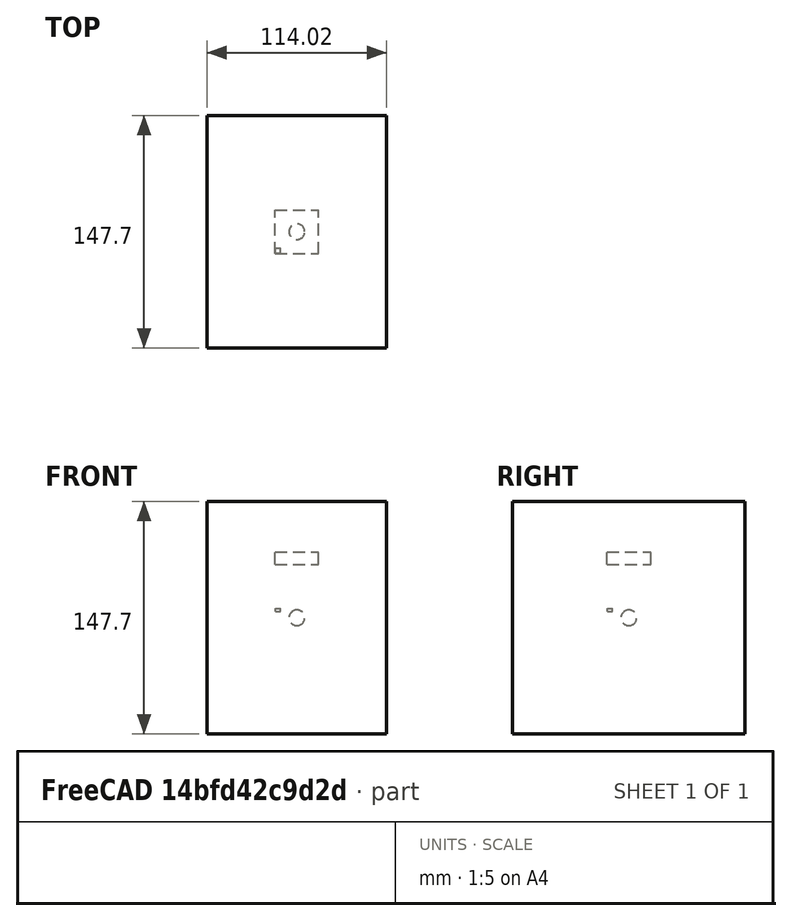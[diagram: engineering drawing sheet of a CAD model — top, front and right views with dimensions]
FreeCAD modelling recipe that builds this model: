
FCSTD DOCUMENT  (FreeCAD 0.20R29177 (Git))
Label: NewBS-NoArray-borderTest-1
License: All rights reserved
objects: App::DocumentObjectGroupPython×1272, App::Link×77, App::Part×7, Part::FeaturePython×4, App::FeaturePython×1
note: 4 computed .brp shape members not serialized (recipe doc carries the construction recipe); baked Part::Feature solids carry a one-line shape summary decoded from their .brp

FEATURE [App::DocumentObjectGroupPython] HALFPI  # scripted group (container) (typed FeaturePython)
  name = HALFPI
  value = pi/2.
FEATURE [App::DocumentObjectGroupPython] PI  # scripted group (container) (typed FeaturePython)
  name = PI
  value = 1.*pi
FEATURE [App::DocumentObjectGroupPython] TWOPI  # scripted group (container) (typed FeaturePython)
  name = TWOPI
  value = 2.*pi
FEATURE [App::DocumentObjectGroupPython] Constants  # scripted group (container) (typed FeaturePython)
  Group = -> [HALFPI,PI,TWOPI]
FEATURE [App::DocumentObjectGroupPython] Variables  # scripted group (container) (typed FeaturePython)
FEATURE [App::DocumentObjectGroupPython] Quantities  # scripted group (container) (typed FeaturePython)
FEATURE [App::DocumentObjectGroupPython] Isotopes  # scripted group (container) (typed FeaturePython)
FEATURE [App::DocumentObjectGroupPython] Elements  # scripted group (container) (typed FeaturePython)
FEATURE [App::DocumentObjectGroupPython] G4_AIR  label="G4_AIR : 1.000"  # scripted group (container) (typed FeaturePython)
  n = 1
FEATURE [App::DocumentObjectGroupPython] Air  # scripted group (container) (typed FeaturePython)
  Dunit = mg/cm3
  Dvalue = 1.29
  Group = -> [G4_AIR]
  RINDEX = AirRINDEX
  conduct = 2
  density = 1
  expand = 3
  name = Air
  specific = 4
FEATURE [App::DocumentObjectGroupPython] SY  # scripted group (container) (typed FeaturePython)
  coldim = 1
  values = 100000/MeV
FEATURE [App::DocumentObjectGroupPython] RS  # scripted group (container) (typed FeaturePython)
  coldim = 1
  values = 1
FEATURE [App::DocumentObjectGroupPython] FTC  # scripted group (container) (typed FeaturePython)
  coldim = 1
  values = 21.5*ns
FEATURE [App::DocumentObjectGroupPython] STC  # scripted group (container) (typed FeaturePython)
  coldim = 1
  values = 43.8*ns
FEATURE [App::DocumentObjectGroupPython] RY1  # scripted group (container) (typed FeaturePython)
  coldim = 1
  values = 95
FEATURE [App::DocumentObjectGroupPython] RY2  # scripted group (container) (typed FeaturePython)
  coldim = 1
  values = 5
FEATURE [App::DocumentObjectGroupPython] YR  # scripted group (container) (typed FeaturePython)
  coldim = 1
  values = 0.8
FEATURE [App::DocumentObjectGroupPython] SCINTLAR  # scripted group (container) (typed FeaturePython)
  coldim = 2
  values = <blob: 2358 chars omitted>
FEATURE [App::DocumentObjectGroupPython] RINDEXLAR  # scripted group (container) (typed FeaturePython)
  coldim = 2
  values = <blob: 9384 chars omitted>
FEATURE [App::DocumentObjectGroupPython] ABSLENGTHLAR  # scripted group (container) (typed FeaturePython)
  coldim = 2
  values = 7.74901*eV 10.0*m 7.77525*eV 10.0*m 7.80167*eV 10.0*m 7.82827*eV 10.0*m 7.85506*eV 10.0*m 7.88202*eV 10.0*m 7.90917*eV 10.0*m 7.93651*eV 10.0*m 7.96404*eV 10.0*m 7.99176*eV 10.0*m 8.01968*eV 10.0*m 8.04779*eV 10.0*m 8.07609*eV 10.0*m 8.1046*eV 10.0*m 8.13331*eV 10.0*m 8.16222*eV 10.0*m 8.19134*eV 10.0*m 8.22067*eV 10.0*m 8.25021*eV 10.0*m 8.27996*eV 10.0*m 8.30993*eV 10.0*m 8.34012*eV 10.0*m 8.37052*eV 10.0*m 8.40115*eV 10.0*m 8.432*eV 10.0*m 8.46308*eV 10.0*m 8.4944*eV 10.0*m 8.52594*eV 10.0*m 8.55772*eV 10.0*m 8.58973*eV 10.0*m 8.62199*eV 10.0*m 8.65449*eV 10.0*m 8.68723*eV 10.0*m 8.72023*eV 10.0*m 8.75347*eV 10.0*m 8.78697*eV 10.0*m 8.82073*eV 10.0*m 8.85475*eV 10.0*m 8.88903*eV 10.0*m 8.92358*eV 10.0*m 8.9584*eV 10.0*m 8.99349*eV 10.0*m 9.02885*eV 10.0*m 9.0645*eV 10.0*m 9.10043*eV 10.0*m 9.13664*eV 10.0*m 9.17314*eV 10.0*m 9.20994*eV 10.0*m 9.24703*eV 10.0*m 9.28442*eV 10.0*m 9.32212*eV 10.0*m 9.36012*eV 10.0*m 9.39844*eV 10.0*m 9.43707*eV 10.0*m 9.47602*eV 10.0*m 9.51529*eV 10.0*m 9.55489*eV 10.0*m 9.59481*eV 10.0*m 9.63508*eV 10.0*m 9.67568*eV 10.0*m 9.71663*eV 10.0*m 9.75792*eV 10.0*m 9.79957*eV 10.0*m 9.84158*eV 10.0*m 9.88394*eV 10.0*m 9.92668*eV 10.0*m 9.96978*eV 10.0*m 10.0133*eV 10.0*m 10.0571*eV 10.0*m 10.1014*eV 10.0*m 10.146*eV 10.0*m 10.191*eV 10.0*m 10.2365*eV 10.0*m 10.2823*eV 10.0*m 10.3286*eV 10.0*m 10.3752*eV 10.0*m 10.4223*eV 10.0*m 10.4699*eV 10.0*m 10.5178*eV 10.0*m 10.5662*eV 10.0*m 10.6151*eV 10.0*m 10.6644*eV 10.0*m 10.7142*eV 10.0*m 10.7644*eV 10.0*m 10.8151*eV 10.0*m 10.8663*eV 10.0*m 10.9179*eV 10.0*m 10.9701*eV 10.0*m 11.0228*eV 10.0*m 11.076*eV 10.0*m 11.1296*eV 10.0*m 11.1839*eV 10.0*m 11.2386*eV 10.0*m 11.2939*eV 10.0*m 11.3497*eV 10.0*m 11.4061*eV 10.0*m 11.463*eV 10.0*m 11.5206*eV 10.0*m 11.5787*eV 10.0*m 11.6373*eV 10.0*m
FEATURE [App::DocumentObjectGroupPython] RAYLEIGHLAR  # scripted group (container) (typed FeaturePython)
  coldim = 2
  values = 7.74901*eV 90.0*cm 7.77525*eV 90.0*cm 7.80167*eV 90.0*cm 7.82827*eV 90.0*cm 7.85506*eV 90.0*cm 7.88202*eV 90.0*cm 7.90917*eV 90.0*cm 7.93651*eV 90.0*cm 7.96404*eV 90.0*cm 7.99176*eV 90.0*cm 8.01968*eV 90.0*cm 8.04779*eV 90.0*cm 8.07609*eV 90.0*cm 8.1046*eV 90.0*cm 8.13331*eV 90.0*cm 8.16222*eV 90.0*cm 8.19134*eV 90.0*cm 8.22067*eV 90.0*cm 8.25021*eV 90.0*cm 8.27996*eV 90.0*cm 8.30993*eV 90.0*cm 8.34012*eV 90.0*cm 8.37052*eV 90.0*cm 8.40115*eV 90.0*cm 8.432*eV 90.0*cm 8.46308*eV 90.0*cm 8.4944*eV 90.0*cm 8.52594*eV 90.0*cm 8.55772*eV 90.0*cm 8.58973*eV 90.0*cm 8.62199*eV 90.0*cm 8.65449*eV 90.0*cm 8.68723*eV 90.0*cm 8.72023*eV 90.0*cm 8.75347*eV 90.0*cm 8.78697*eV 90.0*cm 8.82073*eV 90.0*cm 8.85475*eV 90.0*cm 8.88903*eV 90.0*cm 8.92358*eV 90.0*cm 8.9584*eV 90.0*cm 8.99349*eV 90.0*cm 9.02885*eV 90.0*cm 9.0645*eV 90.0*cm 9.10043*eV 90.0*cm 9.13664*eV 90.0*cm 9.17314*eV 90.0*cm 9.20994*eV 90.0*cm 9.24703*eV 90.0*cm 9.28442*eV 90.0*cm 9.32212*eV 90.0*cm 9.36012*eV 90.0*cm 9.39844*eV 90.0*cm 9.43707*eV 90.0*cm 9.47602*eV 90.0*cm 9.51529*eV 90.0*cm 9.55489*eV 90.0*cm 9.59481*eV 90.0*cm 9.63508*eV 90.0*cm 9.67568*eV 90.0*cm 9.71663*eV 90.0*cm 9.75792*eV 90.0*cm 9.79957*eV 90.0*cm 9.84158*eV 90.0*cm 9.88394*eV 90.0*cm 9.92668*eV 90.0*cm 9.96978*eV 90.0*cm 10.0133*eV 90.0*cm 10.0571*eV 90.0*cm 10.1014*eV 90.0*cm 10.146*eV 90.0*cm 10.191*eV 90.0*cm 10.2365*eV 90.0*cm 10.2823*eV 90.0*cm 10.3286*eV 90.0*cm 10.3752*eV 90.0*cm 10.4223*eV 90.0*cm 10.4699*eV 90.0*cm 10.5178*eV 90.0*cm 10.5662*eV 90.0*cm 10.6151*eV 90.0*cm 10.6644*eV 90.0*cm 10.7142*eV 90.0*cm 10.7644*eV 90.0*cm 10.8151*eV 90.0*cm 10.8663*eV 90.0*cm 10.9179*eV 90.0*cm 10.9701*eV 90.0*cm 11.0228*eV 90.0*cm 11.076*eV 90.0*cm 11.1296*eV 90.0*cm 11.1839*eV 90.0*cm 11.2386*eV 90.0*cm 11.2939*eV 90.0*cm 11.3497*eV 90.0*cm 11.4061*eV 90.0*cm 11.463*eV 90.0*cm 11.5206*eV 90.0*cm 11.5787*eV 90.0*cm 11.6373*eV 90.0*cm
FEATURE [App::DocumentObjectGroupPython] REFLECTIVITY  # scripted group (container) (typed FeaturePython)
  coldim = 2
  values = 2.034*eV 0.98 2.068*eV 0.98 2.103*eV 0.98 2.139*eV 0.98 2.177*eV 0.98 2.216*eV 0.98 2.256*eV 0.98 2.298*eV 0.98 2.341*eV 0.98 2.386*eV 0.98 2.433*eV 0.98 2.481*eV 0.98 2.532*eV 0.98 2.585*eV 0.98 2.64*eV 0.98 2.697*eV 0.98 2.757*eV 0.98 2.82*eV 0.98 2.885*eV 0.98 2.954*eV 0.98 3.026*eV 0.98 3.102*eV 0.98 3.181*eV 0.98 3.265*eV 0.98 3.353*eV 0.98 3.446*eV 0.98 3.545*eV 0.98 3.649*eV 0.98 3.76*eV 0.98 3.877*eV 0.98 4.002*eV 0.98 4.136*eV 0.98 5.0*eV 0.98 6.0*eV 0.98 7.0*eV 0.98 8.0*eV 0.98 9.0*eV 0.98 9.0*eV 0.98 10.0*eV 0.98 11.0*eV 0.98 11.6*eV 0.98
FEATURE [App::DocumentObjectGroupPython] EFFICIENCY  # scripted group (container) (typed FeaturePython)
  coldim = 2
  values = 2.034*eV 1 2.068*eV 1 2.103*eV 1 2.139*eV 1 2.177*eV 1 2.216*eV 1 2.256*eV 1 2.298*eV 1 2.341*eV 1 2.386*eV 1 2.433*eV 1 2.481*eV 1 2.532*eV 1 2.585*eV 1 2.64*eV 1 2.697*eV 1 2.757*eV 1 2.82*eV 1 2.885*eV 1 2.954*eV 1 3.026*eV 1 3.102*eV 1 3.181*eV  1 3.265*eV 1 3.353*eV 1 3.446*eV 1 3.545*eV 1 3.649*eV 1 3.76*eV 1 3.877*eV 1 4.002*eV 1 4.136*eV 1 5.0*eV 1 6.0*eV 1 7.0*eV 1 8.0*eV 1 9.0*eV 1 9.0*eV 1 10.0*eV 1 11.0*eV 1 11.6*eV 1
FEATURE [App::DocumentObjectGroupPython] AirRINDEX  # scripted group (container) (typed FeaturePython)
  coldim = 2
  values = 2.034*eV 1 2.068*eV 1 2.103*eV 1 2.139*eV 1 2.177*eV 1 2.216*eV 1 2.256*eV 1 2.298*eV 1 2.341*eV 1 2.386*eV 1 2.433*eV 1 2.481*eV 1 2.532*eV 1 2.585*eV 1 2.64*eV 1 2.697*eV 1 2.757*eV 1 2.82*eV 1 2.885*eV 1 2.954*eV 1 3.026*eV 1 3.102*eV 1 3.181*eV 1 3.265*eV 1 3.353*eV 1 3.446*eV 1 3.545*eV 1 3.649*eV 1 3.76*eV 1 3.877*eV 1 4.002*eV 1 4.136*eV 1 5.0*eV 1 6.0*eV 1 7.0*eV 1 8.0*eV 1 9.0*eV 1 10.0*eV 1 11.0*eV 1 11.6*eV 1
FEATURE [App::DocumentObjectGroupPython] Matrix  # scripted group (container) (typed FeaturePython)
  Group = -> [SY,RS,FTC,STC,RY1,RY2,YR,SCINTLAR,RINDEXLAR,ABSLENGTHLAR,RAYLEIGHLAR,REFLECTIVITY,EFFICIENCY,AirRINDEX]
FEATURE [App::DocumentObjectGroupPython] ScintWrap  # scripted group (container) (typed FeaturePython)
  EFFICIENCY = EFFICIENCY
  REFLECTIVITY = REFLECTIVITY
  finish = 39
  model = 0
  type = 2
  value = 1
FEATURE [App::DocumentObjectGroupPython] Surfaces  # scripted group (container) (typed FeaturePython)
  Group = -> [ScintWrap]
FEATURE [App::DocumentObjectGroupPython] Opticals  # scripted group (container) (typed FeaturePython)
  Group = -> [Matrix,Surfaces]
FEATURE [App::DocumentObjectGroupPython] G4Isotopes  # scripted group (container) (typed FeaturePython)
FEATURE [App::DocumentObjectGroupPython] H_element  # scripted group (container) (typed FeaturePython)
  Z = 1
  atom_value = 1.008
  formula = H
  name = H_element
FEATURE [App::DocumentObjectGroupPython] He_element  # scripted group (container) (typed FeaturePython)
  Z = 2
  atom_value = 4.0026
  formula = He
  name = He_element
FEATURE [App::DocumentObjectGroupPython] Li_element  # scripted group (container) (typed FeaturePython)
  Z = 3
  atom_value = 6.94
  formula = Li
  name = Li_element
FEATURE [App::DocumentObjectGroupPython] Be_element  # scripted group (container) (typed FeaturePython)
  Z = 4
  atom_value = 9.01218
  formula = Be
  name = Be_element
FEATURE [App::DocumentObjectGroupPython] B_element  # scripted group (container) (typed FeaturePython)
  Z = 5
  atom_value = 10.81
  formula = B
  name = B_element
FEATURE [App::DocumentObjectGroupPython] C_element  # scripted group (container) (typed FeaturePython)
  Z = 6
  atom_value = 12.011
  formula = C
  name = C_element
FEATURE [App::DocumentObjectGroupPython] N_element  # scripted group (container) (typed FeaturePython)
  Z = 7
  atom_value = 14.007
  formula = N
  name = N_element
FEATURE [App::DocumentObjectGroupPython] O_element  # scripted group (container) (typed FeaturePython)
  Z = 8
  atom_value = 15.999
  formula = O
  name = O_element
FEATURE [App::DocumentObjectGroupPython] F_element  # scripted group (container) (typed FeaturePython)
  Z = 9
  atom_value = 18.9984
  formula = F
  name = F_element
FEATURE [App::DocumentObjectGroupPython] Ne_element  # scripted group (container) (typed FeaturePython)
  Z = 10
  atom_value = 20.1797
  formula = Ne
  name = Ne_element
FEATURE [App::DocumentObjectGroupPython] Na_element  # scripted group (container) (typed FeaturePython)
  Z = 11
  atom_value = 22.9898
  formula = Na
  name = Na_element
FEATURE [App::DocumentObjectGroupPython] Mg_element  # scripted group (container) (typed FeaturePython)
  Z = 12
  atom_value = 24.305
  formula = Mg
  name = Mg_element
FEATURE [App::DocumentObjectGroupPython] Al_element  # scripted group (container) (typed FeaturePython)
  Z = 13
  atom_value = 26.9815
  formula = Al
  name = Al_element
FEATURE [App::DocumentObjectGroupPython] Si_element  # scripted group (container) (typed FeaturePython)
  Z = 14
  atom_value = 28.085
  formula = Si
  name = Si_element
FEATURE [App::DocumentObjectGroupPython] P_element  # scripted group (container) (typed FeaturePython)
  Z = 15
  atom_value = 30.9738
  formula = P
  name = P_element
FEATURE [App::DocumentObjectGroupPython] S_element  # scripted group (container) (typed FeaturePython)
  Z = 16
  atom_value = 32.06
  formula = S
  name = S_element
FEATURE [App::DocumentObjectGroupPython] Cl_element  # scripted group (container) (typed FeaturePython)
  Z = 17
  atom_value = 35.45
  formula = Cl
  name = Cl_element
FEATURE [App::DocumentObjectGroupPython] Ar_element  # scripted group (container) (typed FeaturePython)
  Z = 18
  atom_value = 39.95
  formula = Ar
  name = Ar_element
FEATURE [App::DocumentObjectGroupPython] K_element  # scripted group (container) (typed FeaturePython)
  Z = 19
  atom_value = 39.0983
  formula = K
  name = K_element
FEATURE [App::DocumentObjectGroupPython] Ca_element  # scripted group (container) (typed FeaturePython)
  Z = 20
  atom_value = 40.078
  formula = Ca
  name = Ca_element
FEATURE [App::DocumentObjectGroupPython] Sc_element  # scripted group (container) (typed FeaturePython)
  Z = 21
  atom_value = 44.9559
  formula = Sc
  name = Sc_element
FEATURE [App::DocumentObjectGroupPython] Ti_element  # scripted group (container) (typed FeaturePython)
  Z = 22
  atom_value = 47.867
  formula = Ti
  name = Ti_element
FEATURE [App::DocumentObjectGroupPython] V_element  # scripted group (container) (typed FeaturePython)
  Z = 23
  atom_value = 50.9415
  formula = V
  name = V_element
FEATURE [App::DocumentObjectGroupPython] Cr_element  # scripted group (container) (typed FeaturePython)
  Z = 24
  atom_value = 51.9961
  formula = Cr
  name = Cr_element
FEATURE [App::DocumentObjectGroupPython] Mn_element  # scripted group (container) (typed FeaturePython)
  Z = 25
  atom_value = 54.938
  formula = Mn
  name = Mn_element
FEATURE [App::DocumentObjectGroupPython] Fe_element  # scripted group (container) (typed FeaturePython)
  Z = 26
  atom_value = 55.845
  formula = Fe
  name = Fe_element
FEATURE [App::DocumentObjectGroupPython] Co_element  # scripted group (container) (typed FeaturePython)
  Z = 27
  atom_value = 58.9332
  formula = Co
  name = Co_element
FEATURE [App::DocumentObjectGroupPython] Ni_element  # scripted group (container) (typed FeaturePython)
  Z = 28
  atom_value = 58.6934
  formula = Ni
  name = Ni_element
FEATURE [App::DocumentObjectGroupPython] Cu_element  # scripted group (container) (typed FeaturePython)
  Z = 29
  atom_value = 63.546
  formula = Cu
  name = Cu_element
FEATURE [App::DocumentObjectGroupPython] Zn_element  # scripted group (container) (typed FeaturePython)
  Z = 30
  atom_value = 65.38
  formula = Zn
  name = Zn_element
FEATURE [App::DocumentObjectGroupPython] Ga_element  # scripted group (container) (typed FeaturePython)
  Z = 31
  atom_value = 69.723
  formula = Ga
  name = Ga_element
FEATURE [App::DocumentObjectGroupPython] Ge_element  # scripted group (container) (typed FeaturePython)
  Z = 32
  atom_value = 72.63
  formula = Ge
  name = Ge_element
FEATURE [App::DocumentObjectGroupPython] As_element  # scripted group (container) (typed FeaturePython)
  Z = 33
  atom_value = 74.9216
  formula = As
  name = As_element
FEATURE [App::DocumentObjectGroupPython] Se_element  # scripted group (container) (typed FeaturePython)
  Z = 34
  atom_value = 78.971
  formula = Se
  name = Se_element
FEATURE [App::DocumentObjectGroupPython] Br_element  # scripted group (container) (typed FeaturePython)
  Z = 35
  atom_value = 79.904
  formula = Br
  name = Br_element
FEATURE [App::DocumentObjectGroupPython] Kr_element  # scripted group (container) (typed FeaturePython)
  Z = 36
  atom_value = 83.798
  formula = Kr
  name = Kr_element
FEATURE [App::DocumentObjectGroupPython] Rb_element  # scripted group (container) (typed FeaturePython)
  Z = 37
  atom_value = 85.4678
  formula = Rb
  name = Rb_element
FEATURE [App::DocumentObjectGroupPython] Sr_element  # scripted group (container) (typed FeaturePython)
  Z = 38
  atom_value = 87.62
  formula = Sr
  name = Sr_element
FEATURE [App::DocumentObjectGroupPython] Y_element  # scripted group (container) (typed FeaturePython)
  Z = 39
  atom_value = 88.9058
  formula = Y
  name = Y_element
FEATURE [App::DocumentObjectGroupPython] Zr_element  # scripted group (container) (typed FeaturePython)
  Z = 40
  atom_value = 91.224
  formula = Zr
  name = Zr_element
FEATURE [App::DocumentObjectGroupPython] Nb_element  # scripted group (container) (typed FeaturePython)
  Z = 41
  atom_value = 92.9064
  formula = Nb
  name = Nb_element
FEATURE [App::DocumentObjectGroupPython] Mo_element  # scripted group (container) (typed FeaturePython)
  Z = 42
  atom_value = 95.95
  formula = Mo
  name = Mo_element
FEATURE [App::DocumentObjectGroupPython] Tc_element  # scripted group (container) (typed FeaturePython)
  Z = 43
  atom_value = 97
  formula = Tc
  name = Tc_element
FEATURE [App::DocumentObjectGroupPython] Ru_element  # scripted group (container) (typed FeaturePython)
  Z = 44
  atom_value = 101.07
  formula = Ru
  name = Ru_element
FEATURE [App::DocumentObjectGroupPython] Rh_element  # scripted group (container) (typed FeaturePython)
  Z = 45
  atom_value = 102.905
  formula = Rh
  name = Rh_element
FEATURE [App::DocumentObjectGroupPython] Pd_element  # scripted group (container) (typed FeaturePython)
  Z = 46
  atom_value = 106.42
  formula = Pd
  name = Pd_element
FEATURE [App::DocumentObjectGroupPython] Ag_element  # scripted group (container) (typed FeaturePython)
  Z = 47
  atom_value = 107.868
  formula = Ag
  name = Ag_element
FEATURE [App::DocumentObjectGroupPython] Cd_element  # scripted group (container) (typed FeaturePython)
  Z = 48
  atom_value = 112.414
  formula = Cd
  name = Cd_element
FEATURE [App::DocumentObjectGroupPython] In_element  # scripted group (container) (typed FeaturePython)
  Z = 49
  atom_value = 114.818
  formula = In
  name = In_element
FEATURE [App::DocumentObjectGroupPython] Sn_element  # scripted group (container) (typed FeaturePython)
  Z = 50
  atom_value = 118.71
  formula = Sn
  name = Sn_element
FEATURE [App::DocumentObjectGroupPython] Sb_element  # scripted group (container) (typed FeaturePython)
  Z = 51
  atom_value = 121.76
  formula = Sb
  name = Sb_element
FEATURE [App::DocumentObjectGroupPython] Te_element  # scripted group (container) (typed FeaturePython)
  Z = 52
  atom_value = 127.6
  formula = Te
  name = Te_element
FEATURE [App::DocumentObjectGroupPython] I_element  # scripted group (container) (typed FeaturePython)
  Z = 53
  atom_value = 126.904
  formula = I
  name = I_element
FEATURE [App::DocumentObjectGroupPython] Xe_element  # scripted group (container) (typed FeaturePython)
  Z = 54
  atom_value = 131.293
  formula = Xe
  name = Xe_element
FEATURE [App::DocumentObjectGroupPython] Cs_element  # scripted group (container) (typed FeaturePython)
  Z = 55
  atom_value = 132.905
  formula = Cs
  name = Cs_element
FEATURE [App::DocumentObjectGroupPython] Ba_element  # scripted group (container) (typed FeaturePython)
  Z = 56
  atom_value = 137.327
  formula = Ba
  name = Ba_element
FEATURE [App::DocumentObjectGroupPython] La_element  # scripted group (container) (typed FeaturePython)
  Z = 57
  atom_value = 138.905
  formula = La
  name = La_element
FEATURE [App::DocumentObjectGroupPython] Ce_element  # scripted group (container) (typed FeaturePython)
  Z = 58
  atom_value = 140.116
  formula = Ce
  name = Ce_element
FEATURE [App::DocumentObjectGroupPython] Pr_element  # scripted group (container) (typed FeaturePython)
  Z = 59
  atom_value = 140.908
  formula = Pr
  name = Pr_element
FEATURE [App::DocumentObjectGroupPython] Nd_element  # scripted group (container) (typed FeaturePython)
  Z = 60
  atom_value = 144.242
  formula = Nd
  name = Nd_element
FEATURE [App::DocumentObjectGroupPython] Pm_element  # scripted group (container) (typed FeaturePython)
  Z = 61
  atom_value = 145
  formula = Pm
  name = Pm_element
FEATURE [App::DocumentObjectGroupPython] Sm_element  # scripted group (container) (typed FeaturePython)
  Z = 62
  atom_value = 150.36
  formula = Sm
  name = Sm_element
FEATURE [App::DocumentObjectGroupPython] Eu_element  # scripted group (container) (typed FeaturePython)
  Z = 63
  atom_value = 151.964
  formula = Eu
  name = Eu_element
FEATURE [App::DocumentObjectGroupPython] Gd_element  # scripted group (container) (typed FeaturePython)
  Z = 64
  atom_value = 157.25
  formula = Gd
  name = Gd_element
FEATURE [App::DocumentObjectGroupPython] Tb_element  # scripted group (container) (typed FeaturePython)
  Z = 65
  atom_value = 158.925
  formula = Tb
  name = Tb_element
FEATURE [App::DocumentObjectGroupPython] Dy_element  # scripted group (container) (typed FeaturePython)
  Z = 66
  atom_value = 162.5
  formula = Dy
  name = Dy_element
FEATURE [App::DocumentObjectGroupPython] Ho_element  # scripted group (container) (typed FeaturePython)
  Z = 67
  atom_value = 164.93
  formula = Ho
  name = Ho_element
FEATURE [App::DocumentObjectGroupPython] Er_element  # scripted group (container) (typed FeaturePython)
  Z = 68
  atom_value = 167.259
  formula = Er
  name = Er_element
FEATURE [App::DocumentObjectGroupPython] Tm_element  # scripted group (container) (typed FeaturePython)
  Z = 69
  atom_value = 168.934
  formula = Tm
  name = Tm_element
FEATURE [App::DocumentObjectGroupPython] Yb_element  # scripted group (container) (typed FeaturePython)
  Z = 70
  atom_value = 173.045
  formula = Yb
  name = Yb_element
FEATURE [App::DocumentObjectGroupPython] Lu_element  # scripted group (container) (typed FeaturePython)
  Z = 71
  atom_value = 174.967
  formula = Lu
  name = Lu_element
FEATURE [App::DocumentObjectGroupPython] Hf_element  # scripted group (container) (typed FeaturePython)
  Z = 72
  atom_value = 178.49
  formula = Hf
  name = Hf_element
FEATURE [App::DocumentObjectGroupPython] Ta_element  # scripted group (container) (typed FeaturePython)
  Z = 73
  atom_value = 180.948
  formula = Ta
  name = Ta_element
FEATURE [App::DocumentObjectGroupPython] W_element  # scripted group (container) (typed FeaturePython)
  Z = 74
  atom_value = 183.84
  formula = W
  name = W_element
FEATURE [App::DocumentObjectGroupPython] Re_element  # scripted group (container) (typed FeaturePython)
  Z = 75
  atom_value = 186.207
  formula = Re
  name = Re_element
FEATURE [App::DocumentObjectGroupPython] Os_element  # scripted group (container) (typed FeaturePython)
  Z = 76
  atom_value = 190.23
  formula = Os
  name = Os_element
FEATURE [App::DocumentObjectGroupPython] Ir_element  # scripted group (container) (typed FeaturePython)
  Z = 77
  atom_value = 192.217
  formula = Ir
  name = Ir_element
FEATURE [App::DocumentObjectGroupPython] Pt_element  # scripted group (container) (typed FeaturePython)
  Z = 78
  atom_value = 195.084
  formula = Pt
  name = Pt_element
FEATURE [App::DocumentObjectGroupPython] Au_element  # scripted group (container) (typed FeaturePython)
  Z = 79
  atom_value = 196.967
  formula = Au
  name = Au_element
FEATURE [App::DocumentObjectGroupPython] Hg_element  # scripted group (container) (typed FeaturePython)
  Z = 80
  atom_value = 200.592
  formula = Hg
  name = Hg_element
FEATURE [App::DocumentObjectGroupPython] Tl_element  # scripted group (container) (typed FeaturePython)
  Z = 81
  atom_value = 204.38
  formula = Tl
  name = Tl_element
FEATURE [App::DocumentObjectGroupPython] Pb_element  # scripted group (container) (typed FeaturePython)
  Z = 82
  atom_value = 207.2
  formula = Pb
  name = Pb_element
FEATURE [App::DocumentObjectGroupPython] Bi_element  # scripted group (container) (typed FeaturePython)
  Z = 83
  atom_value = 208.98
  formula = Bi
  name = Bi_element
FEATURE [App::DocumentObjectGroupPython] Po_element  # scripted group (container) (typed FeaturePython)
  Z = 84
  atom_value = 209
  formula = Po
  name = Po_element
FEATURE [App::DocumentObjectGroupPython] At_element  # scripted group (container) (typed FeaturePython)
  Z = 85
  atom_value = 210
  formula = At
  name = At_element
FEATURE [App::DocumentObjectGroupPython] Rn_element  # scripted group (container) (typed FeaturePython)
  Z = 86
  atom_value = 222
  formula = Rn
  name = Rn_element
FEATURE [App::DocumentObjectGroupPython] Fr_element  # scripted group (container) (typed FeaturePython)
  Z = 87
  atom_value = 223
  formula = Fr
  name = Fr_element
FEATURE [App::DocumentObjectGroupPython] Ra_element  # scripted group (container) (typed FeaturePython)
  Z = 88
  atom_value = 226
  formula = Ra
  name = Ra_element
FEATURE [App::DocumentObjectGroupPython] Ac_element  # scripted group (container) (typed FeaturePython)
  Z = 89
  atom_value = 227
  formula = Ac
  name = Ac_element
FEATURE [App::DocumentObjectGroupPython] Th_element  # scripted group (container) (typed FeaturePython)
  Z = 90
  atom_value = 232.038
  formula = Th
  name = Th_element
FEATURE [App::DocumentObjectGroupPython] Pa_element  # scripted group (container) (typed FeaturePython)
  Z = 91
  atom_value = 231.036
  formula = Pa
  name = Pa_element
FEATURE [App::DocumentObjectGroupPython] U_element  # scripted group (container) (typed FeaturePython)
  Z = 92
  atom_value = 238.029
  formula = U
  name = U_element
FEATURE [App::DocumentObjectGroupPython] Np_element  # scripted group (container) (typed FeaturePython)
  Z = 93
  atom_value = 237
  formula = Np
  name = Np_element
FEATURE [App::DocumentObjectGroupPython] Pu_element  # scripted group (container) (typed FeaturePython)
  Z = 94
  atom_value = 244
  formula = Pu
  name = Pu_element
FEATURE [App::DocumentObjectGroupPython] Am_element  # scripted group (container) (typed FeaturePython)
  Z = 95
  atom_value = 243
  formula = Am
  name = Am_element
FEATURE [App::DocumentObjectGroupPython] Cm_element  # scripted group (container) (typed FeaturePython)
  Z = 96
  atom_value = 247
  formula = Cm
  name = Cm_element
FEATURE [App::DocumentObjectGroupPython] Bk_element  # scripted group (container) (typed FeaturePython)
  Z = 97
  atom_value = 247
  formula = Bk
  name = Bk_element
FEATURE [App::DocumentObjectGroupPython] Cf_element  # scripted group (container) (typed FeaturePython)
  Z = 98
  atom_value = 251
  formula = Cf
  name = Cf_element
FEATURE [App::DocumentObjectGroupPython] G4Elements  # scripted group (container) (typed FeaturePython)
  Group = -> [H_element,He_element,Li_element,Be_element,B_element,C_element,N_element,O_element,F_element,Ne_element,Na_element,Mg_element,Al_element,Si_element,P_element,S_element,Cl_element,Ar_element,K_element,Ca_element,Sc_element,Ti_element,V_element,Cr_element,Mn_element,Fe_element,Co_element,Ni_element,Cu_element,Zn_element,Ga_element,Ge_element,As_element,Se_element,Br_element,Kr_element,Rb_element,+61 more]
FEATURE [App::DocumentObjectGroupPython] H_element001  label="H_element : 0.101"  # scripted group (container) (typed FeaturePython)
  n = 0.101327
FEATURE [App::DocumentObjectGroupPython] C_element001  label="C_element : 0.775"  # scripted group (container) (typed FeaturePython)
  n = 0.7755
FEATURE [App::DocumentObjectGroupPython] N_element001  label="N_element : 0.035"  # scripted group (container) (typed FeaturePython)
  n = 0.035057
FEATURE [App::DocumentObjectGroupPython] O_element001  label="O_element : 0.052"  # scripted group (container) (typed FeaturePython)
  n = 0.0523159
FEATURE [App::DocumentObjectGroupPython] F_element001  label="F_element : 0.017"  # scripted group (container) (typed FeaturePython)
  n = 0.017422
FEATURE [App::DocumentObjectGroupPython] Ca_element001  label="Ca_element : 0.018"  # scripted group (container) (typed FeaturePython)
  n = 0.018378
FEATURE [App::DocumentObjectGroupPython] G4_A_150_TISSUE  label="G4_A-150_TISSUE"  # scripted group (container) (typed FeaturePython)
  Dunit = g/cm3
  Dvalue = 1.127
  Group = -> [H_element001,C_element001,N_element001,O_element001,F_element001,Ca_element001]
  conduct = 2
  density = 1
  expand = 3
  formula = G4_A-150_TISSUE
  name = G4_A-150_TISSUE
  specific = 4
FEATURE [App::DocumentObjectGroupPython] C_element002  label="C_element : 3"  # scripted group (container) (typed FeaturePython)
  n = 3
  ref = C_element
FEATURE [App::DocumentObjectGroupPython] H_element002  label="H_element : 6"  # scripted group (container) (typed FeaturePython)
  n = 6
  ref = H_element
FEATURE [App::DocumentObjectGroupPython] O_element002  label="O_element : 1"  # scripted group (container) (typed FeaturePython)
  n = 1
  ref = O_element
FEATURE [App::DocumentObjectGroupPython] G4_ACETONE  # scripted group (container) (typed FeaturePython)
  Dunit = g/cm3
  Dvalue = 0.7899
  Group = -> [C_element002,H_element002,O_element002]
  conduct = 2
  density = 1
  expand = 3
  formula = G4_ACETONE
  name = G4_ACETONE
  specific = 4
FEATURE [App::DocumentObjectGroupPython] C_element003  label="C_element : 2"  # scripted group (container) (typed FeaturePython)
  n = 2
  ref = C_element
FEATURE [App::DocumentObjectGroupPython] H_element003  label="H_element : 2"  # scripted group (container) (typed FeaturePython)
  n = 2
  ref = H_element
FEATURE [App::DocumentObjectGroupPython] G4_ACETYLENE  # scripted group (container) (typed FeaturePython)
  Dunit = g/cm3
  Dvalue = 0.0010967
  Group = -> [C_element003,H_element003]
  conduct = 2
  density = 1
  expand = 3
  formula = G4_ACETYLENE
  name = G4_ACETYLENE
  specific = 4
FEATURE [App::DocumentObjectGroupPython] C_element004  label="C_element : 5"  # scripted group (container) (typed FeaturePython)
  n = 5
  ref = C_element
FEATURE [App::DocumentObjectGroupPython] H_element004  label="H_element : 5"  # scripted group (container) (typed FeaturePython)
  n = 5
  ref = H_element
FEATURE [App::DocumentObjectGroupPython] N_element002  label="N_element : 5"  # scripted group (container) (typed FeaturePython)
  n = 5
  ref = N_element
FEATURE [App::DocumentObjectGroupPython] G4_ADENINE  # scripted group (container) (typed FeaturePython)
  Dunit = g/cm3
  Dvalue = 1.6
  Group = -> [C_element004,H_element004,N_element002]
  conduct = 2
  density = 1
  expand = 3
  formula = G4_ADENINE
  name = G4_ADENINE
  specific = 4
FEATURE [App::DocumentObjectGroupPython] H_element005  label="H_element : 0.114"  # scripted group (container) (typed FeaturePython)
  n = 0.114
FEATURE [App::DocumentObjectGroupPython] C_element005  label="C_element : 0.598"  # scripted group (container) (typed FeaturePython)
  n = 0.598
FEATURE [App::DocumentObjectGroupPython] N_element003  label="N_element : 0.007"  # scripted group (container) (typed FeaturePython)
  n = 0.007
FEATURE [App::DocumentObjectGroupPython] O_element003  label="O_element : 0.278"  # scripted group (container) (typed FeaturePython)
  n = 0.278
FEATURE [App::DocumentObjectGroupPython] Na_element001  label="Na_element : 0.001"  # scripted group (container) (typed FeaturePython)
  n = 0.001
FEATURE [App::DocumentObjectGroupPython] S_element001  label="S_element : 0.001"  # scripted group (container) (typed FeaturePython)
  n = 0.001
FEATURE [App::DocumentObjectGroupPython] Cl_element001  label="Cl_element : 0.001"  # scripted group (container) (typed FeaturePython)
  n = 0.001
FEATURE [App::DocumentObjectGroupPython] G4_ADIPOSE_TISSUE_ICRP  # scripted group (container) (typed FeaturePython)
  Dunit = g/cm3
  Dvalue = 0.95
  Group = -> [H_element005,C_element005,N_element003,O_element003,Na_element001,S_element001,Cl_element001]
  conduct = 2
  density = 1
  expand = 3
  formula = G4_ADIPOSE_TISSUE_ICRP
  name = G4_ADIPOSE_TISSUE_ICRP
  specific = 4
FEATURE [App::DocumentObjectGroupPython] C_element006  label="C_element : 0.000"  # scripted group (container) (typed FeaturePython)
  n = 0.000124
FEATURE [App::DocumentObjectGroupPython] N_element004  label="N_element : 0.755"  # scripted group (container) (typed FeaturePython)
  n = 0.755268
FEATURE [App::DocumentObjectGroupPython] O_element004  label="O_element : 0.232"  # scripted group (container) (typed FeaturePython)
  n = 0.231781
FEATURE [App::DocumentObjectGroupPython] Ar_element001  label="Ar_element : 0.013"  # scripted group (container) (typed FeaturePython)
  n = 0.012827
FEATURE [App::DocumentObjectGroupPython] G4_AIR001  label="G4_AIR"  # scripted group (container) (typed FeaturePython)
  Dunit = g/cm3
  Dvalue = 0.00120479
  Group = -> [C_element006,N_element004,O_element004,Ar_element001]
  conduct = 2
  density = 1
  expand = 3
  formula = G4_AIR
  name = G4_AIR
  specific = 4
FEATURE [App::DocumentObjectGroupPython] C_element007  label="C_element : 006"  # scripted group (container) (typed FeaturePython)
  n = 3
  ref = C_element
FEATURE [App::DocumentObjectGroupPython] H_element006  label="H_element : 7"  # scripted group (container) (typed FeaturePython)
  n = 7
  ref = H_element
FEATURE [App::DocumentObjectGroupPython] N_element005  label="N_element : 1"  # scripted group (container) (typed FeaturePython)
  n = 1
  ref = N_element
FEATURE [App::DocumentObjectGroupPython] O_element005  label="O_element : 2"  # scripted group (container) (typed FeaturePython)
  n = 2
  ref = O_element
FEATURE [App::DocumentObjectGroupPython] G4_ALANINE  # scripted group (container) (typed FeaturePython)
  Dunit = g/cm3
  Dvalue = 1.42
  Group = -> [C_element007,H_element006,N_element005,O_element005]
  conduct = 2
  density = 1
  expand = 3
  formula = G4_ALANINE
  name = G4_ALANINE
  specific = 4
FEATURE [App::DocumentObjectGroupPython] Al_element001  label="Al_element : 2"  # scripted group (container) (typed FeaturePython)
  n = 2
  ref = Al_element
FEATURE [App::DocumentObjectGroupPython] O_element006  label="O_element : 3"  # scripted group (container) (typed FeaturePython)
  n = 3
  ref = O_element
FEATURE [App::DocumentObjectGroupPython] G4_ALUMINUM_OXIDE  # scripted group (container) (typed FeaturePython)
  Dunit = g/cm3
  Dvalue = 3.97
  Group = -> [Al_element001,O_element006]
  conduct = 2
  density = 1
  expand = 3
  formula = G4_ALUMINUM_OXIDE
  name = G4_ALUMINUM_OXIDE
  specific = 4
FEATURE [App::DocumentObjectGroupPython] H_element007  label="H_element : 0.106"  # scripted group (container) (typed FeaturePython)
  n = 0.10593
FEATURE [App::DocumentObjectGroupPython] C_element008  label="C_element : 0.789"  # scripted group (container) (typed FeaturePython)
  n = 0.788974
FEATURE [App::DocumentObjectGroupPython] O_element007  label="O_element : 0.105"  # scripted group (container) (typed FeaturePython)
  n = 0.105096
FEATURE [App::DocumentObjectGroupPython] G4_AMBER  # scripted group (container) (typed FeaturePython)
  Dunit = g/cm3
  Dvalue = 1.1
  Group = -> [H_element007,C_element008,O_element007]
  conduct = 2
  density = 1
  expand = 3
  formula = G4_AMBER
  name = G4_AMBER
  specific = 4
FEATURE [App::DocumentObjectGroupPython] N_element006  label="N_element : 006"  # scripted group (container) (typed FeaturePython)
  n = 1
  ref = N_element
FEATURE [App::DocumentObjectGroupPython] H_element008  label="H_element : 3"  # scripted group (container) (typed FeaturePython)
  n = 3
  ref = H_element
FEATURE [App::DocumentObjectGroupPython] G4_AMMONIA  # scripted group (container) (typed FeaturePython)
  Dunit = g/cm3
  Dvalue = 0.000826019
  Group = -> [N_element006,H_element008]
  conduct = 2
  density = 1
  expand = 3
  formula = G4_AMMONIA
  name = G4_AMMONIA
  specific = 4
FEATURE [App::DocumentObjectGroupPython] C_element009  label="C_element : 6"  # scripted group (container) (typed FeaturePython)
  n = 6
  ref = C_element
FEATURE [App::DocumentObjectGroupPython] H_element009  label="H_element : 008"  # scripted group (container) (typed FeaturePython)
  n = 7
  ref = H_element
FEATURE [App::DocumentObjectGroupPython] N_element007  label="N_element : 007"  # scripted group (container) (typed FeaturePython)
  n = 1
  ref = N_element
FEATURE [App::DocumentObjectGroupPython] G4_ANILINE  # scripted group (container) (typed FeaturePython)
  Dunit = g/cm3
  Dvalue = 1.0235
  Group = -> [C_element009,H_element009,N_element007]
  conduct = 2
  density = 1
  expand = 3
  formula = G4_ANILINE
  name = G4_ANILINE
  specific = 4
FEATURE [App::DocumentObjectGroupPython] C_element010  label="C_element : 14"  # scripted group (container) (typed FeaturePython)
  n = 14
  ref = C_element
FEATURE [App::DocumentObjectGroupPython] H_element010  label="H_element : 10"  # scripted group (container) (typed FeaturePython)
  n = 10
  ref = H_element
FEATURE [App::DocumentObjectGroupPython] G4_ANTHRACENE  # scripted group (container) (typed FeaturePython)
  Dunit = g/cm3
  Dvalue = 1.283
  Group = -> [C_element010,H_element010]
  conduct = 2
  density = 1
  expand = 3
  formula = G4_ANTHRACENE
  name = G4_ANTHRACENE
  specific = 4
FEATURE [App::DocumentObjectGroupPython] H_element011  label="H_element : 0.065"  # scripted group (container) (typed FeaturePython)
  n = 0.0654709
FEATURE [App::DocumentObjectGroupPython] C_element011  label="C_element : 0.537"  # scripted group (container) (typed FeaturePython)
  n = 0.536944
FEATURE [App::DocumentObjectGroupPython] N_element008  label="N_element : 0.021"  # scripted group (container) (typed FeaturePython)
  n = 0.0215
FEATURE [App::DocumentObjectGroupPython] O_element008  label="O_element : 0.032"  # scripted group (container) (typed FeaturePython)
  n = 0.032085
FEATURE [App::DocumentObjectGroupPython] F_element002  label="F_element : 0.167"  # scripted group (container) (typed FeaturePython)
  n = 0.167411
FEATURE [App::DocumentObjectGroupPython] Ca_element002  label="Ca_element : 0.177"  # scripted group (container) (typed FeaturePython)
  n = 0.176589
FEATURE [App::DocumentObjectGroupPython] G4_B_100_BONE  label="G4_B-100_BONE"  # scripted group (container) (typed FeaturePython)
  Dunit = g/cm3
  Dvalue = 1.45
  Group = -> [H_element011,C_element011,N_element008,O_element008,F_element002,Ca_element002]
  conduct = 2
  density = 1
  expand = 3
  formula = G4_B-100_BONE
  name = G4_B-100_BONE
  specific = 4
FEATURE [App::DocumentObjectGroupPython] H_element012  label="H_element : 0.057"  # scripted group (container) (typed FeaturePython)
  n = 0.057441
FEATURE [App::DocumentObjectGroupPython] C_element012  label="C_element : 0.790"  # scripted group (container) (typed FeaturePython)
  n = 0.774591
FEATURE [App::DocumentObjectGroupPython] O_element009  label="O_element : 0.168"  # scripted group (container) (typed FeaturePython)
  n = 0.167968
FEATURE [App::DocumentObjectGroupPython] G4_BAKELITE  # scripted group (container) (typed FeaturePython)
  Dunit = g/cm3
  Dvalue = 1.25
  Group = -> [H_element012,C_element012,O_element009]
  conduct = 2
  density = 1
  expand = 3
  formula = G4_BAKELITE
  name = G4_BAKELITE
  specific = 4
FEATURE [App::DocumentObjectGroupPython] Ba_element001  label="Ba_element : 1"  # scripted group (container) (typed FeaturePython)
  n = 1
  ref = Ba_element
FEATURE [App::DocumentObjectGroupPython] F_element003  label="F_element : 2"  # scripted group (container) (typed FeaturePython)
  n = 2
  ref = F_element
FEATURE [App::DocumentObjectGroupPython] G4_BARIUM_FLUORIDE  # scripted group (container) (typed FeaturePython)
  Dunit = g/cm3
  Dvalue = 4.89
  Group = -> [Ba_element001,F_element003]
  conduct = 2
  density = 1
  expand = 3
  formula = G4_BARIUM_FLUORIDE
  name = G4_BARIUM_FLUORIDE
  specific = 4
FEATURE [App::DocumentObjectGroupPython] Ba_element002  label="Ba_element : 002"  # scripted group (container) (typed FeaturePython)
  n = 1
  ref = Ba_element
FEATURE [App::DocumentObjectGroupPython] S_element002  label="S_element : 1"  # scripted group (container) (typed FeaturePython)
  n = 1
  ref = S_element
FEATURE [App::DocumentObjectGroupPython] O_element010  label="O_element : 4"  # scripted group (container) (typed FeaturePython)
  n = 4
  ref = O_element
FEATURE [App::DocumentObjectGroupPython] G4_BARIUM_SULFATE  # scripted group (container) (typed FeaturePython)
  Dunit = g/cm3
  Dvalue = 4.5
  Group = -> [Ba_element002,S_element002,O_element010]
  conduct = 2
  density = 1
  expand = 3
  formula = G4_BARIUM_SULFATE
  name = G4_BARIUM_SULFATE
  specific = 4
FEATURE [App::DocumentObjectGroupPython] C_element013  label="C_element : 007"  # scripted group (container) (typed FeaturePython)
  n = 6
  ref = C_element
FEATURE [App::DocumentObjectGroupPython] H_element013  label="H_element : 009"  # scripted group (container) (typed FeaturePython)
  n = 6
  ref = H_element
FEATURE [App::DocumentObjectGroupPython] G4_BENZENE  # scripted group (container) (typed FeaturePython)
  Dunit = g/cm3
  Dvalue = 0.87865
  Group = -> [C_element013,H_element013]
  conduct = 2
  density = 1
  expand = 3
  formula = G4_BENZENE
  name = G4_BENZENE
  specific = 4
FEATURE [App::DocumentObjectGroupPython] Be_element001  label="Be_element : 1"  # scripted group (container) (typed FeaturePython)
  n = 1
  ref = Be_element
FEATURE [App::DocumentObjectGroupPython] O_element011  label="O_element : 005"  # scripted group (container) (typed FeaturePython)
  n = 1
  ref = O_element
FEATURE [App::DocumentObjectGroupPython] G4_BERYLLIUM_OXIDE  # scripted group (container) (typed FeaturePython)
  Dunit = g/cm3
  Dvalue = 3.01
  Group = -> [Be_element001,O_element011]
  conduct = 2
  density = 1
  expand = 3
  formula = G4_BERYLLIUM_OXIDE
  name = G4_BERYLLIUM_OXIDE
  specific = 4
FEATURE [App::DocumentObjectGroupPython] Bi_element001  label="Bi_element : 4"  # scripted group (container) (typed FeaturePython)
  n = 4
  ref = Bi_element
FEATURE [App::DocumentObjectGroupPython] Ge_element001  label="Ge_element : 3"  # scripted group (container) (typed FeaturePython)
  n = 3
  ref = Ge_element
FEATURE [App::DocumentObjectGroupPython] O_element012  label="O_element : 12"  # scripted group (container) (typed FeaturePython)
  n = 12
  ref = O_element
FEATURE [App::DocumentObjectGroupPython] G4_BGO  # scripted group (container) (typed FeaturePython)
  Dunit = g/cm3
  Dvalue = 7.13
  Group = -> [Bi_element001,Ge_element001,O_element012]
  conduct = 2
  density = 1
  expand = 3
  formula = G4_BGO
  name = G4_BGO
  specific = 4
FEATURE [App::DocumentObjectGroupPython] H_element014  label="H_element : 0.102"  # scripted group (container) (typed FeaturePython)
  n = 0.102
FEATURE [App::DocumentObjectGroupPython] C_element014  label="C_element : 0.110"  # scripted group (container) (typed FeaturePython)
  n = 0.11
FEATURE [App::DocumentObjectGroupPython] N_element009  label="N_element : 0.033"  # scripted group (container) (typed FeaturePython)
  n = 0.033
FEATURE [App::DocumentObjectGroupPython] O_element013  label="O_element : 0.745"  # scripted group (container) (typed FeaturePython)
  n = 0.745
FEATURE [App::DocumentObjectGroupPython] Na_element002  label="Na_element : 0.002"  # scripted group (container) (typed FeaturePython)
  n = 0.001
FEATURE [App::DocumentObjectGroupPython] P_element001  label="P_element : 0.001"  # scripted group (container) (typed FeaturePython)
  n = 0.001
FEATURE [App::DocumentObjectGroupPython] S_element003  label="S_element : 0.002"  # scripted group (container) (typed FeaturePython)
  n = 0.002
FEATURE [App::DocumentObjectGroupPython] Cl_element002  label="Cl_element : 0.003"  # scripted group (container) (typed FeaturePython)
  n = 0.003
FEATURE [App::DocumentObjectGroupPython] K_element001  label="K_element : 0.002"  # scripted group (container) (typed FeaturePython)
  n = 0.002
FEATURE [App::DocumentObjectGroupPython] Fe_element001  label="Fe_element : 0.001"  # scripted group (container) (typed FeaturePython)
  n = 0.001
FEATURE [App::DocumentObjectGroupPython] G4_BLOOD_ICRP  # scripted group (container) (typed FeaturePython)
  Dunit = g/cm3
  Dvalue = 1.06
  Group = -> [H_element014,C_element014,N_element009,O_element013,Na_element002,P_element001,S_element003,Cl_element002,K_element001,Fe_element001]
  conduct = 2
  density = 1
  expand = 3
  formula = G4_BLOOD_ICRP
  name = G4_BLOOD_ICRP
  specific = 4
FEATURE [App::DocumentObjectGroupPython] H_element015  label="H_element : 0.064"  # scripted group (container) (typed FeaturePython)
  n = 0.064
FEATURE [App::DocumentObjectGroupPython] C_element015  label="C_element : 0.278"  # scripted group (container) (typed FeaturePython)
  n = 0.278
FEATURE [App::DocumentObjectGroupPython] N_element010  label="N_element : 0.027"  # scripted group (container) (typed FeaturePython)
  n = 0.027
FEATURE [App::DocumentObjectGroupPython] O_element014  label="O_element : 0.410"  # scripted group (container) (typed FeaturePython)
  n = 0.41
FEATURE [App::DocumentObjectGroupPython] Mg_element001  label="Mg_element : 0.002"  # scripted group (container) (typed FeaturePython)
  n = 0.002
FEATURE [App::DocumentObjectGroupPython] P_element002  label="P_element : 0.070"  # scripted group (container) (typed FeaturePython)
  n = 0.07
FEATURE [App::DocumentObjectGroupPython] S_element004  label="S_element : 0.003"  # scripted group (container) (typed FeaturePython)
  n = 0.002
FEATURE [App::DocumentObjectGroupPython] Ca_element003  label="Ca_element : 0.147"  # scripted group (container) (typed FeaturePython)
  n = 0.147
FEATURE [App::DocumentObjectGroupPython] G4_BONE_COMPACT_ICRU  # scripted group (container) (typed FeaturePython)
  Dunit = g/cm3
  Dvalue = 1.85
  Group = -> [H_element015,C_element015,N_element010,O_element014,Mg_element001,P_element002,S_element004,Ca_element003]
  conduct = 2
  density = 1
  expand = 3
  formula = G4_BONE_COMPACT_ICRU
  name = G4_BONE_COMPACT_ICRU
  specific = 4
FEATURE [App::DocumentObjectGroupPython] H_element016  label="H_element : 0.034"  # scripted group (container) (typed FeaturePython)
  n = 0.034
FEATURE [App::DocumentObjectGroupPython] C_element016  label="C_element : 0.155"  # scripted group (container) (typed FeaturePython)
  n = 0.155
FEATURE [App::DocumentObjectGroupPython] N_element011  label="N_element : 0.042"  # scripted group (container) (typed FeaturePython)
  n = 0.042
FEATURE [App::DocumentObjectGroupPython] O_element015  label="O_element : 0.435"  # scripted group (container) (typed FeaturePython)
  n = 0.435
FEATURE [App::DocumentObjectGroupPython] Na_element003  label="Na_element : 0.003"  # scripted group (container) (typed FeaturePython)
  n = 0.001
FEATURE [App::DocumentObjectGroupPython] Mg_element002  label="Mg_element : 0.003"  # scripted group (container) (typed FeaturePython)
  n = 0.002
FEATURE [App::DocumentObjectGroupPython] P_element003  label="P_element : 0.103"  # scripted group (container) (typed FeaturePython)
  n = 0.103
FEATURE [App::DocumentObjectGroupPython] S_element005  label="S_element : 0.004"  # scripted group (container) (typed FeaturePython)
  n = 0.003
FEATURE [App::DocumentObjectGroupPython] Ca_element004  label="Ca_element : 0.225"  # scripted group (container) (typed FeaturePython)
  n = 0.225
FEATURE [App::DocumentObjectGroupPython] G4_BONE_CORTICAL_ICRP  # scripted group (container) (typed FeaturePython)
  Dunit = g/cm3
  Dvalue = 1.92
  Group = -> [H_element016,C_element016,N_element011,O_element015,Na_element003,Mg_element002,P_element003,S_element005,Ca_element004]
  conduct = 2
  density = 1
  expand = 3
  formula = G4_BONE_CORTICAL_ICRP
  name = G4_BONE_CORTICAL_ICRP
  specific = 4
FEATURE [App::DocumentObjectGroupPython] B_element001  label="B_element : 4"  # scripted group (container) (typed FeaturePython)
  n = 4
  ref = B_element
FEATURE [App::DocumentObjectGroupPython] C_element017  label="C_element : 1"  # scripted group (container) (typed FeaturePython)
  n = 1
  ref = C_element
FEATURE [App::DocumentObjectGroupPython] G4_BORON_CARBIDE  # scripted group (container) (typed FeaturePython)
  Dunit = g/cm3
  Dvalue = 2.52
  Group = -> [B_element001,C_element017]
  conduct = 2
  density = 1
  expand = 3
  formula = G4_BORON_CARBIDE
  name = G4_BORON_CARBIDE
  specific = 4
FEATURE [App::DocumentObjectGroupPython] B_element002  label="B_element : 2"  # scripted group (container) (typed FeaturePython)
  n = 2
  ref = B_element
FEATURE [App::DocumentObjectGroupPython] O_element016  label="O_element : 006"  # scripted group (container) (typed FeaturePython)
  n = 3
  ref = O_element
FEATURE [App::DocumentObjectGroupPython] G4_BORON_OXIDE  # scripted group (container) (typed FeaturePython)
  Dunit = g/cm3
  Dvalue = 1.812
  Group = -> [B_element002,O_element016]
  conduct = 2
  density = 1
  expand = 3
  formula = G4_BORON_OXIDE
  name = G4_BORON_OXIDE
  specific = 4
FEATURE [App::DocumentObjectGroupPython] H_element017  label="H_element : 0.107"  # scripted group (container) (typed FeaturePython)
  n = 0.107
FEATURE [App::DocumentObjectGroupPython] C_element018  label="C_element : 0.145"  # scripted group (container) (typed FeaturePython)
  n = 0.145
FEATURE [App::DocumentObjectGroupPython] N_element012  label="N_element : 0.022"  # scripted group (container) (typed FeaturePython)
  n = 0.022
FEATURE [App::DocumentObjectGroupPython] O_element017  label="O_element : 0.712"  # scripted group (container) (typed FeaturePython)
  n = 0.712
FEATURE [App::DocumentObjectGroupPython] Na_element004  label="Na_element : 0.004"  # scripted group (container) (typed FeaturePython)
  n = 0.002
FEATURE [App::DocumentObjectGroupPython] P_element004  label="P_element : 0.004"  # scripted group (container) (typed FeaturePython)
  n = 0.004
FEATURE [App::DocumentObjectGroupPython] S_element006  label="S_element : 0.005"  # scripted group (container) (typed FeaturePython)
  n = 0.002
FEATURE [App::DocumentObjectGroupPython] Cl_element003  label="Cl_element : 0.004"  # scripted group (container) (typed FeaturePython)
  n = 0.003
FEATURE [App::DocumentObjectGroupPython] K_element002  label="K_element : 0.003"  # scripted group (container) (typed FeaturePython)
  n = 0.003
FEATURE [App::DocumentObjectGroupPython] G4_BRAIN_ICRP  # scripted group (container) (typed FeaturePython)
  Dunit = g/cm3
  Dvalue = 1.04
  Group = -> [H_element017,C_element018,N_element012,O_element017,Na_element004,P_element004,S_element006,Cl_element003,K_element002]
  conduct = 2
  density = 1
  expand = 3
  formula = G4_BRAIN_ICRP
  name = G4_BRAIN_ICRP
  specific = 4
FEATURE [App::DocumentObjectGroupPython] C_element019  label="C_element : 4"  # scripted group (container) (typed FeaturePython)
  n = 4
  ref = C_element
FEATURE [App::DocumentObjectGroupPython] H_element018  label="H_element : 010"  # scripted group (container) (typed FeaturePython)
  n = 10
  ref = H_element
FEATURE [App::DocumentObjectGroupPython] G4_BUTANE  # scripted group (container) (typed FeaturePython)
  Dunit = g/cm3
  Dvalue = 0.00249343
  Group = -> [C_element019,H_element018]
  conduct = 2
  density = 1
  expand = 3
  formula = G4_BUTANE
  name = G4_BUTANE
  specific = 4
FEATURE [App::DocumentObjectGroupPython] C_element020  label="C_element : 008"  # scripted group (container) (typed FeaturePython)
  n = 4
  ref = C_element
FEATURE [App::DocumentObjectGroupPython] H_element019  label="H_element : 011"  # scripted group (container) (typed FeaturePython)
  n = 10
  ref = H_element
FEATURE [App::DocumentObjectGroupPython] O_element018  label="O_element : 007"  # scripted group (container) (typed FeaturePython)
  n = 1
  ref = O_element
FEATURE [App::DocumentObjectGroupPython] G4_N_BUTYL_ALCOHOL  label="G4_N-BUTYL_ALCOHOL"  # scripted group (container) (typed FeaturePython)
  Dunit = g/cm3
  Dvalue = 0.8098
  Group = -> [C_element020,H_element019,O_element018]
  conduct = 2
  density = 1
  expand = 3
  formula = G4_N-BUTYL_ALCOHOL
  name = G4_N-BUTYL_ALCOHOL
  specific = 4
FEATURE [App::DocumentObjectGroupPython] H_element020  label="H_element : 0.025"  # scripted group (container) (typed FeaturePython)
  n = 0.02468
FEATURE [App::DocumentObjectGroupPython] C_element021  label="C_element : 0.502"  # scripted group (container) (typed FeaturePython)
  n = 0.501611
FEATURE [App::DocumentObjectGroupPython] O_element019  label="O_element : 0.005"  # scripted group (container) (typed FeaturePython)
  n = 0.004527
FEATURE [App::DocumentObjectGroupPython] F_element004  label="F_element : 0.465"  # scripted group (container) (typed FeaturePython)
  n = 0.465209
FEATURE [App::DocumentObjectGroupPython] Si_element001  label="Si_element : 0.004"  # scripted group (container) (typed FeaturePython)
  n = 0.003973
FEATURE [App::DocumentObjectGroupPython] G4_C_552  label="G4_C-552"  # scripted group (container) (typed FeaturePython)
  Dunit = g/cm3
  Dvalue = 1.76
  Group = -> [H_element020,C_element021,O_element019,F_element004,Si_element001]
  conduct = 2
  density = 1
  expand = 3
  formula = G4_C-552
  name = G4_C-552
  specific = 4
FEATURE [App::DocumentObjectGroupPython] Cd_element001  label="Cd_element : 1"  # scripted group (container) (typed FeaturePython)
  n = 1
  ref = Cd_element
FEATURE [App::DocumentObjectGroupPython] Te_element001  label="Te_element : 1"  # scripted group (container) (typed FeaturePython)
  n = 1
  ref = Te_element
FEATURE [App::DocumentObjectGroupPython] G4_CADMIUM_TELLURIDE  # scripted group (container) (typed FeaturePython)
  Dunit = g/cm3
  Dvalue = 6.2
  Group = -> [Cd_element001,Te_element001]
  conduct = 2
  density = 1
  expand = 3
  formula = G4_CADMIUM_TELLURIDE
  name = G4_CADMIUM_TELLURIDE
  specific = 4
FEATURE [App::DocumentObjectGroupPython] Cd_element002  label="Cd_element : 002"  # scripted group (container) (typed FeaturePython)
  n = 1
  ref = Cd_element
FEATURE [App::DocumentObjectGroupPython] W_element001  label="W_element : 1"  # scripted group (container) (typed FeaturePython)
  n = 1
  ref = W_element
FEATURE [App::DocumentObjectGroupPython] O_element020  label="O_element : 008"  # scripted group (container) (typed FeaturePython)
  n = 4
  ref = O_element
FEATURE [App::DocumentObjectGroupPython] G4_CADMIUM_TUNGSTATE  # scripted group (container) (typed FeaturePython)
  Dunit = g/cm3
  Dvalue = 7.9
  Group = -> [Cd_element002,W_element001,O_element020]
  conduct = 2
  density = 1
  expand = 3
  formula = G4_CADMIUM_TUNGSTATE
  name = G4_CADMIUM_TUNGSTATE
  specific = 4
FEATURE [App::DocumentObjectGroupPython] Ca_element005  label="Ca_element : 1"  # scripted group (container) (typed FeaturePython)
  n = 1
  ref = Ca_element
FEATURE [App::DocumentObjectGroupPython] C_element022  label="C_element : 009"  # scripted group (container) (typed FeaturePython)
  n = 1
  ref = C_element
FEATURE [App::DocumentObjectGroupPython] O_element021  label="O_element : 009"  # scripted group (container) (typed FeaturePython)
  n = 3
  ref = O_element
FEATURE [App::DocumentObjectGroupPython] G4_CALCIUM_CARBONATE  # scripted group (container) (typed FeaturePython)
  Dunit = g/cm3
  Dvalue = 2.8
  Group = -> [Ca_element005,C_element022,O_element021]
  conduct = 2
  density = 1
  expand = 3
  formula = G4_CALCIUM_CARBONATE
  name = G4_CALCIUM_CARBONATE
  specific = 4
FEATURE [App::DocumentObjectGroupPython] Ca_element006  label="Ca_element : 002"  # scripted group (container) (typed FeaturePython)
  n = 1
  ref = Ca_element
FEATURE [App::DocumentObjectGroupPython] F_element005  label="F_element : 003"  # scripted group (container) (typed FeaturePython)
  n = 2
  ref = F_element
FEATURE [App::DocumentObjectGroupPython] G4_CALCIUM_FLUORIDE  # scripted group (container) (typed FeaturePython)
  Dunit = g/cm3
  Dvalue = 3.18
  Group = -> [Ca_element006,F_element005]
  conduct = 2
  density = 1
  expand = 3
  formula = G4_CALCIUM_FLUORIDE
  name = G4_CALCIUM_FLUORIDE
  specific = 4
FEATURE [App::DocumentObjectGroupPython] Ca_element007  label="Ca_element : 003"  # scripted group (container) (typed FeaturePython)
  n = 1
  ref = Ca_element
FEATURE [App::DocumentObjectGroupPython] O_element022  label="O_element : 010"  # scripted group (container) (typed FeaturePython)
  n = 1
  ref = O_element
FEATURE [App::DocumentObjectGroupPython] G4_CALCIUM_OXIDE  # scripted group (container) (typed FeaturePython)
  Dunit = g/cm3
  Dvalue = 3.3
  Group = -> [Ca_element007,O_element022]
  conduct = 2
  density = 1
  expand = 3
  formula = G4_CALCIUM_OXIDE
  name = G4_CALCIUM_OXIDE
  specific = 4
FEATURE [App::DocumentObjectGroupPython] Ca_element008  label="Ca_element : 004"  # scripted group (container) (typed FeaturePython)
  n = 1
  ref = Ca_element
FEATURE [App::DocumentObjectGroupPython] S_element007  label="S_element : 002"  # scripted group (container) (typed FeaturePython)
  n = 1
  ref = S_element
FEATURE [App::DocumentObjectGroupPython] O_element023  label="O_element : 011"  # scripted group (container) (typed FeaturePython)
  n = 4
  ref = O_element
FEATURE [App::DocumentObjectGroupPython] G4_CALCIUM_SULFATE  # scripted group (container) (typed FeaturePython)
  Dunit = g/cm3
  Dvalue = 2.96
  Group = -> [Ca_element008,S_element007,O_element023]
  conduct = 2
  density = 1
  expand = 3
  formula = G4_CALCIUM_SULFATE
  name = G4_CALCIUM_SULFATE
  specific = 4
FEATURE [App::DocumentObjectGroupPython] Ca_element009  label="Ca_element : 005"  # scripted group (container) (typed FeaturePython)
  n = 1
  ref = Ca_element
FEATURE [App::DocumentObjectGroupPython] W_element002  label="W_element : 002"  # scripted group (container) (typed FeaturePython)
  n = 1
  ref = W_element
FEATURE [App::DocumentObjectGroupPython] O_element024  label="O_element : 012"  # scripted group (container) (typed FeaturePython)
  n = 4
  ref = O_element
FEATURE [App::DocumentObjectGroupPython] G4_CALCIUM_TUNGSTATE  # scripted group (container) (typed FeaturePython)
  Dunit = g/cm3
  Dvalue = 6.062
  Group = -> [Ca_element009,W_element002,O_element024]
  conduct = 2
  density = 1
  expand = 3
  formula = G4_CALCIUM_TUNGSTATE
  name = G4_CALCIUM_TUNGSTATE
  specific = 4
FEATURE [App::DocumentObjectGroupPython] C_element023  label="C_element : 010"  # scripted group (container) (typed FeaturePython)
  n = 1
  ref = C_element
FEATURE [App::DocumentObjectGroupPython] O_element025  label="O_element : 013"  # scripted group (container) (typed FeaturePython)
  n = 2
  ref = O_element
FEATURE [App::DocumentObjectGroupPython] G4_CARBON_DIOXIDE  # scripted group (container) (typed FeaturePython)
  Dunit = g/cm3
  Dvalue = 0.00184212
  Group = -> [C_element023,O_element025]
  conduct = 2
  density = 1
  expand = 3
  formula = G4_CARBON_DIOXIDE
  name = G4_CARBON_DIOXIDE
  specific = 4
FEATURE [App::DocumentObjectGroupPython] C_element024  label="C_element : 011"  # scripted group (container) (typed FeaturePython)
  n = 1
  ref = C_element
FEATURE [App::DocumentObjectGroupPython] Cl_element004  label="Cl_element : 4"  # scripted group (container) (typed FeaturePython)
  n = 4
  ref = Cl_element
FEATURE [App::DocumentObjectGroupPython] G4_CARBON_TETRACHLORIDE  # scripted group (container) (typed FeaturePython)
  Dunit = g/cm3
  Dvalue = 1.594
  Group = -> [C_element024,Cl_element004]
  conduct = 2
  density = 1
  expand = 3
  formula = G4_CARBON_TETRACHLORIDE
  name = G4_CARBON_TETRACHLORIDE
  specific = 4
FEATURE [App::DocumentObjectGroupPython] C_element025  label="C_element : 012"  # scripted group (container) (typed FeaturePython)
  n = 6
  ref = C_element
FEATURE [App::DocumentObjectGroupPython] H_element021  label="H_element : 012"  # scripted group (container) (typed FeaturePython)
  n = 10
  ref = H_element
FEATURE [App::DocumentObjectGroupPython] O_element026  label="O_element : 5"  # scripted group (container) (typed FeaturePython)
  n = 5
  ref = O_element
FEATURE [App::DocumentObjectGroupPython] G4_CELLULOSE_CELLOPHANE  # scripted group (container) (typed FeaturePython)
  Dunit = g/cm3
  Dvalue = 1.42
  Group = -> [C_element025,H_element021,O_element026]
  conduct = 2
  density = 1
  expand = 3
  formula = G4_CELLULOSE_CELLOPHANE
  name = G4_CELLULOSE_CELLOPHANE
  specific = 4
FEATURE [App::DocumentObjectGroupPython] H_element022  label="H_element : 0.067"  # scripted group (container) (typed FeaturePython)
  n = 0.067125
FEATURE [App::DocumentObjectGroupPython] C_element026  label="C_element : 0.545"  # scripted group (container) (typed FeaturePython)
  n = 0.545403
FEATURE [App::DocumentObjectGroupPython] O_element027  label="O_element : 0.387"  # scripted group (container) (typed FeaturePython)
  n = 0.387472
FEATURE [App::DocumentObjectGroupPython] G4_CELLULOSE_BUTYRATE  # scripted group (container) (typed FeaturePython)
  Dunit = g/cm3
  Dvalue = 1.2
  Group = -> [H_element022,C_element026,O_element027]
  conduct = 2
  density = 1
  expand = 3
  formula = G4_CELLULOSE_BUTYRATE
  name = G4_CELLULOSE_BUTYRATE
  specific = 4
FEATURE [App::DocumentObjectGroupPython] H_element023  label="H_element : 0.029"  # scripted group (container) (typed FeaturePython)
  n = 0.029216
FEATURE [App::DocumentObjectGroupPython] C_element027  label="C_element : 0.271"  # scripted group (container) (typed FeaturePython)
  n = 0.271296
FEATURE [App::DocumentObjectGroupPython] N_element013  label="N_element : 0.121"  # scripted group (container) (typed FeaturePython)
  n = 0.121276
FEATURE [App::DocumentObjectGroupPython] O_element028  label="O_element : 0.578"  # scripted group (container) (typed FeaturePython)
  n = 0.578212
FEATURE [App::DocumentObjectGroupPython] G4_CELLULOSE_NITRATE  # scripted group (container) (typed FeaturePython)
  Dunit = g/cm3
  Dvalue = 1.49
  Group = -> [H_element023,C_element027,N_element013,O_element028]
  conduct = 2
  density = 1
  expand = 3
  formula = G4_CELLULOSE_NITRATE
  name = G4_CELLULOSE_NITRATE
  specific = 4
FEATURE [App::DocumentObjectGroupPython] H_element024  label="H_element : 0.108"  # scripted group (container) (typed FeaturePython)
  n = 0.107596
FEATURE [App::DocumentObjectGroupPython] N_element014  label="N_element : 0.001"  # scripted group (container) (typed FeaturePython)
  n = 0.0008
FEATURE [App::DocumentObjectGroupPython] O_element029  label="O_element : 0.875"  # scripted group (container) (typed FeaturePython)
  n = 0.874976
FEATURE [App::DocumentObjectGroupPython] S_element008  label="S_element : 0.015"  # scripted group (container) (typed FeaturePython)
  n = 0.014627
FEATURE [App::DocumentObjectGroupPython] Ce_element001  label="Ce_element : 0.002"  # scripted group (container) (typed FeaturePython)
  n = 0.002001
FEATURE [App::DocumentObjectGroupPython] G4_CERIC_SULFATE  # scripted group (container) (typed FeaturePython)
  Dunit = g/cm3
  Dvalue = 1.03
  Group = -> [H_element024,N_element014,O_element029,S_element008,Ce_element001]
  conduct = 2
  density = 1
  expand = 3
  formula = G4_CERIC_SULFATE
  name = G4_CERIC_SULFATE
  specific = 4
FEATURE [App::DocumentObjectGroupPython] Cs_element001  label="Cs_element : 1"  # scripted group (container) (typed FeaturePython)
  n = 1
  ref = Cs_element
FEATURE [App::DocumentObjectGroupPython] F_element006  label="F_element : 1"  # scripted group (container) (typed FeaturePython)
  n = 1
  ref = F_element
FEATURE [App::DocumentObjectGroupPython] G4_CESIUM_FLUORIDE  # scripted group (container) (typed FeaturePython)
  Dunit = g/cm3
  Dvalue = 4.115
  Group = -> [Cs_element001,F_element006]
  conduct = 2
  density = 1
  expand = 3
  formula = G4_CESIUM_FLUORIDE
  name = G4_CESIUM_FLUORIDE
  specific = 4
FEATURE [App::DocumentObjectGroupPython] Cs_element002  label="Cs_element : 002"  # scripted group (container) (typed FeaturePython)
  n = 1
  ref = Cs_element
FEATURE [App::DocumentObjectGroupPython] I_element001  label="I_element : 1"  # scripted group (container) (typed FeaturePython)
  n = 1
  ref = I_element
FEATURE [App::DocumentObjectGroupPython] G4_CESIUM_IODIDE001  label="G4_CESIUM_IODIDE"  # scripted group (container) (typed FeaturePython)
  Dunit = g/cm3
  Dvalue = 4.51
  Group = -> [Cs_element002,I_element001]
  conduct = 2
  density = 1
  expand = 3
  formula = G4_CESIUM_IODIDE
  name = G4_CESIUM_IODIDE
  specific = 4
FEATURE [App::DocumentObjectGroupPython] C_element028  label="C_element : 013"  # scripted group (container) (typed FeaturePython)
  n = 6
  ref = C_element
FEATURE [App::DocumentObjectGroupPython] H_element025  label="H_element : 013"  # scripted group (container) (typed FeaturePython)
  n = 5
  ref = H_element
FEATURE [App::DocumentObjectGroupPython] Cl_element005  label="Cl_element : 1"  # scripted group (container) (typed FeaturePython)
  n = 1
  ref = Cl_element
FEATURE [App::DocumentObjectGroupPython] G4_CHLOROBENZENE  # scripted group (container) (typed FeaturePython)
  Dunit = g/cm3
  Dvalue = 1.1058
  Group = -> [C_element028,H_element025,Cl_element005]
  conduct = 2
  density = 1
  expand = 3
  formula = G4_CHLOROBENZENE
  name = G4_CHLOROBENZENE
  specific = 4
FEATURE [App::DocumentObjectGroupPython] C_element029  label="C_element : 014"  # scripted group (container) (typed FeaturePython)
  n = 1
  ref = C_element
FEATURE [App::DocumentObjectGroupPython] H_element026  label="H_element : 1"  # scripted group (container) (typed FeaturePython)
  n = 1
  ref = H_element
FEATURE [App::DocumentObjectGroupPython] Cl_element006  label="Cl_element : 3"  # scripted group (container) (typed FeaturePython)
  n = 3
  ref = Cl_element
FEATURE [App::DocumentObjectGroupPython] G4_CHLOROFORM  # scripted group (container) (typed FeaturePython)
  Dunit = g/cm3
  Dvalue = 1.4832
  Group = -> [C_element029,H_element026,Cl_element006]
  conduct = 2
  density = 1
  expand = 3
  formula = G4_CHLOROFORM
  name = G4_CHLOROFORM
  specific = 4
FEATURE [App::DocumentObjectGroupPython] H_element027  label="H_element : 0.010"  # scripted group (container) (typed FeaturePython)
  n = 0.01
FEATURE [App::DocumentObjectGroupPython] C_element030  label="C_element : 0.001"  # scripted group (container) (typed FeaturePython)
  n = 0.001
FEATURE [App::DocumentObjectGroupPython] O_element030  label="O_element : 0.529"  # scripted group (container) (typed FeaturePython)
  n = 0.529107
FEATURE [App::DocumentObjectGroupPython] Na_element005  label="Na_element : 0.016"  # scripted group (container) (typed FeaturePython)
  n = 0.016
FEATURE [App::DocumentObjectGroupPython] Mg_element003  label="Mg_element : 0.004"  # scripted group (container) (typed FeaturePython)
  n = 0.002
FEATURE [App::DocumentObjectGroupPython] Al_element002  label="Al_element : 0.034"  # scripted group (container) (typed FeaturePython)
  n = 0.033872
FEATURE [App::DocumentObjectGroupPython] Si_element002  label="Si_element : 0.337"  # scripted group (container) (typed FeaturePython)
  n = 0.337021
FEATURE [App::DocumentObjectGroupPython] K_element003  label="K_element : 0.013"  # scripted group (container) (typed FeaturePython)
  n = 0.013
FEATURE [App::DocumentObjectGroupPython] Ca_element010  label="Ca_element : 0.044"  # scripted group (container) (typed FeaturePython)
  n = 0.044
FEATURE [App::DocumentObjectGroupPython] Fe_element002  label="Fe_element : 0.014"  # scripted group (container) (typed FeaturePython)
  n = 0.014
FEATURE [App::DocumentObjectGroupPython] G4_CONCRETE  # scripted group (container) (typed FeaturePython)
  Dunit = g/cm3
  Dvalue = 2.3
  Group = -> [H_element027,C_element030,O_element030,Na_element005,Mg_element003,Al_element002,Si_element002,K_element003,Ca_element010,Fe_element002]
  conduct = 2
  density = 1
  expand = 3
  formula = G4_CONCRETE
  name = G4_CONCRETE
  specific = 4
FEATURE [App::DocumentObjectGroupPython] C_element031  label="C_element : 015"  # scripted group (container) (typed FeaturePython)
  n = 6
  ref = C_element
FEATURE [App::DocumentObjectGroupPython] H_element028  label="H_element : 12"  # scripted group (container) (typed FeaturePython)
  n = 12
  ref = H_element
FEATURE [App::DocumentObjectGroupPython] G4_CYCLOHEXANE  # scripted group (container) (typed FeaturePython)
  Dunit = g/cm3
  Dvalue = 0.779
  Group = -> [C_element031,H_element028]
  conduct = 2
  density = 1
  expand = 3
  formula = G4_CYCLOHEXANE
  name = G4_CYCLOHEXANE
  specific = 4
FEATURE [App::DocumentObjectGroupPython] C_element032  label="C_element : 016"  # scripted group (container) (typed FeaturePython)
  n = 6
  ref = C_element
FEATURE [App::DocumentObjectGroupPython] H_element029  label="H_element : 4"  # scripted group (container) (typed FeaturePython)
  n = 4
  ref = H_element
FEATURE [App::DocumentObjectGroupPython] Cl_element007  label="Cl_element : 2"  # scripted group (container) (typed FeaturePython)
  n = 2
  ref = Cl_element
FEATURE [App::DocumentObjectGroupPython] G4_1_2_DICHLOROBENZENE  label="G4_1.2-DICHLOROBENZENE"  # scripted group (container) (typed FeaturePython)
  Dunit = g/cm3
  Dvalue = 1.3048
  Group = -> [C_element032,H_element029,Cl_element007]
  conduct = 2
  density = 1
  expand = 3
  formula = G4_1.2-DICHLOROBENZENE
  name = G4_1.2-DICHLOROBENZENE
  specific = 4
FEATURE [App::DocumentObjectGroupPython] C_element033  label="C_element : 017"  # scripted group (container) (typed FeaturePython)
  n = 4
  ref = C_element
FEATURE [App::DocumentObjectGroupPython] H_element030  label="H_element : 8"  # scripted group (container) (typed FeaturePython)
  n = 8
  ref = H_element
FEATURE [App::DocumentObjectGroupPython] O_element031  label="O_element : 014"  # scripted group (container) (typed FeaturePython)
  n = 1
  ref = O_element
FEATURE [App::DocumentObjectGroupPython] Cl_element008  label="Cl_element : 005"  # scripted group (container) (typed FeaturePython)
  n = 2
  ref = Cl_element
FEATURE [App::DocumentObjectGroupPython] G4_DICHLORODIETHYL_ETHER  # scripted group (container) (typed FeaturePython)
  Dunit = g/cm3
  Dvalue = 1.2199
  Group = -> [C_element033,H_element030,O_element031,Cl_element008]
  conduct = 2
  density = 1
  expand = 3
  formula = G4_DICHLORODIETHYL_ETHER
  name = G4_DICHLORODIETHYL_ETHER
  specific = 4
FEATURE [App::DocumentObjectGroupPython] C_element034  label="C_element : 018"  # scripted group (container) (typed FeaturePython)
  n = 2
  ref = C_element
FEATURE [App::DocumentObjectGroupPython] H_element031  label="H_element : 014"  # scripted group (container) (typed FeaturePython)
  n = 4
  ref = H_element
FEATURE [App::DocumentObjectGroupPython] Cl_element009  label="Cl_element : 006"  # scripted group (container) (typed FeaturePython)
  n = 2
  ref = Cl_element
FEATURE [App::DocumentObjectGroupPython] G4_1_2_DICHLOROETHANE  label="G4_1.2-DICHLOROETHANE"  # scripted group (container) (typed FeaturePython)
  Dunit = g/cm3
  Dvalue = 1.2351
  Group = -> [C_element034,H_element031,Cl_element009]
  conduct = 2
  density = 1
  expand = 3
  formula = G4_1.2-DICHLOROETHANE
  name = G4_1.2-DICHLOROETHANE
  specific = 4
FEATURE [App::DocumentObjectGroupPython] C_element035  label="C_element : 019"  # scripted group (container) (typed FeaturePython)
  n = 4
  ref = C_element
FEATURE [App::DocumentObjectGroupPython] H_element032  label="H_element : 015"  # scripted group (container) (typed FeaturePython)
  n = 10
  ref = H_element
FEATURE [App::DocumentObjectGroupPython] O_element032  label="O_element : 015"  # scripted group (container) (typed FeaturePython)
  n = 1
  ref = O_element
FEATURE [App::DocumentObjectGroupPython] G4_DIETHYL_ETHER  # scripted group (container) (typed FeaturePython)
  Dunit = g/cm3
  Dvalue = 0.71378
  Group = -> [C_element035,H_element032,O_element032]
  conduct = 2
  density = 1
  expand = 3
  formula = G4_DIETHYL_ETHER
  name = G4_DIETHYL_ETHER
  specific = 4
FEATURE [App::DocumentObjectGroupPython] C_element036  label="C_element : 020"  # scripted group (container) (typed FeaturePython)
  n = 3
  ref = C_element
FEATURE [App::DocumentObjectGroupPython] H_element033  label="H_element : 016"  # scripted group (container) (typed FeaturePython)
  n = 7
  ref = H_element
FEATURE [App::DocumentObjectGroupPython] N_element015  label="N_element : 008"  # scripted group (container) (typed FeaturePython)
  n = 1
  ref = N_element
FEATURE [App::DocumentObjectGroupPython] O_element033  label="O_element : 016"  # scripted group (container) (typed FeaturePython)
  n = 1
  ref = O_element
FEATURE [App::DocumentObjectGroupPython] G4_N_N_DIMETHYL_FORMAMIDE  label="G4_N.N-DIMETHYL_FORMAMIDE"  # scripted group (container) (typed FeaturePython)
  Dunit = g/cm3
  Dvalue = 0.9487
  Group = -> [C_element036,H_element033,N_element015,O_element033]
  conduct = 2
  density = 1
  expand = 3
  formula = G4_N.N-DIMETHYL_FORMAMIDE
  name = G4_N.N-DIMETHYL_FORMAMIDE
  specific = 4
FEATURE [App::DocumentObjectGroupPython] C_element037  label="C_element : 021"  # scripted group (container) (typed FeaturePython)
  n = 2
  ref = C_element
FEATURE [App::DocumentObjectGroupPython] H_element034  label="H_element : 017"  # scripted group (container) (typed FeaturePython)
  n = 6
  ref = H_element
FEATURE [App::DocumentObjectGroupPython] O_element034  label="O_element : 017"  # scripted group (container) (typed FeaturePython)
  n = 1
  ref = O_element
FEATURE [App::DocumentObjectGroupPython] S_element009  label="S_element : 003"  # scripted group (container) (typed FeaturePython)
  n = 1
  ref = S_element
FEATURE [App::DocumentObjectGroupPython] G4_DIMETHYL_SULFOXIDE  # scripted group (container) (typed FeaturePython)
  Dunit = g/cm3
  Dvalue = 1.1014
  Group = -> [C_element037,H_element034,O_element034,S_element009]
  conduct = 2
  density = 1
  expand = 3
  formula = G4_DIMETHYL_SULFOXIDE
  name = G4_DIMETHYL_SULFOXIDE
  specific = 4
FEATURE [App::DocumentObjectGroupPython] C_element038  label="C_element : 022"  # scripted group (container) (typed FeaturePython)
  n = 2
  ref = C_element
FEATURE [App::DocumentObjectGroupPython] H_element035  label="H_element : 018"  # scripted group (container) (typed FeaturePython)
  n = 6
  ref = H_element
FEATURE [App::DocumentObjectGroupPython] G4_ETHANE  # scripted group (container) (typed FeaturePython)
  Dunit = g/cm3
  Dvalue = 0.00125324
  Group = -> [C_element038,H_element035]
  conduct = 2
  density = 1
  expand = 3
  formula = G4_ETHANE
  name = G4_ETHANE
  specific = 4
FEATURE [App::DocumentObjectGroupPython] C_element039  label="C_element : 023"  # scripted group (container) (typed FeaturePython)
  n = 2
  ref = C_element
FEATURE [App::DocumentObjectGroupPython] H_element036  label="H_element : 019"  # scripted group (container) (typed FeaturePython)
  n = 6
  ref = H_element
FEATURE [App::DocumentObjectGroupPython] O_element035  label="O_element : 018"  # scripted group (container) (typed FeaturePython)
  n = 1
  ref = O_element
FEATURE [App::DocumentObjectGroupPython] G4_ETHYL_ALCOHOL  # scripted group (container) (typed FeaturePython)
  Dunit = g/cm3
  Dvalue = 0.7893
  Group = -> [C_element039,H_element036,O_element035]
  conduct = 2
  density = 1
  expand = 3
  formula = G4_ETHYL_ALCOHOL
  name = G4_ETHYL_ALCOHOL
  specific = 4
FEATURE [App::DocumentObjectGroupPython] H_element037  label="H_element : 0.090"  # scripted group (container) (typed FeaturePython)
  n = 0.090027
FEATURE [App::DocumentObjectGroupPython] C_element040  label="C_element : 0.585"  # scripted group (container) (typed FeaturePython)
  n = 0.585182
FEATURE [App::DocumentObjectGroupPython] O_element036  label="O_element : 0.325"  # scripted group (container) (typed FeaturePython)
  n = 0.324791
FEATURE [App::DocumentObjectGroupPython] G4_ETHYL_CELLULOSE  # scripted group (container) (typed FeaturePython)
  Dunit = g/cm3
  Dvalue = 1.13
  Group = -> [H_element037,C_element040,O_element036]
  conduct = 2
  density = 1
  expand = 3
  formula = G4_ETHYL_CELLULOSE
  name = G4_ETHYL_CELLULOSE
  specific = 4
FEATURE [App::DocumentObjectGroupPython] C_element041  label="C_element : 024"  # scripted group (container) (typed FeaturePython)
  n = 2
  ref = C_element
FEATURE [App::DocumentObjectGroupPython] H_element038  label="H_element : 020"  # scripted group (container) (typed FeaturePython)
  n = 4
  ref = H_element
FEATURE [App::DocumentObjectGroupPython] G4_ETHYLENE  # scripted group (container) (typed FeaturePython)
  Dunit = g/cm3
  Dvalue = 0.00117497
  Group = -> [C_element041,H_element038]
  conduct = 2
  density = 1
  expand = 3
  formula = G4_ETHYLENE
  name = G4_ETHYLENE
  specific = 4
FEATURE [App::DocumentObjectGroupPython] H_element039  label="H_element : 0.096"  # scripted group (container) (typed FeaturePython)
  n = 0.096
FEATURE [App::DocumentObjectGroupPython] C_element042  label="C_element : 0.195"  # scripted group (container) (typed FeaturePython)
  n = 0.195
FEATURE [App::DocumentObjectGroupPython] N_element016  label="N_element : 0.057"  # scripted group (container) (typed FeaturePython)
  n = 0.057
FEATURE [App::DocumentObjectGroupPython] O_element037  label="O_element : 0.646"  # scripted group (container) (typed FeaturePython)
  n = 0.646
FEATURE [App::DocumentObjectGroupPython] Na_element006  label="Na_element : 0.017"  # scripted group (container) (typed FeaturePython)
  n = 0.001
FEATURE [App::DocumentObjectGroupPython] P_element005  label="P_element : 0.104"  # scripted group (container) (typed FeaturePython)
  n = 0.001
FEATURE [App::DocumentObjectGroupPython] S_element010  label="S_element : 0.016"  # scripted group (container) (typed FeaturePython)
  n = 0.003
FEATURE [App::DocumentObjectGroupPython] Cl_element010  label="Cl_element : 0.005"  # scripted group (container) (typed FeaturePython)
  n = 0.001
FEATURE [App::DocumentObjectGroupPython] G4_EYE_LENS_ICRP  # scripted group (container) (typed FeaturePython)
  Dunit = g/cm3
  Dvalue = 1.07
  Group = -> [H_element039,C_element042,N_element016,O_element037,Na_element006,P_element005,S_element010,Cl_element010]
  conduct = 2
  density = 1
  expand = 3
  formula = G4_EYE_LENS_ICRP
  name = G4_EYE_LENS_ICRP
  specific = 4
FEATURE [App::DocumentObjectGroupPython] Fe_element003  label="Fe_element : 2"  # scripted group (container) (typed FeaturePython)
  n = 2
  ref = Fe_element
FEATURE [App::DocumentObjectGroupPython] O_element038  label="O_element : 019"  # scripted group (container) (typed FeaturePython)
  n = 3
  ref = O_element
FEATURE [App::DocumentObjectGroupPython] G4_FERRIC_OXIDE  # scripted group (container) (typed FeaturePython)
  Dunit = g/cm3
  Dvalue = 5.2
  Group = -> [Fe_element003,O_element038]
  conduct = 2
  density = 1
  expand = 3
  formula = G4_FERRIC_OXIDE
  name = G4_FERRIC_OXIDE
  specific = 4
FEATURE [App::DocumentObjectGroupPython] Fe_element004  label="Fe_element : 1"  # scripted group (container) (typed FeaturePython)
  n = 1
  ref = Fe_element
FEATURE [App::DocumentObjectGroupPython] B_element003  label="B_element : 1"  # scripted group (container) (typed FeaturePython)
  n = 1
  ref = B_element
FEATURE [App::DocumentObjectGroupPython] G4_FERROBORIDE  # scripted group (container) (typed FeaturePython)
  Dunit = g/cm3
  Dvalue = 7.15
  Group = -> [Fe_element004,B_element003]
  conduct = 2
  density = 1
  expand = 3
  formula = G4_FERROBORIDE
  name = G4_FERROBORIDE
  specific = 4
FEATURE [App::DocumentObjectGroupPython] Fe_element005  label="Fe_element : 003"  # scripted group (container) (typed FeaturePython)
  n = 1
  ref = Fe_element
FEATURE [App::DocumentObjectGroupPython] O_element039  label="O_element : 020"  # scripted group (container) (typed FeaturePython)
  n = 1
  ref = O_element
FEATURE [App::DocumentObjectGroupPython] G4_FERROUS_OXIDE  # scripted group (container) (typed FeaturePython)
  Dunit = g/cm3
  Dvalue = 5.7
  Group = -> [Fe_element005,O_element039]
  conduct = 2
  density = 1
  expand = 3
  formula = G4_FERROUS_OXIDE
  name = G4_FERROUS_OXIDE
  specific = 4
FEATURE [App::DocumentObjectGroupPython] H_element040  label="H_element : 0.115"  # scripted group (container) (typed FeaturePython)
  n = 0.108259
FEATURE [App::DocumentObjectGroupPython] N_element017  label="N_element : 0.000"  # scripted group (container) (typed FeaturePython)
  n = 2.7e-05
FEATURE [App::DocumentObjectGroupPython] O_element040  label="O_element : 0.879"  # scripted group (container) (typed FeaturePython)
  n = 0.878636
FEATURE [App::DocumentObjectGroupPython] Na_element007  label="Na_element : 0.000"  # scripted group (container) (typed FeaturePython)
  n = 2.2e-05
FEATURE [App::DocumentObjectGroupPython] S_element011  label="S_element : 0.013"  # scripted group (container) (typed FeaturePython)
  n = 0.012968
FEATURE [App::DocumentObjectGroupPython] Cl_element011  label="Cl_element : 0.000"  # scripted group (container) (typed FeaturePython)
  n = 3.4e-05
FEATURE [App::DocumentObjectGroupPython] Fe_element006  label="Fe_element : 0.000"  # scripted group (container) (typed FeaturePython)
  n = 5.4e-05
FEATURE [App::DocumentObjectGroupPython] G4_FERROUS_SULFATE  # scripted group (container) (typed FeaturePython)
  Dunit = g/cm3
  Dvalue = 1.024
  Group = -> [H_element040,N_element017,O_element040,Na_element007,S_element011,Cl_element011,Fe_element006]
  conduct = 2
  density = 1
  expand = 3
  formula = G4_FERROUS_SULFATE
  name = G4_FERROUS_SULFATE
  specific = 4
FEATURE [App::DocumentObjectGroupPython] C_element043  label="C_element : 0.099"  # scripted group (container) (typed FeaturePython)
  n = 0.099335
FEATURE [App::DocumentObjectGroupPython] F_element007  label="F_element : 0.314"  # scripted group (container) (typed FeaturePython)
  n = 0.314247
FEATURE [App::DocumentObjectGroupPython] Cl_element012  label="Cl_element : 0.586"  # scripted group (container) (typed FeaturePython)
  n = 0.586418
FEATURE [App::DocumentObjectGroupPython] G4_FREON_12  label="G4_FREON-12"  # scripted group (container) (typed FeaturePython)
  Dunit = g/cm3
  Dvalue = 1.12
  Group = -> [C_element043,F_element007,Cl_element012]
  conduct = 2
  density = 1
  expand = 3
  formula = G4_FREON-12
  name = G4_FREON-12
  specific = 4
FEATURE [App::DocumentObjectGroupPython] C_element044  label="C_element : 0.057"  # scripted group (container) (typed FeaturePython)
  n = 0.057245
FEATURE [App::DocumentObjectGroupPython] F_element008  label="F_element : 0.181"  # scripted group (container) (typed FeaturePython)
  n = 0.181096
FEATURE [App::DocumentObjectGroupPython] Br_element001  label="Br_element : 0.762"  # scripted group (container) (typed FeaturePython)
  n = 0.761659
FEATURE [App::DocumentObjectGroupPython] G4_FREON_12B2  label="G4_FREON-12B2"  # scripted group (container) (typed FeaturePython)
  Dunit = g/cm3
  Dvalue = 1.8
  Group = -> [C_element044,F_element008,Br_element001]
  conduct = 2
  density = 1
  expand = 3
  formula = G4_FREON-12B2
  name = G4_FREON-12B2
  specific = 4
FEATURE [App::DocumentObjectGroupPython] C_element045  label="C_element : 0.115"  # scripted group (container) (typed FeaturePython)
  n = 0.114983
FEATURE [App::DocumentObjectGroupPython] F_element009  label="F_element : 0.546"  # scripted group (container) (typed FeaturePython)
  n = 0.545621
FEATURE [App::DocumentObjectGroupPython] Cl_element013  label="Cl_element : 0.339"  # scripted group (container) (typed FeaturePython)
  n = 0.339396
FEATURE [App::DocumentObjectGroupPython] G4_FREON_13  label="G4_FREON-13"  # scripted group (container) (typed FeaturePython)
  Dunit = g/cm3
  Dvalue = 0.95
  Group = -> [C_element045,F_element009,Cl_element013]
  conduct = 2
  density = 1
  expand = 3
  formula = G4_FREON-13
  name = G4_FREON-13
  specific = 4
FEATURE [App::DocumentObjectGroupPython] C_element046  label="C_element : 025"  # scripted group (container) (typed FeaturePython)
  n = 1
  ref = C_element
FEATURE [App::DocumentObjectGroupPython] F_element010  label="F_element : 3"  # scripted group (container) (typed FeaturePython)
  n = 3
  ref = F_element
FEATURE [App::DocumentObjectGroupPython] Br_element002  label="Br_element : 1"  # scripted group (container) (typed FeaturePython)
  n = 1
  ref = Br_element
FEATURE [App::DocumentObjectGroupPython] G4_FREON_13B1  label="G4_FREON-13B1"  # scripted group (container) (typed FeaturePython)
  Dunit = g/cm3
  Dvalue = 1.5
  Group = -> [C_element046,F_element010,Br_element002]
  conduct = 2
  density = 1
  expand = 3
  formula = G4_FREON-13B1
  name = G4_FREON-13B1
  specific = 4
FEATURE [App::DocumentObjectGroupPython] C_element047  label="C_element : 0.061"  # scripted group (container) (typed FeaturePython)
  n = 0.061309
FEATURE [App::DocumentObjectGroupPython] F_element011  label="F_element : 0.291"  # scripted group (container) (typed FeaturePython)
  n = 0.290924
FEATURE [App::DocumentObjectGroupPython] I_element002  label="I_element : 0.648"  # scripted group (container) (typed FeaturePython)
  n = 0.647767
FEATURE [App::DocumentObjectGroupPython] G4_FREON_13I1  label="G4_FREON-13I1"  # scripted group (container) (typed FeaturePython)
  Dunit = g/cm3
  Dvalue = 1.8
  Group = -> [C_element047,F_element011,I_element002]
  conduct = 2
  density = 1
  expand = 3
  formula = G4_FREON-13I1
  name = G4_FREON-13I1
  specific = 4
FEATURE [App::DocumentObjectGroupPython] Gd_element001  label="Gd_element : 2"  # scripted group (container) (typed FeaturePython)
  n = 2
  ref = Gd_element
FEATURE [App::DocumentObjectGroupPython] O_element041  label="O_element : 021"  # scripted group (container) (typed FeaturePython)
  n = 2
  ref = O_element
FEATURE [App::DocumentObjectGroupPython] S_element012  label="S_element : 004"  # scripted group (container) (typed FeaturePython)
  n = 1
  ref = S_element
FEATURE [App::DocumentObjectGroupPython] G4_GADOLINIUM_OXYSULFIDE  # scripted group (container) (typed FeaturePython)
  Dunit = g/cm3
  Dvalue = 7.44
  Group = -> [Gd_element001,O_element041,S_element012]
  conduct = 2
  density = 1
  expand = 3
  formula = G4_GADOLINIUM_OXYSULFIDE
  name = G4_GADOLINIUM_OXYSULFIDE
  specific = 4
FEATURE [App::DocumentObjectGroupPython] Ga_element001  label="Ga_element : 1"  # scripted group (container) (typed FeaturePython)
  n = 1
  ref = Ga_element
FEATURE [App::DocumentObjectGroupPython] As_element001  label="As_element : 1"  # scripted group (container) (typed FeaturePython)
  n = 1
  ref = As_element
FEATURE [App::DocumentObjectGroupPython] G4_GALLIUM_ARSENIDE  # scripted group (container) (typed FeaturePython)
  Dunit = g/cm3
  Dvalue = 5.31
  Group = -> [Ga_element001,As_element001]
  conduct = 2
  density = 1
  expand = 3
  formula = G4_GALLIUM_ARSENIDE
  name = G4_GALLIUM_ARSENIDE
  specific = 4
FEATURE [App::DocumentObjectGroupPython] H_element041  label="H_element : 0.081"  # scripted group (container) (typed FeaturePython)
  n = 0.08118
FEATURE [App::DocumentObjectGroupPython] C_element048  label="C_element : 0.416"  # scripted group (container) (typed FeaturePython)
  n = 0.41606
FEATURE [App::DocumentObjectGroupPython] N_element018  label="N_element : 0.111"  # scripted group (container) (typed FeaturePython)
  n = 0.11124
FEATURE [App::DocumentObjectGroupPython] O_element042  label="O_element : 0.381"  # scripted group (container) (typed FeaturePython)
  n = 0.38064
FEATURE [App::DocumentObjectGroupPython] S_element013  label="S_element : 0.011"  # scripted group (container) (typed FeaturePython)
  n = 0.01088
FEATURE [App::DocumentObjectGroupPython] G4_GEL_PHOTO_EMULSION  # scripted group (container) (typed FeaturePython)
  Dunit = g/cm3
  Dvalue = 1.2914
  Group = -> [H_element041,C_element048,N_element018,O_element042,S_element013]
  conduct = 2
  density = 1
  expand = 3
  formula = G4_GEL_PHOTO_EMULSION
  name = G4_GEL_PHOTO_EMULSION
  specific = 4
FEATURE [App::DocumentObjectGroupPython] B_element004  label="B_element : 0.040"  # scripted group (container) (typed FeaturePython)
  n = 0.0400639
FEATURE [App::DocumentObjectGroupPython] O_element043  label="O_element : 0.540"  # scripted group (container) (typed FeaturePython)
  n = 0.539561
FEATURE [App::DocumentObjectGroupPython] Na_element008  label="Na_element : 0.028"  # scripted group (container) (typed FeaturePython)
  n = 0.0281909
FEATURE [App::DocumentObjectGroupPython] Al_element003  label="Al_element : 0.012"  # scripted group (container) (typed FeaturePython)
  n = 0.011644
FEATURE [App::DocumentObjectGroupPython] Si_element003  label="Si_element : 0.377"  # scripted group (container) (typed FeaturePython)
  n = 0.377219
FEATURE [App::DocumentObjectGroupPython] K_element004  label="K_element : 0.014"  # scripted group (container) (typed FeaturePython)
  n = 0.00332099
FEATURE [App::DocumentObjectGroupPython] G4_Pyrex_Glass  # scripted group (container) (typed FeaturePython)
  Dunit = g/cm3
  Dvalue = 2.23
  Group = -> [B_element004,O_element043,Na_element008,Al_element003,Si_element003,K_element004]
  conduct = 2
  density = 1
  expand = 3
  formula = G4_Pyrex_Glass
  name = G4_Pyrex_Glass
  specific = 4
FEATURE [App::DocumentObjectGroupPython] O_element044  label="O_element : 0.156"  # scripted group (container) (typed FeaturePython)
  n = 0.156453
FEATURE [App::DocumentObjectGroupPython] Si_element004  label="Si_element : 0.081"  # scripted group (container) (typed FeaturePython)
  n = 0.080866
FEATURE [App::DocumentObjectGroupPython] Ti_element001  label="Ti_element : 0.008"  # scripted group (container) (typed FeaturePython)
  n = 0.008092
FEATURE [App::DocumentObjectGroupPython] As_element002  label="As_element : 0.003"  # scripted group (container) (typed FeaturePython)
  n = 0.002651
FEATURE [App::DocumentObjectGroupPython] Pb_element001  label="Pb_element : 0.752"  # scripted group (container) (typed FeaturePython)
  n = 0.751938
FEATURE [App::DocumentObjectGroupPython] G4_GLASS_LEAD  # scripted group (container) (typed FeaturePython)
  Dunit = g/cm3
  Dvalue = 6.22
  Group = -> [O_element044,Si_element004,Ti_element001,As_element002,Pb_element001]
  conduct = 2
  density = 1
  expand = 3
  formula = G4_GLASS_LEAD
  name = G4_GLASS_LEAD
  specific = 4
FEATURE [App::DocumentObjectGroupPython] O_element045  label="O_element : 0.460"  # scripted group (container) (typed FeaturePython)
  n = 0.4598
FEATURE [App::DocumentObjectGroupPython] Na_element009  label="Na_element : 0.096"  # scripted group (container) (typed FeaturePython)
  n = 0.0964411
FEATURE [App::DocumentObjectGroupPython] Si_element005  label="Si_element : 0.378"  # scripted group (container) (typed FeaturePython)
  n = 0.336553
FEATURE [App::DocumentObjectGroupPython] Ca_element011  label="Ca_element : 0.107"  # scripted group (container) (typed FeaturePython)
  n = 0.107205
FEATURE [App::DocumentObjectGroupPython] G4_GLASS_PLATE  # scripted group (container) (typed FeaturePython)
  Dunit = g/cm3
  Dvalue = 2.4
  Group = -> [O_element045,Na_element009,Si_element005,Ca_element011]
  conduct = 2
  density = 1
  expand = 3
  formula = G4_GLASS_PLATE
  name = G4_GLASS_PLATE
  specific = 4
FEATURE [App::DocumentObjectGroupPython] C_element049  label="C_element : 026"  # scripted group (container) (typed FeaturePython)
  n = 5
  ref = C_element
FEATURE [App::DocumentObjectGroupPython] H_element042  label="H_element : 021"  # scripted group (container) (typed FeaturePython)
  n = 10
  ref = H_element
FEATURE [App::DocumentObjectGroupPython] N_element019  label="N_element : 2"  # scripted group (container) (typed FeaturePython)
  n = 2
  ref = N_element
FEATURE [App::DocumentObjectGroupPython] O_element046  label="O_element : 022"  # scripted group (container) (typed FeaturePython)
  n = 3
  ref = O_element
FEATURE [App::DocumentObjectGroupPython] G4_GLUTAMINE  # scripted group (container) (typed FeaturePython)
  Dunit = g/cm3
  Dvalue = 1.46
  Group = -> [C_element049,H_element042,N_element019,O_element046]
  conduct = 2
  density = 1
  expand = 3
  formula = G4_GLUTAMINE
  name = G4_GLUTAMINE
  specific = 4
FEATURE [App::DocumentObjectGroupPython] C_element050  label="C_element : 027"  # scripted group (container) (typed FeaturePython)
  n = 3
  ref = C_element
FEATURE [App::DocumentObjectGroupPython] H_element043  label="H_element : 022"  # scripted group (container) (typed FeaturePython)
  n = 8
  ref = H_element
FEATURE [App::DocumentObjectGroupPython] O_element047  label="O_element : 023"  # scripted group (container) (typed FeaturePython)
  n = 3
  ref = O_element
FEATURE [App::DocumentObjectGroupPython] G4_GLYCEROL  # scripted group (container) (typed FeaturePython)
  Dunit = g/cm3
  Dvalue = 1.2613
  Group = -> [C_element050,H_element043,O_element047]
  conduct = 2
  density = 1
  expand = 3
  formula = G4_GLYCEROL
  name = G4_GLYCEROL
  specific = 4
FEATURE [App::DocumentObjectGroupPython] C_element051  label="C_element : 028"  # scripted group (container) (typed FeaturePython)
  n = 5
  ref = C_element
FEATURE [App::DocumentObjectGroupPython] H_element044  label="H_element : 023"  # scripted group (container) (typed FeaturePython)
  n = 5
  ref = H_element
FEATURE [App::DocumentObjectGroupPython] N_element020  label="N_element : 009"  # scripted group (container) (typed FeaturePython)
  n = 5
  ref = N_element
FEATURE [App::DocumentObjectGroupPython] O_element048  label="O_element : 024"  # scripted group (container) (typed FeaturePython)
  n = 1
  ref = O_element
FEATURE [App::DocumentObjectGroupPython] G4_GUANINE  # scripted group (container) (typed FeaturePython)
  Dunit = g/cm3
  Dvalue = 2.2
  Group = -> [C_element051,H_element044,N_element020,O_element048]
  conduct = 2
  density = 1
  expand = 3
  formula = G4_GUANINE
  name = G4_GUANINE
  specific = 4
FEATURE [App::DocumentObjectGroupPython] Ca_element012  label="Ca_element : 006"  # scripted group (container) (typed FeaturePython)
  n = 1
  ref = Ca_element
FEATURE [App::DocumentObjectGroupPython] S_element014  label="S_element : 005"  # scripted group (container) (typed FeaturePython)
  n = 1
  ref = S_element
FEATURE [App::DocumentObjectGroupPython] O_element049  label="O_element : 6"  # scripted group (container) (typed FeaturePython)
  n = 6
  ref = O_element
FEATURE [App::DocumentObjectGroupPython] H_element045  label="H_element : 024"  # scripted group (container) (typed FeaturePython)
  n = 4
  ref = H_element
FEATURE [App::DocumentObjectGroupPython] G4_GYPSUM  # scripted group (container) (typed FeaturePython)
  Dunit = g/cm3
  Dvalue = 2.32
  Group = -> [Ca_element012,S_element014,O_element049,H_element045]
  conduct = 2
  density = 1
  expand = 3
  formula = G4_GYPSUM
  name = G4_GYPSUM
  specific = 4
FEATURE [App::DocumentObjectGroupPython] C_element052  label="C_element : 7"  # scripted group (container) (typed FeaturePython)
  n = 7
  ref = C_element
FEATURE [App::DocumentObjectGroupPython] H_element046  label="H_element : 16"  # scripted group (container) (typed FeaturePython)
  n = 16
  ref = H_element
FEATURE [App::DocumentObjectGroupPython] G4_N_HEPTANE  label="G4_N-HEPTANE"  # scripted group (container) (typed FeaturePython)
  Dunit = g/cm3
  Dvalue = 0.68376
  Group = -> [C_element052,H_element046]
  conduct = 2
  density = 1
  expand = 3
  formula = G4_N-HEPTANE
  name = G4_N-HEPTANE
  specific = 4
FEATURE [App::DocumentObjectGroupPython] C_element053  label="C_element : 029"  # scripted group (container) (typed FeaturePython)
  n = 6
  ref = C_element
FEATURE [App::DocumentObjectGroupPython] H_element047  label="H_element : 14"  # scripted group (container) (typed FeaturePython)
  n = 14
  ref = H_element
FEATURE [App::DocumentObjectGroupPython] G4_N_HEXANE  label="G4_N-HEXANE"  # scripted group (container) (typed FeaturePython)
  Dunit = g/cm3
  Dvalue = 0.6603
  Group = -> [C_element053,H_element047]
  conduct = 2
  density = 1
  expand = 3
  formula = G4_N-HEXANE
  name = G4_N-HEXANE
  specific = 4
FEATURE [App::DocumentObjectGroupPython] C_element054  label="C_element : 22"  # scripted group (container) (typed FeaturePython)
  n = 22
  ref = C_element
FEATURE [App::DocumentObjectGroupPython] H_element048  label="H_element : 025"  # scripted group (container) (typed FeaturePython)
  n = 10
  ref = H_element
FEATURE [App::DocumentObjectGroupPython] N_element021  label="N_element : 010"  # scripted group (container) (typed FeaturePython)
  n = 2
  ref = N_element
FEATURE [App::DocumentObjectGroupPython] O_element050  label="O_element : 025"  # scripted group (container) (typed FeaturePython)
  n = 5
  ref = O_element
FEATURE [App::DocumentObjectGroupPython] G4_KAPTON  # scripted group (container) (typed FeaturePython)
  Dunit = g/cm3
  Dvalue = 1.42
  Group = -> [C_element054,H_element048,N_element021,O_element050]
  conduct = 2
  density = 1
  expand = 3
  formula = G4_KAPTON
  name = G4_KAPTON
  specific = 4
FEATURE [App::DocumentObjectGroupPython] La_element001  label="La_element : 1"  # scripted group (container) (typed FeaturePython)
  n = 1
  ref = La_element
FEATURE [App::DocumentObjectGroupPython] Br_element003  label="Br_element : 002"  # scripted group (container) (typed FeaturePython)
  n = 1
  ref = Br_element
FEATURE [App::DocumentObjectGroupPython] O_element051  label="O_element : 026"  # scripted group (container) (typed FeaturePython)
  n = 1
  ref = O_element
FEATURE [App::DocumentObjectGroupPython] G4_LANTHANUM_OXYBROMIDE  # scripted group (container) (typed FeaturePython)
  Dunit = g/cm3
  Dvalue = 6.28
  Group = -> [La_element001,Br_element003,O_element051]
  conduct = 2
  density = 1
  expand = 3
  formula = G4_LANTHANUM_OXYBROMIDE
  name = G4_LANTHANUM_OXYBROMIDE
  specific = 4
FEATURE [App::DocumentObjectGroupPython] La_element002  label="La_element : 2"  # scripted group (container) (typed FeaturePython)
  n = 2
  ref = La_element
FEATURE [App::DocumentObjectGroupPython] O_element052  label="O_element : 027"  # scripted group (container) (typed FeaturePython)
  n = 2
  ref = O_element
FEATURE [App::DocumentObjectGroupPython] S_element015  label="S_element : 006"  # scripted group (container) (typed FeaturePython)
  n = 1
  ref = S_element
FEATURE [App::DocumentObjectGroupPython] G4_LANTHANUM_OXYSULFIDE  # scripted group (container) (typed FeaturePython)
  Dunit = g/cm3
  Dvalue = 5.86
  Group = -> [La_element002,O_element052,S_element015]
  conduct = 2
  density = 1
  expand = 3
  formula = G4_LANTHANUM_OXYSULFIDE
  name = G4_LANTHANUM_OXYSULFIDE
  specific = 4
FEATURE [App::DocumentObjectGroupPython] O_element053  label="O_element : 0.072"  # scripted group (container) (typed FeaturePython)
  n = 0.071682
FEATURE [App::DocumentObjectGroupPython] Pb_element002  label="Pb_element : 0.928"  # scripted group (container) (typed FeaturePython)
  n = 0.928318
FEATURE [App::DocumentObjectGroupPython] G4_LEAD_OXIDE  # scripted group (container) (typed FeaturePython)
  Dunit = g/cm3
  Dvalue = 9.53
  Group = -> [O_element053,Pb_element002]
  conduct = 2
  density = 1
  expand = 3
  formula = G4_LEAD_OXIDE
  name = G4_LEAD_OXIDE
  specific = 4
FEATURE [App::DocumentObjectGroupPython] Li_element001  label="Li_element : 1"  # scripted group (container) (typed FeaturePython)
  n = 1
  ref = Li_element
FEATURE [App::DocumentObjectGroupPython] N_element022  label="N_element : 011"  # scripted group (container) (typed FeaturePython)
  n = 1
  ref = N_element
FEATURE [App::DocumentObjectGroupPython] H_element049  label="H_element : 026"  # scripted group (container) (typed FeaturePython)
  n = 2
  ref = H_element
FEATURE [App::DocumentObjectGroupPython] G4_LITHIUM_AMIDE  # scripted group (container) (typed FeaturePython)
  Dunit = g/cm3
  Dvalue = 1.178
  Group = -> [Li_element001,N_element022,H_element049]
  conduct = 2
  density = 1
  expand = 3
  formula = G4_LITHIUM_AMIDE
  name = G4_LITHIUM_AMIDE
  specific = 4
FEATURE [App::DocumentObjectGroupPython] Li_element002  label="Li_element : 2"  # scripted group (container) (typed FeaturePython)
  n = 2
  ref = Li_element
FEATURE [App::DocumentObjectGroupPython] C_element055  label="C_element : 030"  # scripted group (container) (typed FeaturePython)
  n = 1
  ref = C_element
FEATURE [App::DocumentObjectGroupPython] O_element054  label="O_element : 028"  # scripted group (container) (typed FeaturePython)
  n = 3
  ref = O_element
FEATURE [App::DocumentObjectGroupPython] G4_LITHIUM_CARBONATE  # scripted group (container) (typed FeaturePython)
  Dunit = g/cm3
  Dvalue = 2.11
  Group = -> [Li_element002,C_element055,O_element054]
  conduct = 2
  density = 1
  expand = 3
  formula = G4_LITHIUM_CARBONATE
  name = G4_LITHIUM_CARBONATE
  specific = 4
FEATURE [App::DocumentObjectGroupPython] Li_element003  label="Li_element : 003"  # scripted group (container) (typed FeaturePython)
  n = 1
  ref = Li_element
FEATURE [App::DocumentObjectGroupPython] F_element012  label="F_element : 004"  # scripted group (container) (typed FeaturePython)
  n = 1
  ref = F_element
FEATURE [App::DocumentObjectGroupPython] G4_LITHIUM_FLUORIDE  # scripted group (container) (typed FeaturePython)
  Dunit = g/cm3
  Dvalue = 2.635
  Group = -> [Li_element003,F_element012]
  conduct = 2
  density = 1
  expand = 3
  formula = G4_LITHIUM_FLUORIDE
  name = G4_LITHIUM_FLUORIDE
  specific = 4
FEATURE [App::DocumentObjectGroupPython] Li_element004  label="Li_element : 004"  # scripted group (container) (typed FeaturePython)
  n = 1
  ref = Li_element
FEATURE [App::DocumentObjectGroupPython] H_element050  label="H_element : 027"  # scripted group (container) (typed FeaturePython)
  n = 1
  ref = H_element
FEATURE [App::DocumentObjectGroupPython] G4_LITHIUM_HYDRIDE  # scripted group (container) (typed FeaturePython)
  Dunit = g/cm3
  Dvalue = 0.82
  Group = -> [Li_element004,H_element050]
  conduct = 2
  density = 1
  expand = 3
  formula = G4_LITHIUM_HYDRIDE
  name = G4_LITHIUM_HYDRIDE
  specific = 4
FEATURE [App::DocumentObjectGroupPython] Li_element005  label="Li_element : 005"  # scripted group (container) (typed FeaturePython)
  n = 1
  ref = Li_element
FEATURE [App::DocumentObjectGroupPython] I_element003  label="I_element : 002"  # scripted group (container) (typed FeaturePython)
  n = 1
  ref = I_element
FEATURE [App::DocumentObjectGroupPython] G4_LITHIUM_IODIDE  # scripted group (container) (typed FeaturePython)
  Dunit = g/cm3
  Dvalue = 3.494
  Group = -> [Li_element005,I_element003]
  conduct = 2
  density = 1
  expand = 3
  formula = G4_LITHIUM_IODIDE
  name = G4_LITHIUM_IODIDE
  specific = 4
FEATURE [App::DocumentObjectGroupPython] Li_element006  label="Li_element : 006"  # scripted group (container) (typed FeaturePython)
  n = 2
  ref = Li_element
FEATURE [App::DocumentObjectGroupPython] O_element055  label="O_element : 029"  # scripted group (container) (typed FeaturePython)
  n = 1
  ref = O_element
FEATURE [App::DocumentObjectGroupPython] G4_LITHIUM_OXIDE  # scripted group (container) (typed FeaturePython)
  Dunit = g/cm3
  Dvalue = 2.013
  Group = -> [Li_element006,O_element055]
  conduct = 2
  density = 1
  expand = 3
  formula = G4_LITHIUM_OXIDE
  name = G4_LITHIUM_OXIDE
  specific = 4
FEATURE [App::DocumentObjectGroupPython] Li_element007  label="Li_element : 007"  # scripted group (container) (typed FeaturePython)
  n = 2
  ref = Li_element
FEATURE [App::DocumentObjectGroupPython] B_element005  label="B_element : 005"  # scripted group (container) (typed FeaturePython)
  n = 4
  ref = B_element
FEATURE [App::DocumentObjectGroupPython] O_element056  label="O_element : 7"  # scripted group (container) (typed FeaturePython)
  n = 7
  ref = O_element
FEATURE [App::DocumentObjectGroupPython] G4_LITHIUM_TETRABORATE  # scripted group (container) (typed FeaturePython)
  Dunit = g/cm3
  Dvalue = 2.44
  Group = -> [Li_element007,B_element005,O_element056]
  conduct = 2
  density = 1
  expand = 3
  formula = G4_LITHIUM_TETRABORATE
  name = G4_LITHIUM_TETRABORATE
  specific = 4
FEATURE [App::DocumentObjectGroupPython] H_element051  label="H_element : 0.105"  # scripted group (container) (typed FeaturePython)
  n = 0.105
FEATURE [App::DocumentObjectGroupPython] C_element056  label="C_element : 0.083"  # scripted group (container) (typed FeaturePython)
  n = 0.083
FEATURE [App::DocumentObjectGroupPython] N_element023  label="N_element : 0.023"  # scripted group (container) (typed FeaturePython)
  n = 0.023
FEATURE [App::DocumentObjectGroupPython] O_element057  label="O_element : 0.779"  # scripted group (container) (typed FeaturePython)
  n = 0.779
FEATURE [App::DocumentObjectGroupPython] Na_element010  label="Na_element : 0.097"  # scripted group (container) (typed FeaturePython)
  n = 0.002
FEATURE [App::DocumentObjectGroupPython] P_element006  label="P_element : 0.105"  # scripted group (container) (typed FeaturePython)
  n = 0.001
FEATURE [App::DocumentObjectGroupPython] S_element016  label="S_element : 0.017"  # scripted group (container) (typed FeaturePython)
  n = 0.002
FEATURE [App::DocumentObjectGroupPython] Cl_element014  label="Cl_element : 0.587"  # scripted group (container) (typed FeaturePython)
  n = 0.003
FEATURE [App::DocumentObjectGroupPython] K_element005  label="K_element : 0.015"  # scripted group (container) (typed FeaturePython)
  n = 0.002
FEATURE [App::DocumentObjectGroupPython] G4_LUNG_ICRP  # scripted group (container) (typed FeaturePython)
  Dunit = g/cm3
  Dvalue = 1.04
  Group = -> [H_element051,C_element056,N_element023,O_element057,Na_element010,P_element006,S_element016,Cl_element014,K_element005]
  conduct = 2
  density = 1
  expand = 3
  formula = G4_LUNG_ICRP
  name = G4_LUNG_ICRP
  specific = 4
FEATURE [App::DocumentObjectGroupPython] H_element052  label="H_element : 0.116"  # scripted group (container) (typed FeaturePython)
  n = 0.114318
FEATURE [App::DocumentObjectGroupPython] C_element057  label="C_element : 0.656"  # scripted group (container) (typed FeaturePython)
  n = 0.655824
FEATURE [App::DocumentObjectGroupPython] O_element058  label="O_element : 0.092"  # scripted group (container) (typed FeaturePython)
  n = 0.0921831
FEATURE [App::DocumentObjectGroupPython] Mg_element004  label="Mg_element : 0.135"  # scripted group (container) (typed FeaturePython)
  n = 0.134792
FEATURE [App::DocumentObjectGroupPython] Ca_element013  label="Ca_element : 0.003"  # scripted group (container) (typed FeaturePython)
  n = 0.002883
FEATURE [App::DocumentObjectGroupPython] G4_M3_WAX  # scripted group (container) (typed FeaturePython)
  Dunit = g/cm3
  Dvalue = 1.05
  Group = -> [H_element052,C_element057,O_element058,Mg_element004,Ca_element013]
  conduct = 2
  density = 1
  expand = 3
  formula = G4_M3_WAX
  name = G4_M3_WAX
  specific = 4
FEATURE [App::DocumentObjectGroupPython] Mg_element005  label="Mg_element : 1"  # scripted group (container) (typed FeaturePython)
  n = 1
  ref = Mg_element
FEATURE [App::DocumentObjectGroupPython] C_element058  label="C_element : 031"  # scripted group (container) (typed FeaturePython)
  n = 1
  ref = C_element
FEATURE [App::DocumentObjectGroupPython] O_element059  label="O_element : 030"  # scripted group (container) (typed FeaturePython)
  n = 3
  ref = O_element
FEATURE [App::DocumentObjectGroupPython] G4_MAGNESIUM_CARBONATE  # scripted group (container) (typed FeaturePython)
  Dunit = g/cm3
  Dvalue = 2.958
  Group = -> [Mg_element005,C_element058,O_element059]
  conduct = 2
  density = 1
  expand = 3
  formula = G4_MAGNESIUM_CARBONATE
  name = G4_MAGNESIUM_CARBONATE
  specific = 4
FEATURE [App::DocumentObjectGroupPython] Mg_element006  label="Mg_element : 002"  # scripted group (container) (typed FeaturePython)
  n = 1
  ref = Mg_element
FEATURE [App::DocumentObjectGroupPython] F_element013  label="F_element : 005"  # scripted group (container) (typed FeaturePython)
  n = 2
  ref = F_element
FEATURE [App::DocumentObjectGroupPython] G4_MAGNESIUM_FLUORIDE  # scripted group (container) (typed FeaturePython)
  Dunit = g/cm3
  Dvalue = 3
  Group = -> [Mg_element006,F_element013]
  conduct = 2
  density = 1
  expand = 3
  formula = G4_MAGNESIUM_FLUORIDE
  name = G4_MAGNESIUM_FLUORIDE
  specific = 4
FEATURE [App::DocumentObjectGroupPython] Mg_element007  label="Mg_element : 003"  # scripted group (container) (typed FeaturePython)
  n = 1
  ref = Mg_element
FEATURE [App::DocumentObjectGroupPython] O_element060  label="O_element : 031"  # scripted group (container) (typed FeaturePython)
  n = 1
  ref = O_element
FEATURE [App::DocumentObjectGroupPython] G4_MAGNESIUM_OXIDE  # scripted group (container) (typed FeaturePython)
  Dunit = g/cm3
  Dvalue = 3.58
  Group = -> [Mg_element007,O_element060]
  conduct = 2
  density = 1
  expand = 3
  formula = G4_MAGNESIUM_OXIDE
  name = G4_MAGNESIUM_OXIDE
  specific = 4
FEATURE [App::DocumentObjectGroupPython] Mg_element008  label="Mg_element : 004"  # scripted group (container) (typed FeaturePython)
  n = 1
  ref = Mg_element
FEATURE [App::DocumentObjectGroupPython] B_element006  label="B_element : 006"  # scripted group (container) (typed FeaturePython)
  n = 4
  ref = B_element
FEATURE [App::DocumentObjectGroupPython] O_element061  label="O_element : 032"  # scripted group (container) (typed FeaturePython)
  n = 7
  ref = O_element
FEATURE [App::DocumentObjectGroupPython] G4_MAGNESIUM_TETRABORATE  # scripted group (container) (typed FeaturePython)
  Dunit = g/cm3
  Dvalue = 2.53
  Group = -> [Mg_element008,B_element006,O_element061]
  conduct = 2
  density = 1
  expand = 3
  formula = G4_MAGNESIUM_TETRABORATE
  name = G4_MAGNESIUM_TETRABORATE
  specific = 4
FEATURE [App::DocumentObjectGroupPython] Hg_element001  label="Hg_element : 1"  # scripted group (container) (typed FeaturePython)
  n = 1
  ref = Hg_element
FEATURE [App::DocumentObjectGroupPython] I_element004  label="I_element : 2"  # scripted group (container) (typed FeaturePython)
  n = 2
  ref = I_element
FEATURE [App::DocumentObjectGroupPython] G4_MERCURIC_IODIDE  # scripted group (container) (typed FeaturePython)
  Dunit = g/cm3
  Dvalue = 6.36
  Group = -> [Hg_element001,I_element004]
  conduct = 2
  density = 1
  expand = 3
  formula = G4_MERCURIC_IODIDE
  name = G4_MERCURIC_IODIDE
  specific = 4
FEATURE [App::DocumentObjectGroupPython] C_element059  label="C_element : 032"  # scripted group (container) (typed FeaturePython)
  n = 1
  ref = C_element
FEATURE [App::DocumentObjectGroupPython] H_element053  label="H_element : 028"  # scripted group (container) (typed FeaturePython)
  n = 4
  ref = H_element
FEATURE [App::DocumentObjectGroupPython] G4_METHANE  # scripted group (container) (typed FeaturePython)
  Dunit = g/cm3
  Dvalue = 0.000667151
  Group = -> [C_element059,H_element053]
  conduct = 2
  density = 1
  expand = 3
  formula = G4_METHANE
  name = G4_METHANE
  specific = 4
FEATURE [App::DocumentObjectGroupPython] C_element060  label="C_element : 033"  # scripted group (container) (typed FeaturePython)
  n = 1
  ref = C_element
FEATURE [App::DocumentObjectGroupPython] H_element054  label="H_element : 029"  # scripted group (container) (typed FeaturePython)
  n = 4
  ref = H_element
FEATURE [App::DocumentObjectGroupPython] O_element062  label="O_element : 033"  # scripted group (container) (typed FeaturePython)
  n = 1
  ref = O_element
FEATURE [App::DocumentObjectGroupPython] G4_METHANOL  # scripted group (container) (typed FeaturePython)
  Dunit = g/cm3
  Dvalue = 0.7914
  Group = -> [C_element060,H_element054,O_element062]
  conduct = 2
  density = 1
  expand = 3
  formula = G4_METHANOL
  name = G4_METHANOL
  specific = 4
FEATURE [App::DocumentObjectGroupPython] H_element055  label="H_element : 0.134"  # scripted group (container) (typed FeaturePython)
  n = 0.13404
FEATURE [App::DocumentObjectGroupPython] C_element061  label="C_element : 0.778"  # scripted group (container) (typed FeaturePython)
  n = 0.77796
FEATURE [App::DocumentObjectGroupPython] O_element063  label="O_element : 0.035"  # scripted group (container) (typed FeaturePython)
  n = 0.03502
FEATURE [App::DocumentObjectGroupPython] Mg_element009  label="Mg_element : 0.039"  # scripted group (container) (typed FeaturePython)
  n = 0.038594
FEATURE [App::DocumentObjectGroupPython] Ti_element002  label="Ti_element : 0.014"  # scripted group (container) (typed FeaturePython)
  n = 0.014386
FEATURE [App::DocumentObjectGroupPython] G4_MIX_D_WAX  # scripted group (container) (typed FeaturePython)
  Dunit = g/cm3
  Dvalue = 0.99
  Group = -> [H_element055,C_element061,O_element063,Mg_element009,Ti_element002]
  conduct = 2
  density = 1
  expand = 3
  formula = G4_MIX_D_WAX
  name = G4_MIX_D_WAX
  specific = 4
FEATURE [App::DocumentObjectGroupPython] H_element056  label="H_element : 0.135"  # scripted group (container) (typed FeaturePython)
  n = 0.081192
FEATURE [App::DocumentObjectGroupPython] C_element062  label="C_element : 0.583"  # scripted group (container) (typed FeaturePython)
  n = 0.583442
FEATURE [App::DocumentObjectGroupPython] N_element024  label="N_element : 0.018"  # scripted group (container) (typed FeaturePython)
  n = 0.017798
FEATURE [App::DocumentObjectGroupPython] O_element064  label="O_element : 0.186"  # scripted group (container) (typed FeaturePython)
  n = 0.186381
FEATURE [App::DocumentObjectGroupPython] Mg_element010  label="Mg_element : 0.130"  # scripted group (container) (typed FeaturePython)
  n = 0.130287
FEATURE [App::DocumentObjectGroupPython] Cl_element015  label="Cl_element : 0.588"  # scripted group (container) (typed FeaturePython)
  n = 0.0009
FEATURE [App::DocumentObjectGroupPython] G4_MS20_TISSUE  # scripted group (container) (typed FeaturePython)
  Dunit = g/cm3
  Dvalue = 1
  Group = -> [H_element056,C_element062,N_element024,O_element064,Mg_element010,Cl_element015]
  conduct = 2
  density = 1
  expand = 3
  formula = G4_MS20_TISSUE
  name = G4_MS20_TISSUE
  specific = 4
FEATURE [App::DocumentObjectGroupPython] H_element057  label="H_element : 0.136"  # scripted group (container) (typed FeaturePython)
  n = 0.102
FEATURE [App::DocumentObjectGroupPython] C_element063  label="C_element : 0.143"  # scripted group (container) (typed FeaturePython)
  n = 0.143
FEATURE [App::DocumentObjectGroupPython] N_element025  label="N_element : 0.034"  # scripted group (container) (typed FeaturePython)
  n = 0.034
FEATURE [App::DocumentObjectGroupPython] O_element065  label="O_element : 0.710"  # scripted group (container) (typed FeaturePython)
  n = 0.71
FEATURE [App::DocumentObjectGroupPython] Na_element011  label="Na_element : 0.098"  # scripted group (container) (typed FeaturePython)
  n = 0.001
FEATURE [App::DocumentObjectGroupPython] P_element007  label="P_element : 0.002"  # scripted group (container) (typed FeaturePython)
  n = 0.002
FEATURE [App::DocumentObjectGroupPython] S_element017  label="S_element : 0.018"  # scripted group (container) (typed FeaturePython)
  n = 0.003
FEATURE [App::DocumentObjectGroupPython] Cl_element016  label="Cl_element : 0.589"  # scripted group (container) (typed FeaturePython)
  n = 0.001
FEATURE [App::DocumentObjectGroupPython] K_element006  label="K_element : 0.004"  # scripted group (container) (typed FeaturePython)
  n = 0.004
FEATURE [App::DocumentObjectGroupPython] G4_MUSCLE_SKELETAL_ICRP  # scripted group (container) (typed FeaturePython)
  Dunit = g/cm3
  Dvalue = 1.05
  Group = -> [H_element057,C_element063,N_element025,O_element065,Na_element011,P_element007,S_element017,Cl_element016,K_element006]
  conduct = 2
  density = 1
  expand = 3
  formula = G4_MUSCLE_SKELETAL_ICRP
  name = G4_MUSCLE_SKELETAL_ICRP
  specific = 4
FEATURE [App::DocumentObjectGroupPython] H_element058  label="H_element : 0.137"  # scripted group (container) (typed FeaturePython)
  n = 0.102102
FEATURE [App::DocumentObjectGroupPython] C_element064  label="C_element : 0.123"  # scripted group (container) (typed FeaturePython)
  n = 0.123123
FEATURE [App::DocumentObjectGroupPython] N_element026  label="N_element : 0.756"  # scripted group (container) (typed FeaturePython)
  n = 0.035035
FEATURE [App::DocumentObjectGroupPython] O_element066  label="O_element : 0.730"  # scripted group (container) (typed FeaturePython)
  n = 0.72973
FEATURE [App::DocumentObjectGroupPython] Na_element012  label="Na_element : 0.099"  # scripted group (container) (typed FeaturePython)
  n = 0.001001
FEATURE [App::DocumentObjectGroupPython] P_element008  label="P_element : 0.106"  # scripted group (container) (typed FeaturePython)
  n = 0.002002
FEATURE [App::DocumentObjectGroupPython] S_element018  label="S_element : 0.019"  # scripted group (container) (typed FeaturePython)
  n = 0.004004
FEATURE [App::DocumentObjectGroupPython] K_element007  label="K_element : 0.016"  # scripted group (container) (typed FeaturePython)
  n = 0.003003
FEATURE [App::DocumentObjectGroupPython] G4_MUSCLE_STRIATED_ICRU  # scripted group (container) (typed FeaturePython)
  Dunit = g/cm3
  Dvalue = 1.04
  Group = -> [H_element058,C_element064,N_element026,O_element066,Na_element012,P_element008,S_element018,K_element007]
  conduct = 2
  density = 1
  expand = 3
  formula = G4_MUSCLE_STRIATED_ICRU
  name = G4_MUSCLE_STRIATED_ICRU
  specific = 4
FEATURE [App::DocumentObjectGroupPython] H_element059  label="H_element : 0.098"  # scripted group (container) (typed FeaturePython)
  n = 0.0982341
FEATURE [App::DocumentObjectGroupPython] C_element065  label="C_element : 0.156"  # scripted group (container) (typed FeaturePython)
  n = 0.156214
FEATURE [App::DocumentObjectGroupPython] N_element027  label="N_element : 0.757"  # scripted group (container) (typed FeaturePython)
  n = 0.035451
FEATURE [App::DocumentObjectGroupPython] O_element067  label="O_element : 0.880"  # scripted group (container) (typed FeaturePython)
  n = 0.710101
FEATURE [App::DocumentObjectGroupPython] G4_MUSCLE_WITH_SUCROSE  # scripted group (container) (typed FeaturePython)
  Dunit = g/cm3
  Dvalue = 1.11
  Group = -> [H_element059,C_element065,N_element027,O_element067]
  conduct = 2
  density = 1
  expand = 3
  formula = G4_MUSCLE_WITH_SUCROSE
  name = G4_MUSCLE_WITH_SUCROSE
  specific = 4
FEATURE [App::DocumentObjectGroupPython] H_element060  label="H_element : 0.138"  # scripted group (container) (typed FeaturePython)
  n = 0.101969
FEATURE [App::DocumentObjectGroupPython] C_element066  label="C_element : 0.120"  # scripted group (container) (typed FeaturePython)
  n = 0.120058
FEATURE [App::DocumentObjectGroupPython] N_element028  label="N_element : 0.758"  # scripted group (container) (typed FeaturePython)
  n = 0.035451
FEATURE [App::DocumentObjectGroupPython] O_element068  label="O_element : 0.743"  # scripted group (container) (typed FeaturePython)
  n = 0.742522
FEATURE [App::DocumentObjectGroupPython] G4_MUSCLE_WITHOUT_SUCROSE  # scripted group (container) (typed FeaturePython)
  Dunit = g/cm3
  Dvalue = 1.07
  Group = -> [H_element060,C_element066,N_element028,O_element068]
  conduct = 2
  density = 1
  expand = 3
  formula = G4_MUSCLE_WITHOUT_SUCROSE
  name = G4_MUSCLE_WITHOUT_SUCROSE
  specific = 4
FEATURE [App::DocumentObjectGroupPython] C_element067  label="C_element : 10"  # scripted group (container) (typed FeaturePython)
  n = 10
  ref = C_element
FEATURE [App::DocumentObjectGroupPython] H_element061  label="H_element : 030"  # scripted group (container) (typed FeaturePython)
  n = 8
  ref = H_element
FEATURE [App::DocumentObjectGroupPython] G4_NAPHTHALENE  # scripted group (container) (typed FeaturePython)
  Dunit = g/cm3
  Dvalue = 1.145
  Group = -> [C_element067,H_element061]
  conduct = 2
  density = 1
  expand = 3
  formula = G4_NAPHTHALENE
  name = G4_NAPHTHALENE
  specific = 4
FEATURE [App::DocumentObjectGroupPython] C_element068  label="C_element : 034"  # scripted group (container) (typed FeaturePython)
  n = 6
  ref = C_element
FEATURE [App::DocumentObjectGroupPython] H_element062  label="H_element : 031"  # scripted group (container) (typed FeaturePython)
  n = 5
  ref = H_element
FEATURE [App::DocumentObjectGroupPython] N_element029  label="N_element : 012"  # scripted group (container) (typed FeaturePython)
  n = 1
  ref = N_element
FEATURE [App::DocumentObjectGroupPython] O_element069  label="O_element : 034"  # scripted group (container) (typed FeaturePython)
  n = 2
  ref = O_element
FEATURE [App::DocumentObjectGroupPython] G4_NITROBENZENE  # scripted group (container) (typed FeaturePython)
  Dunit = g/cm3
  Dvalue = 1.19867
  Group = -> [C_element068,H_element062,N_element029,O_element069]
  conduct = 2
  density = 1
  expand = 3
  formula = G4_NITROBENZENE
  name = G4_NITROBENZENE
  specific = 4
FEATURE [App::DocumentObjectGroupPython] N_element030  label="N_element : 013"  # scripted group (container) (typed FeaturePython)
  n = 2
  ref = N_element
FEATURE [App::DocumentObjectGroupPython] O_element070  label="O_element : 035"  # scripted group (container) (typed FeaturePython)
  n = 1
  ref = O_element
FEATURE [App::DocumentObjectGroupPython] G4_NITROUS_OXIDE  # scripted group (container) (typed FeaturePython)
  Dunit = g/cm3
  Dvalue = 0.00183094
  Group = -> [N_element030,O_element070]
  conduct = 2
  density = 1
  expand = 3
  formula = G4_NITROUS_OXIDE
  name = G4_NITROUS_OXIDE
  specific = 4
FEATURE [App::DocumentObjectGroupPython] H_element063  label="H_element : 0.104"  # scripted group (container) (typed FeaturePython)
  n = 0.103509
FEATURE [App::DocumentObjectGroupPython] C_element069  label="C_element : 0.648"  # scripted group (container) (typed FeaturePython)
  n = 0.648416
FEATURE [App::DocumentObjectGroupPython] N_element031  label="N_element : 0.100"  # scripted group (container) (typed FeaturePython)
  n = 0.0995361
FEATURE [App::DocumentObjectGroupPython] O_element071  label="O_element : 0.149"  # scripted group (container) (typed FeaturePython)
  n = 0.148539
FEATURE [App::DocumentObjectGroupPython] G4_NYLON_8062  label="G4_NYLON-8062"  # scripted group (container) (typed FeaturePython)
  Dunit = g/cm3
  Dvalue = 1.08
  Group = -> [H_element063,C_element069,N_element031,O_element071]
  conduct = 2
  density = 1
  expand = 3
  formula = G4_NYLON-8062
  name = G4_NYLON-8062
  specific = 4
FEATURE [App::DocumentObjectGroupPython] C_element070  label="C_element : 035"  # scripted group (container) (typed FeaturePython)
  n = 6
  ref = C_element
FEATURE [App::DocumentObjectGroupPython] H_element064  label="H_element : 11"  # scripted group (container) (typed FeaturePython)
  n = 11
  ref = H_element
FEATURE [App::DocumentObjectGroupPython] N_element032  label="N_element : 014"  # scripted group (container) (typed FeaturePython)
  n = 1
  ref = N_element
FEATURE [App::DocumentObjectGroupPython] O_element072  label="O_element : 036"  # scripted group (container) (typed FeaturePython)
  n = 1
  ref = O_element
FEATURE [App::DocumentObjectGroupPython] G4_NYLON_6_6  label="G4_NYLON-6-6"  # scripted group (container) (typed FeaturePython)
  Dunit = g/cm3
  Dvalue = 1.14
  Group = -> [C_element070,H_element064,N_element032,O_element072]
  conduct = 2
  density = 1
  expand = 3
  formula = G4_NYLON-6-6
  name = G4_NYLON-6-6
  specific = 4
FEATURE [App::DocumentObjectGroupPython] H_element065  label="H_element : 0.139"  # scripted group (container) (typed FeaturePython)
  n = 0.107062
FEATURE [App::DocumentObjectGroupPython] C_element071  label="C_element : 0.680"  # scripted group (container) (typed FeaturePython)
  n = 0.680449
FEATURE [App::DocumentObjectGroupPython] N_element033  label="N_element : 0.099"  # scripted group (container) (typed FeaturePython)
  n = 0.099189
FEATURE [App::DocumentObjectGroupPython] O_element073  label="O_element : 0.113"  # scripted group (container) (typed FeaturePython)
  n = 0.1133
FEATURE [App::DocumentObjectGroupPython] G4_NYLON_6_10  label="G4_NYLON-6-10"  # scripted group (container) (typed FeaturePython)
  Dunit = g/cm3
  Dvalue = 1.14
  Group = -> [H_element065,C_element071,N_element033,O_element073]
  conduct = 2
  density = 1
  expand = 3
  formula = G4_NYLON-6-10
  name = G4_NYLON-6-10
  specific = 4
FEATURE [App::DocumentObjectGroupPython] H_element066  label="H_element : 0.140"  # scripted group (container) (typed FeaturePython)
  n = 0.115476
FEATURE [App::DocumentObjectGroupPython] C_element072  label="C_element : 0.721"  # scripted group (container) (typed FeaturePython)
  n = 0.720818
FEATURE [App::DocumentObjectGroupPython] N_element034  label="N_element : 0.076"  # scripted group (container) (typed FeaturePython)
  n = 0.0764169
FEATURE [App::DocumentObjectGroupPython] O_element074  label="O_element : 0.087"  # scripted group (container) (typed FeaturePython)
  n = 0.0872889
FEATURE [App::DocumentObjectGroupPython] G4_NYLON_11_RILSAN  label="G4_NYLON-11_RILSAN"  # scripted group (container) (typed FeaturePython)
  Dunit = g/cm3
  Dvalue = 1.425
  Group = -> [H_element066,C_element072,N_element034,O_element074]
  conduct = 2
  density = 1
  expand = 3
  formula = G4_NYLON-11_RILSAN
  name = G4_NYLON-11_RILSAN
  specific = 4
FEATURE [App::DocumentObjectGroupPython] C_element073  label="C_element : 8"  # scripted group (container) (typed FeaturePython)
  n = 8
  ref = C_element
FEATURE [App::DocumentObjectGroupPython] H_element067  label="H_element : 18"  # scripted group (container) (typed FeaturePython)
  n = 18
  ref = H_element
FEATURE [App::DocumentObjectGroupPython] G4_OCTANE  # scripted group (container) (typed FeaturePython)
  Dunit = g/cm3
  Dvalue = 0.7026
  Group = -> [C_element073,H_element067]
  conduct = 2
  density = 1
  expand = 3
  formula = G4_OCTANE
  name = G4_OCTANE
  specific = 4
FEATURE [App::DocumentObjectGroupPython] C_element074  label="C_element : 25"  # scripted group (container) (typed FeaturePython)
  n = 25
  ref = C_element
FEATURE [App::DocumentObjectGroupPython] H_element068  label="H_element : 52"  # scripted group (container) (typed FeaturePython)
  n = 52
  ref = H_element
FEATURE [App::DocumentObjectGroupPython] G4_PARAFFIN  # scripted group (container) (typed FeaturePython)
  Dunit = g/cm3
  Dvalue = 0.93
  Group = -> [C_element074,H_element068]
  conduct = 2
  density = 1
  expand = 3
  formula = G4_PARAFFIN
  name = G4_PARAFFIN
  specific = 4
FEATURE [App::DocumentObjectGroupPython] C_element075  label="C_element : 036"  # scripted group (container) (typed FeaturePython)
  n = 5
  ref = C_element
FEATURE [App::DocumentObjectGroupPython] H_element069  label="H_element : 032"  # scripted group (container) (typed FeaturePython)
  n = 12
  ref = H_element
FEATURE [App::DocumentObjectGroupPython] G4_N_PENTANE  label="G4_N-PENTANE"  # scripted group (container) (typed FeaturePython)
  Dunit = g/cm3
  Dvalue = 0.6262
  Group = -> [C_element075,H_element069]
  conduct = 2
  density = 1
  expand = 3
  formula = G4_N-PENTANE
  name = G4_N-PENTANE
  specific = 4
FEATURE [App::DocumentObjectGroupPython] H_element070  label="H_element : 0.014"  # scripted group (container) (typed FeaturePython)
  n = 0.0141
FEATURE [App::DocumentObjectGroupPython] C_element076  label="C_element : 0.072"  # scripted group (container) (typed FeaturePython)
  n = 0.072261
FEATURE [App::DocumentObjectGroupPython] N_element035  label="N_element : 0.019"  # scripted group (container) (typed FeaturePython)
  n = 0.01932
FEATURE [App::DocumentObjectGroupPython] O_element075  label="O_element : 0.066"  # scripted group (container) (typed FeaturePython)
  n = 0.066101
FEATURE [App::DocumentObjectGroupPython] S_element019  label="S_element : 0.020"  # scripted group (container) (typed FeaturePython)
  n = 0.00189
FEATURE [App::DocumentObjectGroupPython] Br_element004  label="Br_element : 0.349"  # scripted group (container) (typed FeaturePython)
  n = 0.349103
FEATURE [App::DocumentObjectGroupPython] Ag_element001  label="Ag_element : 0.474"  # scripted group (container) (typed FeaturePython)
  n = 0.474105
FEATURE [App::DocumentObjectGroupPython] I_element005  label="I_element : 0.003"  # scripted group (container) (typed FeaturePython)
  n = 0.00312
FEATURE [App::DocumentObjectGroupPython] G4_PHOTO_EMULSION  # scripted group (container) (typed FeaturePython)
  Dunit = g/cm3
  Dvalue = 3.815
  Group = -> [H_element070,C_element076,N_element035,O_element075,S_element019,Br_element004,Ag_element001,I_element005]
  conduct = 2
  density = 1
  expand = 3
  formula = G4_PHOTO_EMULSION
  name = G4_PHOTO_EMULSION
  specific = 4
FEATURE [App::DocumentObjectGroupPython] C_element077  label="C_element : 9"  # scripted group (container) (typed FeaturePython)
  n = 9
  ref = C_element
FEATURE [App::DocumentObjectGroupPython] H_element071  label="H_element : 033"  # scripted group (container) (typed FeaturePython)
  n = 10
  ref = H_element
FEATURE [App::DocumentObjectGroupPython] G4_PLASTIC_SC_VINYLTOLUENE  # scripted group (container) (typed FeaturePython)
  Dunit = g/cm3
  Dvalue = 1.032
  Group = -> [C_element077,H_element071]
  conduct = 2
  density = 1
  expand = 3
  formula = G4_PLASTIC_SC_VINYLTOLUENE
  name = G4_PLASTIC_SC_VINYLTOLUENE
  specific = 4
FEATURE [App::DocumentObjectGroupPython] Pu_element001  label="Pu_element : 1"  # scripted group (container) (typed FeaturePython)
  n = 1
  ref = Pu_element
FEATURE [App::DocumentObjectGroupPython] O_element076  label="O_element : 037"  # scripted group (container) (typed FeaturePython)
  n = 2
  ref = O_element
FEATURE [App::DocumentObjectGroupPython] G4_PLUTONIUM_DIOXIDE  # scripted group (container) (typed FeaturePython)
  Dunit = g/cm3
  Dvalue = 11.46
  Group = -> [Pu_element001,O_element076]
  conduct = 2
  density = 1
  expand = 3
  formula = G4_PLUTONIUM_DIOXIDE
  name = G4_PLUTONIUM_DIOXIDE
  specific = 4
FEATURE [App::DocumentObjectGroupPython] C_element078  label="C_element : 037"  # scripted group (container) (typed FeaturePython)
  n = 3
  ref = C_element
FEATURE [App::DocumentObjectGroupPython] H_element072  label="H_element : 034"  # scripted group (container) (typed FeaturePython)
  n = 3
  ref = H_element
FEATURE [App::DocumentObjectGroupPython] N_element036  label="N_element : 015"  # scripted group (container) (typed FeaturePython)
  n = 1
  ref = N_element
FEATURE [App::DocumentObjectGroupPython] G4_POLYACRYLONITRILE  # scripted group (container) (typed FeaturePython)
  Dunit = g/cm3
  Dvalue = 1.17
  Group = -> [C_element078,H_element072,N_element036]
  conduct = 2
  density = 1
  expand = 3
  formula = G4_POLYACRYLONITRILE
  name = G4_POLYACRYLONITRILE
  specific = 4
FEATURE [App::DocumentObjectGroupPython] C_element079  label="C_element : 16"  # scripted group (container) (typed FeaturePython)
  n = 16
  ref = C_element
FEATURE [App::DocumentObjectGroupPython] H_element073  label="H_element : 035"  # scripted group (container) (typed FeaturePython)
  n = 14
  ref = H_element
FEATURE [App::DocumentObjectGroupPython] O_element077  label="O_element : 038"  # scripted group (container) (typed FeaturePython)
  n = 3
  ref = O_element
FEATURE [App::DocumentObjectGroupPython] G4_POLYCARBONATE  # scripted group (container) (typed FeaturePython)
  Dunit = g/cm3
  Dvalue = 1.2
  Group = -> [C_element079,H_element073,O_element077]
  conduct = 2
  density = 1
  expand = 3
  formula = G4_POLYCARBONATE
  name = G4_POLYCARBONATE
  specific = 4
FEATURE [App::DocumentObjectGroupPython] C_element080  label="C_element : 038"  # scripted group (container) (typed FeaturePython)
  n = 8
  ref = C_element
FEATURE [App::DocumentObjectGroupPython] H_element074  label="H_element : 036"  # scripted group (container) (typed FeaturePython)
  n = 7
  ref = H_element
FEATURE [App::DocumentObjectGroupPython] Cl_element017  label="Cl_element : 007"  # scripted group (container) (typed FeaturePython)
  n = 1
  ref = Cl_element
FEATURE [App::DocumentObjectGroupPython] G4_POLYCHLOROSTYRENE  # scripted group (container) (typed FeaturePython)
  Dunit = g/cm3
  Dvalue = 1.3
  Group = -> [C_element080,H_element074,Cl_element017]
  conduct = 2
  density = 1
  expand = 3
  formula = G4_POLYCHLOROSTYRENE
  name = G4_POLYCHLOROSTYRENE
  specific = 4
FEATURE [App::DocumentObjectGroupPython] C_element081  label="C_element : 039"  # scripted group (container) (typed FeaturePython)
  n = 1
  ref = C_element
FEATURE [App::DocumentObjectGroupPython] H_element075  label="H_element : 037"  # scripted group (container) (typed FeaturePython)
  n = 2
  ref = H_element
FEATURE [App::DocumentObjectGroupPython] G4_POLYETHYLENE  # scripted group (container) (typed FeaturePython)
  Dunit = g/cm3
  Dvalue = 0.94
  Group = -> [C_element081,H_element075]
  conduct = 2
  density = 1
  expand = 3
  formula = G4_POLYETHYLENE
  name = G4_POLYETHYLENE
  specific = 4
FEATURE [App::DocumentObjectGroupPython] C_element082  label="C_element : 040"  # scripted group (container) (typed FeaturePython)
  n = 10
  ref = C_element
FEATURE [App::DocumentObjectGroupPython] H_element076  label="H_element : 038"  # scripted group (container) (typed FeaturePython)
  n = 8
  ref = H_element
FEATURE [App::DocumentObjectGroupPython] O_element078  label="O_element : 039"  # scripted group (container) (typed FeaturePython)
  n = 4
  ref = O_element
FEATURE [App::DocumentObjectGroupPython] G4_MYLAR  # scripted group (container) (typed FeaturePython)
  Dunit = g/cm3
  Dvalue = 1.4
  Group = -> [C_element082,H_element076,O_element078]
  conduct = 2
  density = 1
  expand = 3
  formula = G4_MYLAR
  name = G4_MYLAR
  specific = 4
FEATURE [App::DocumentObjectGroupPython] C_element083  label="C_element : 041"  # scripted group (container) (typed FeaturePython)
  n = 5
  ref = C_element
FEATURE [App::DocumentObjectGroupPython] H_element077  label="H_element : 039"  # scripted group (container) (typed FeaturePython)
  n = 8
  ref = H_element
FEATURE [App::DocumentObjectGroupPython] O_element079  label="O_element : 040"  # scripted group (container) (typed FeaturePython)
  n = 2
  ref = O_element
FEATURE [App::DocumentObjectGroupPython] G4_PLEXIGLASS  # scripted group (container) (typed FeaturePython)
  Dunit = g/cm3
  Dvalue = 1.19
  Group = -> [C_element083,H_element077,O_element079]
  conduct = 2
  density = 1
  expand = 3
  formula = G4_PLEXIGLASS
  name = G4_PLEXIGLASS
  specific = 4
FEATURE [App::DocumentObjectGroupPython] C_element084  label="C_element : 042"  # scripted group (container) (typed FeaturePython)
  n = 1
  ref = C_element
FEATURE [App::DocumentObjectGroupPython] H_element078  label="H_element : 040"  # scripted group (container) (typed FeaturePython)
  n = 2
  ref = H_element
FEATURE [App::DocumentObjectGroupPython] O_element080  label="O_element : 041"  # scripted group (container) (typed FeaturePython)
  n = 1
  ref = O_element
FEATURE [App::DocumentObjectGroupPython] G4_POLYOXYMETHYLENE  # scripted group (container) (typed FeaturePython)
  Dunit = g/cm3
  Dvalue = 1.425
  Group = -> [C_element084,H_element078,O_element080]
  conduct = 2
  density = 1
  expand = 3
  formula = G4_POLYOXYMETHYLENE
  name = G4_POLYOXYMETHYLENE
  specific = 4
FEATURE [App::DocumentObjectGroupPython] C_element085  label="C_element : 043"  # scripted group (container) (typed FeaturePython)
  n = 2
  ref = C_element
FEATURE [App::DocumentObjectGroupPython] H_element079  label="H_element : 041"  # scripted group (container) (typed FeaturePython)
  n = 4
  ref = H_element
FEATURE [App::DocumentObjectGroupPython] G4_POLYPROPYLENE  # scripted group (container) (typed FeaturePython)
  Dunit = g/cm3
  Dvalue = 0.9
  Group = -> [C_element085,H_element079]
  conduct = 2
  density = 1
  expand = 3
  formula = G4_POLYPROPYLENE
  name = G4_POLYPROPYLENE
  specific = 4
FEATURE [App::DocumentObjectGroupPython] C_element086  label="C_element : 044"  # scripted group (container) (typed FeaturePython)
  n = 8
  ref = C_element
FEATURE [App::DocumentObjectGroupPython] H_element080  label="H_element : 042"  # scripted group (container) (typed FeaturePython)
  n = 8
  ref = H_element
FEATURE [App::DocumentObjectGroupPython] G4_POLYSTYRENE  # scripted group (container) (typed FeaturePython)
  Dunit = g/cm3
  Dvalue = 1.06
  Group = -> [C_element086,H_element080]
  conduct = 2
  density = 1
  expand = 3
  formula = G4_POLYSTYRENE
  name = G4_POLYSTYRENE
  specific = 4
FEATURE [App::DocumentObjectGroupPython] C_element087  label="C_element : 045"  # scripted group (container) (typed FeaturePython)
  n = 2
  ref = C_element
FEATURE [App::DocumentObjectGroupPython] F_element014  label="F_element : 4"  # scripted group (container) (typed FeaturePython)
  n = 4
  ref = F_element
FEATURE [App::DocumentObjectGroupPython] G4_TEFLON  # scripted group (container) (typed FeaturePython)
  Dunit = g/cm3
  Dvalue = 2.2
  Group = -> [C_element087,F_element014]
  conduct = 2
  density = 1
  expand = 3
  formula = G4_TEFLON
  name = G4_TEFLON
  specific = 4
FEATURE [App::DocumentObjectGroupPython] C_element088  label="C_element : 046"  # scripted group (container) (typed FeaturePython)
  n = 2
  ref = C_element
FEATURE [App::DocumentObjectGroupPython] F_element015  label="F_element : 006"  # scripted group (container) (typed FeaturePython)
  n = 3
  ref = F_element
FEATURE [App::DocumentObjectGroupPython] Cl_element018  label="Cl_element : 008"  # scripted group (container) (typed FeaturePython)
  n = 1
  ref = Cl_element
FEATURE [App::DocumentObjectGroupPython] G4_POLYTRIFLUOROCHLOROETHYLENE  # scripted group (container) (typed FeaturePython)
  Dunit = g/cm3
  Dvalue = 2.1
  Group = -> [C_element088,F_element015,Cl_element018]
  conduct = 2
  density = 1
  expand = 3
  formula = G4_POLYTRIFLUOROCHLOROETHYLENE
  name = G4_POLYTRIFLUOROCHLOROETHYLENE
  specific = 4
FEATURE [App::DocumentObjectGroupPython] C_element089  label="C_element : 047"  # scripted group (container) (typed FeaturePython)
  n = 4
  ref = C_element
FEATURE [App::DocumentObjectGroupPython] H_element081  label="H_element : 043"  # scripted group (container) (typed FeaturePython)
  n = 6
  ref = H_element
FEATURE [App::DocumentObjectGroupPython] O_element081  label="O_element : 042"  # scripted group (container) (typed FeaturePython)
  n = 2
  ref = O_element
FEATURE [App::DocumentObjectGroupPython] G4_POLYVINYL_ACETATE  # scripted group (container) (typed FeaturePython)
  Dunit = g/cm3
  Dvalue = 1.19
  Group = -> [C_element089,H_element081,O_element081]
  conduct = 2
  density = 1
  expand = 3
  formula = G4_POLYVINYL_ACETATE
  name = G4_POLYVINYL_ACETATE
  specific = 4
FEATURE [App::DocumentObjectGroupPython] C_element090  label="C_element : 048"  # scripted group (container) (typed FeaturePython)
  n = 2
  ref = C_element
FEATURE [App::DocumentObjectGroupPython] H_element082  label="H_element : 044"  # scripted group (container) (typed FeaturePython)
  n = 4
  ref = H_element
FEATURE [App::DocumentObjectGroupPython] O_element082  label="O_element : 043"  # scripted group (container) (typed FeaturePython)
  n = 1
  ref = O_element
FEATURE [App::DocumentObjectGroupPython] G4_POLYVINYL_ALCOHOL  # scripted group (container) (typed FeaturePython)
  Dunit = g/cm3
  Dvalue = 1.3
  Group = -> [C_element090,H_element082,O_element082]
  conduct = 2
  density = 1
  expand = 3
  formula = G4_POLYVINYL_ALCOHOL
  name = G4_POLYVINYL_ALCOHOL
  specific = 4
FEATURE [App::DocumentObjectGroupPython] C_element091  label="C_element : 049"  # scripted group (container) (typed FeaturePython)
  n = 8
  ref = C_element
FEATURE [App::DocumentObjectGroupPython] H_element083  label="H_element : 045"  # scripted group (container) (typed FeaturePython)
  n = 14
  ref = H_element
FEATURE [App::DocumentObjectGroupPython] O_element083  label="O_element : 044"  # scripted group (container) (typed FeaturePython)
  n = 2
  ref = O_element
FEATURE [App::DocumentObjectGroupPython] G4_POLYVINYL_BUTYRAL  # scripted group (container) (typed FeaturePython)
  Dunit = g/cm3
  Dvalue = 1.12
  Group = -> [C_element091,H_element083,O_element083]
  conduct = 2
  density = 1
  expand = 3
  formula = G4_POLYVINYL_BUTYRAL
  name = G4_POLYVINYL_BUTYRAL
  specific = 4
FEATURE [App::DocumentObjectGroupPython] C_element092  label="C_element : 050"  # scripted group (container) (typed FeaturePython)
  n = 2
  ref = C_element
FEATURE [App::DocumentObjectGroupPython] H_element084  label="H_element : 046"  # scripted group (container) (typed FeaturePython)
  n = 3
  ref = H_element
FEATURE [App::DocumentObjectGroupPython] Cl_element019  label="Cl_element : 009"  # scripted group (container) (typed FeaturePython)
  n = 1
  ref = Cl_element
FEATURE [App::DocumentObjectGroupPython] G4_POLYVINYL_CHLORIDE  # scripted group (container) (typed FeaturePython)
  Dunit = g/cm3
  Dvalue = 1.3
  Group = -> [C_element092,H_element084,Cl_element019]
  conduct = 2
  density = 1
  expand = 3
  formula = G4_POLYVINYL_CHLORIDE
  name = G4_POLYVINYL_CHLORIDE
  specific = 4
FEATURE [App::DocumentObjectGroupPython] C_element093  label="C_element : 051"  # scripted group (container) (typed FeaturePython)
  n = 2
  ref = C_element
FEATURE [App::DocumentObjectGroupPython] H_element085  label="H_element : 047"  # scripted group (container) (typed FeaturePython)
  n = 2
  ref = H_element
FEATURE [App::DocumentObjectGroupPython] Cl_element020  label="Cl_element : 010"  # scripted group (container) (typed FeaturePython)
  n = 2
  ref = Cl_element
FEATURE [App::DocumentObjectGroupPython] G4_POLYVINYLIDENE_CHLORIDE  # scripted group (container) (typed FeaturePython)
  Dunit = g/cm3
  Dvalue = 1.7
  Group = -> [C_element093,H_element085,Cl_element020]
  conduct = 2
  density = 1
  expand = 3
  formula = G4_POLYVINYLIDENE_CHLORIDE
  name = G4_POLYVINYLIDENE_CHLORIDE
  specific = 4
FEATURE [App::DocumentObjectGroupPython] C_element094  label="C_element : 052"  # scripted group (container) (typed FeaturePython)
  n = 2
  ref = C_element
FEATURE [App::DocumentObjectGroupPython] H_element086  label="H_element : 048"  # scripted group (container) (typed FeaturePython)
  n = 2
  ref = H_element
FEATURE [App::DocumentObjectGroupPython] F_element016  label="F_element : 007"  # scripted group (container) (typed FeaturePython)
  n = 2
  ref = F_element
FEATURE [App::DocumentObjectGroupPython] G4_POLYVINYLIDENE_FLUORIDE  # scripted group (container) (typed FeaturePython)
  Dunit = g/cm3
  Dvalue = 1.76
  Group = -> [C_element094,H_element086,F_element016]
  conduct = 2
  density = 1
  expand = 3
  formula = G4_POLYVINYLIDENE_FLUORIDE
  name = G4_POLYVINYLIDENE_FLUORIDE
  specific = 4
FEATURE [App::DocumentObjectGroupPython] C_element095  label="C_element : 053"  # scripted group (container) (typed FeaturePython)
  n = 6
  ref = C_element
FEATURE [App::DocumentObjectGroupPython] H_element087  label="H_element : 9"  # scripted group (container) (typed FeaturePython)
  n = 9
  ref = H_element
FEATURE [App::DocumentObjectGroupPython] N_element037  label="N_element : 016"  # scripted group (container) (typed FeaturePython)
  n = 1
  ref = N_element
FEATURE [App::DocumentObjectGroupPython] O_element084  label="O_element : 045"  # scripted group (container) (typed FeaturePython)
  n = 1
  ref = O_element
FEATURE [App::DocumentObjectGroupPython] G4_POLYVINYL_PYRROLIDONE  # scripted group (container) (typed FeaturePython)
  Dunit = g/cm3
  Dvalue = 1.25
  Group = -> [C_element095,H_element087,N_element037,O_element084]
  conduct = 2
  density = 1
  expand = 3
  formula = G4_POLYVINYL_PYRROLIDONE
  name = G4_POLYVINYL_PYRROLIDONE
  specific = 4
FEATURE [App::DocumentObjectGroupPython] K_element008  label="K_element : 1"  # scripted group (container) (typed FeaturePython)
  n = 1
  ref = K_element
FEATURE [App::DocumentObjectGroupPython] I_element006  label="I_element : 003"  # scripted group (container) (typed FeaturePython)
  n = 1
  ref = I_element
FEATURE [App::DocumentObjectGroupPython] G4_POTASSIUM_IODIDE  # scripted group (container) (typed FeaturePython)
  Dunit = g/cm3
  Dvalue = 3.13
  Group = -> [K_element008,I_element006]
  conduct = 2
  density = 1
  expand = 3
  formula = G4_POTASSIUM_IODIDE
  name = G4_POTASSIUM_IODIDE
  specific = 4
FEATURE [App::DocumentObjectGroupPython] K_element009  label="K_element : 2"  # scripted group (container) (typed FeaturePython)
  n = 2
  ref = K_element
FEATURE [App::DocumentObjectGroupPython] O_element085  label="O_element : 046"  # scripted group (container) (typed FeaturePython)
  n = 1
  ref = O_element
FEATURE [App::DocumentObjectGroupPython] G4_POTASSIUM_OXIDE  # scripted group (container) (typed FeaturePython)
  Dunit = g/cm3
  Dvalue = 2.32
  Group = -> [K_element009,O_element085]
  conduct = 2
  density = 1
  expand = 3
  formula = G4_POTASSIUM_OXIDE
  name = G4_POTASSIUM_OXIDE
  specific = 4
FEATURE [App::DocumentObjectGroupPython] C_element096  label="C_element : 054"  # scripted group (container) (typed FeaturePython)
  n = 3
  ref = C_element
FEATURE [App::DocumentObjectGroupPython] H_element088  label="H_element : 049"  # scripted group (container) (typed FeaturePython)
  n = 8
  ref = H_element
FEATURE [App::DocumentObjectGroupPython] G4_PROPANE  # scripted group (container) (typed FeaturePython)
  Dunit = g/cm3
  Dvalue = 0.00187939
  Group = -> [C_element096,H_element088]
  conduct = 2
  density = 1
  expand = 3
  formula = G4_PROPANE
  name = G4_PROPANE
  specific = 4
FEATURE [App::DocumentObjectGroupPython] C_element097  label="C_element : 055"  # scripted group (container) (typed FeaturePython)
  n = 3
  ref = C_element
FEATURE [App::DocumentObjectGroupPython] H_element089  label="H_element : 050"  # scripted group (container) (typed FeaturePython)
  n = 8
  ref = H_element
FEATURE [App::DocumentObjectGroupPython] G4_lPROPANE  # scripted group (container) (typed FeaturePython)
  Dunit = g/cm3
  Dvalue = 0.43
  Group = -> [C_element097,H_element089]
  conduct = 2
  density = 1
  expand = 3
  formula = G4_lPROPANE
  name = G4_lPROPANE
  specific = 4
FEATURE [App::DocumentObjectGroupPython] C_element098  label="C_element : 056"  # scripted group (container) (typed FeaturePython)
  n = 3
  ref = C_element
FEATURE [App::DocumentObjectGroupPython] H_element090  label="H_element : 051"  # scripted group (container) (typed FeaturePython)
  n = 8
  ref = H_element
FEATURE [App::DocumentObjectGroupPython] O_element086  label="O_element : 047"  # scripted group (container) (typed FeaturePython)
  n = 1
  ref = O_element
FEATURE [App::DocumentObjectGroupPython] G4_N_PROPYL_ALCOHOL  label="G4_N-PROPYL_ALCOHOL"  # scripted group (container) (typed FeaturePython)
  Dunit = g/cm3
  Dvalue = 0.8035
  Group = -> [C_element098,H_element090,O_element086]
  conduct = 2
  density = 1
  expand = 3
  formula = G4_N-PROPYL_ALCOHOL
  name = G4_N-PROPYL_ALCOHOL
  specific = 4
FEATURE [App::DocumentObjectGroupPython] C_element099  label="C_element : 057"  # scripted group (container) (typed FeaturePython)
  n = 5
  ref = C_element
FEATURE [App::DocumentObjectGroupPython] H_element091  label="H_element : 052"  # scripted group (container) (typed FeaturePython)
  n = 5
  ref = H_element
FEATURE [App::DocumentObjectGroupPython] N_element038  label="N_element : 017"  # scripted group (container) (typed FeaturePython)
  n = 1
  ref = N_element
FEATURE [App::DocumentObjectGroupPython] G4_PYRIDINE  # scripted group (container) (typed FeaturePython)
  Dunit = g/cm3
  Dvalue = 0.9819
  Group = -> [C_element099,H_element091,N_element038]
  conduct = 2
  density = 1
  expand = 3
  formula = G4_PYRIDINE
  name = G4_PYRIDINE
  specific = 4
FEATURE [App::DocumentObjectGroupPython] H_element092  label="H_element : 0.144"  # scripted group (container) (typed FeaturePython)
  n = 0.143711
FEATURE [App::DocumentObjectGroupPython] C_element100  label="C_element : 0.856"  # scripted group (container) (typed FeaturePython)
  n = 0.856289
FEATURE [App::DocumentObjectGroupPython] G4_RUBBER_BUTYL  # scripted group (container) (typed FeaturePython)
  Dunit = g/cm3
  Dvalue = 0.92
  Group = -> [H_element092,C_element100]
  conduct = 2
  density = 1
  expand = 3
  formula = G4_RUBBER_BUTYL
  name = G4_RUBBER_BUTYL
  specific = 4
FEATURE [App::DocumentObjectGroupPython] H_element093  label="H_element : 0.118"  # scripted group (container) (typed FeaturePython)
  n = 0.118371
FEATURE [App::DocumentObjectGroupPython] C_element101  label="C_element : 0.882"  # scripted group (container) (typed FeaturePython)
  n = 0.881629
FEATURE [App::DocumentObjectGroupPython] G4_RUBBER_NATURAL  # scripted group (container) (typed FeaturePython)
  Dunit = g/cm3
  Dvalue = 0.92
  Group = -> [H_element093,C_element101]
  conduct = 2
  density = 1
  expand = 3
  formula = G4_RUBBER_NATURAL
  name = G4_RUBBER_NATURAL
  specific = 4
FEATURE [App::DocumentObjectGroupPython] H_element094  label="H_element : 0.145"  # scripted group (container) (typed FeaturePython)
  n = 0.05692
FEATURE [App::DocumentObjectGroupPython] C_element102  label="C_element : 0.543"  # scripted group (container) (typed FeaturePython)
  n = 0.542646
FEATURE [App::DocumentObjectGroupPython] Cl_element021  label="Cl_element : 0.400"  # scripted group (container) (typed FeaturePython)
  n = 0.400434
FEATURE [App::DocumentObjectGroupPython] G4_RUBBER_NEOPRENE  # scripted group (container) (typed FeaturePython)
  Dunit = g/cm3
  Dvalue = 1.23
  Group = -> [H_element094,C_element102,Cl_element021]
  conduct = 2
  density = 1
  expand = 3
  formula = G4_RUBBER_NEOPRENE
  name = G4_RUBBER_NEOPRENE
  specific = 4
FEATURE [App::DocumentObjectGroupPython] Si_element006  label="Si_element : 1"  # scripted group (container) (typed FeaturePython)
  n = 1
  ref = Si_element
FEATURE [App::DocumentObjectGroupPython] O_element087  label="O_element : 048"  # scripted group (container) (typed FeaturePython)
  n = 2
  ref = O_element
FEATURE [App::DocumentObjectGroupPython] G4_SILICON_DIOXIDE002  label="G4_SILICON_DIOXIDE"  # scripted group (container) (typed FeaturePython)
  Dunit = g/cm3
  Dvalue = 2.32
  Group = -> [Si_element006,O_element087]
  conduct = 2
  density = 1
  expand = 3
  formula = G4_SILICON_DIOXIDE
  name = G4_SILICON_DIOXIDE
  specific = 4
FEATURE [App::DocumentObjectGroupPython] Ag_element002  label="Ag_element : 1"  # scripted group (container) (typed FeaturePython)
  n = 1
  ref = Ag_element
FEATURE [App::DocumentObjectGroupPython] Br_element005  label="Br_element : 003"  # scripted group (container) (typed FeaturePython)
  n = 1
  ref = Br_element
FEATURE [App::DocumentObjectGroupPython] G4_SILVER_BROMIDE  # scripted group (container) (typed FeaturePython)
  Dunit = g/cm3
  Dvalue = 6.473
  Group = -> [Ag_element002,Br_element005]
  conduct = 2
  density = 1
  expand = 3
  formula = G4_SILVER_BROMIDE
  name = G4_SILVER_BROMIDE
  specific = 4
FEATURE [App::DocumentObjectGroupPython] Ag_element003  label="Ag_element : 002"  # scripted group (container) (typed FeaturePython)
  n = 1
  ref = Ag_element
FEATURE [App::DocumentObjectGroupPython] Cl_element022  label="Cl_element : 011"  # scripted group (container) (typed FeaturePython)
  n = 1
  ref = Cl_element
FEATURE [App::DocumentObjectGroupPython] G4_SILVER_CHLORIDE  # scripted group (container) (typed FeaturePython)
  Dunit = g/cm3
  Dvalue = 5.56
  Group = -> [Ag_element003,Cl_element022]
  conduct = 2
  density = 1
  expand = 3
  formula = G4_SILVER_CHLORIDE
  name = G4_SILVER_CHLORIDE
  specific = 4
FEATURE [App::DocumentObjectGroupPython] Br_element006  label="Br_element : 0.423"  # scripted group (container) (typed FeaturePython)
  n = 0.422895
FEATURE [App::DocumentObjectGroupPython] Ag_element004  label="Ag_element : 0.574"  # scripted group (container) (typed FeaturePython)
  n = 0.573748
FEATURE [App::DocumentObjectGroupPython] I_element007  label="I_element : 0.649"  # scripted group (container) (typed FeaturePython)
  n = 0.003357
FEATURE [App::DocumentObjectGroupPython] G4_SILVER_HALIDES  # scripted group (container) (typed FeaturePython)
  Dunit = g/cm3
  Dvalue = 6.47
  Group = -> [Br_element006,Ag_element004,I_element007]
  conduct = 2
  density = 1
  expand = 3
  formula = G4_SILVER_HALIDES
  name = G4_SILVER_HALIDES
  specific = 4
FEATURE [App::DocumentObjectGroupPython] Ag_element005  label="Ag_element : 003"  # scripted group (container) (typed FeaturePython)
  n = 1
  ref = Ag_element
FEATURE [App::DocumentObjectGroupPython] I_element008  label="I_element : 004"  # scripted group (container) (typed FeaturePython)
  n = 1
  ref = I_element
FEATURE [App::DocumentObjectGroupPython] G4_SILVER_IODIDE  # scripted group (container) (typed FeaturePython)
  Dunit = g/cm3
  Dvalue = 6.01
  Group = -> [Ag_element005,I_element008]
  conduct = 2
  density = 1
  expand = 3
  formula = G4_SILVER_IODIDE
  name = G4_SILVER_IODIDE
  specific = 4
FEATURE [App::DocumentObjectGroupPython] H_element095  label="H_element : 0.100"  # scripted group (container) (typed FeaturePython)
  n = 0.1
FEATURE [App::DocumentObjectGroupPython] C_element103  label="C_element : 0.204"  # scripted group (container) (typed FeaturePython)
  n = 0.204
FEATURE [App::DocumentObjectGroupPython] N_element039  label="N_element : 0.759"  # scripted group (container) (typed FeaturePython)
  n = 0.042
FEATURE [App::DocumentObjectGroupPython] O_element088  label="O_element : 0.645"  # scripted group (container) (typed FeaturePython)
  n = 0.645
FEATURE [App::DocumentObjectGroupPython] Na_element013  label="Na_element : 0.100"  # scripted group (container) (typed FeaturePython)
  n = 0.002
FEATURE [App::DocumentObjectGroupPython] P_element009  label="P_element : 0.107"  # scripted group (container) (typed FeaturePython)
  n = 0.001
FEATURE [App::DocumentObjectGroupPython] S_element020  label="S_element : 0.021"  # scripted group (container) (typed FeaturePython)
  n = 0.002
FEATURE [App::DocumentObjectGroupPython] Cl_element023  label="Cl_element : 0.590"  # scripted group (container) (typed FeaturePython)
  n = 0.003
FEATURE [App::DocumentObjectGroupPython] K_element010  label="K_element : 0.001"  # scripted group (container) (typed FeaturePython)
  n = 0.001
FEATURE [App::DocumentObjectGroupPython] G4_SKIN_ICRP  # scripted group (container) (typed FeaturePython)
  Dunit = g/cm3
  Dvalue = 1.09
  Group = -> [H_element095,C_element103,N_element039,O_element088,Na_element013,P_element009,S_element020,Cl_element023,K_element010]
  conduct = 2
  density = 1
  expand = 3
  formula = G4_SKIN_ICRP
  name = G4_SKIN_ICRP
  specific = 4
FEATURE [App::DocumentObjectGroupPython] Na_element014  label="Na_element : 2"  # scripted group (container) (typed FeaturePython)
  n = 2
  ref = Na_element
FEATURE [App::DocumentObjectGroupPython] C_element104  label="C_element : 058"  # scripted group (container) (typed FeaturePython)
  n = 1
  ref = C_element
FEATURE [App::DocumentObjectGroupPython] O_element089  label="O_element : 049"  # scripted group (container) (typed FeaturePython)
  n = 3
  ref = O_element
FEATURE [App::DocumentObjectGroupPython] G4_SODIUM_CARBONATE  # scripted group (container) (typed FeaturePython)
  Dunit = g/cm3
  Dvalue = 2.532
  Group = -> [Na_element014,C_element104,O_element089]
  conduct = 2
  density = 1
  expand = 3
  formula = G4_SODIUM_CARBONATE
  name = G4_SODIUM_CARBONATE
  specific = 4
FEATURE [App::DocumentObjectGroupPython] Na_element015  label="Na_element : 1"  # scripted group (container) (typed FeaturePython)
  n = 1
  ref = Na_element
FEATURE [App::DocumentObjectGroupPython] I_element009  label="I_element : 005"  # scripted group (container) (typed FeaturePython)
  n = 1
  ref = I_element
FEATURE [App::DocumentObjectGroupPython] G4_SODIUM_IODIDE  # scripted group (container) (typed FeaturePython)
  Dunit = g/cm3
  Dvalue = 3.667
  Group = -> [Na_element015,I_element009]
  conduct = 2
  density = 1
  expand = 3
  formula = G4_SODIUM_IODIDE
  name = G4_SODIUM_IODIDE
  specific = 4
FEATURE [App::DocumentObjectGroupPython] Na_element016  label="Na_element : 003"  # scripted group (container) (typed FeaturePython)
  n = 2
  ref = Na_element
FEATURE [App::DocumentObjectGroupPython] O_element090  label="O_element : 050"  # scripted group (container) (typed FeaturePython)
  n = 1
  ref = O_element
FEATURE [App::DocumentObjectGroupPython] G4_SODIUM_MONOXIDE  # scripted group (container) (typed FeaturePython)
  Dunit = g/cm3
  Dvalue = 2.27
  Group = -> [Na_element016,O_element090]
  conduct = 2
  density = 1
  expand = 3
  formula = G4_SODIUM_MONOXIDE
  name = G4_SODIUM_MONOXIDE
  specific = 4
FEATURE [App::DocumentObjectGroupPython] Na_element017  label="Na_element : 004"  # scripted group (container) (typed FeaturePython)
  n = 1
  ref = Na_element
FEATURE [App::DocumentObjectGroupPython] N_element040  label="N_element : 018"  # scripted group (container) (typed FeaturePython)
  n = 1
  ref = N_element
FEATURE [App::DocumentObjectGroupPython] O_element091  label="O_element : 051"  # scripted group (container) (typed FeaturePython)
  n = 3
  ref = O_element
FEATURE [App::DocumentObjectGroupPython] G4_SODIUM_NITRATE  # scripted group (container) (typed FeaturePython)
  Dunit = g/cm3
  Dvalue = 2.261
  Group = -> [Na_element017,N_element040,O_element091]
  conduct = 2
  density = 1
  expand = 3
  formula = G4_SODIUM_NITRATE
  name = G4_SODIUM_NITRATE
  specific = 4
FEATURE [App::DocumentObjectGroupPython] C_element105  label="C_element : 059"  # scripted group (container) (typed FeaturePython)
  n = 14
  ref = C_element
FEATURE [App::DocumentObjectGroupPython] H_element096  label="H_element : 053"  # scripted group (container) (typed FeaturePython)
  n = 12
  ref = H_element
FEATURE [App::DocumentObjectGroupPython] G4_STILBENE  # scripted group (container) (typed FeaturePython)
  Dunit = g/cm3
  Dvalue = 0.9707
  Group = -> [C_element105,H_element096]
  conduct = 2
  density = 1
  expand = 3
  formula = G4_STILBENE
  name = G4_STILBENE
  specific = 4
FEATURE [App::DocumentObjectGroupPython] C_element106  label="C_element : 12"  # scripted group (container) (typed FeaturePython)
  n = 12
  ref = C_element
FEATURE [App::DocumentObjectGroupPython] H_element097  label="H_element : 22"  # scripted group (container) (typed FeaturePython)
  n = 22
  ref = H_element
FEATURE [App::DocumentObjectGroupPython] O_element092  label="O_element : 11"  # scripted group (container) (typed FeaturePython)
  n = 11
  ref = O_element
FEATURE [App::DocumentObjectGroupPython] G4_SUCROSE  # scripted group (container) (typed FeaturePython)
  Dunit = g/cm3
  Dvalue = 1.5805
  Group = -> [C_element106,H_element097,O_element092]
  conduct = 2
  density = 1
  expand = 3
  formula = G4_SUCROSE
  name = G4_SUCROSE
  specific = 4
FEATURE [App::DocumentObjectGroupPython] C_element107  label="C_element : 18"  # scripted group (container) (typed FeaturePython)
  n = 18
  ref = C_element
FEATURE [App::DocumentObjectGroupPython] H_element098  label="H_element : 054"  # scripted group (container) (typed FeaturePython)
  n = 14
  ref = H_element
FEATURE [App::DocumentObjectGroupPython] G4_TERPHENYL  # scripted group (container) (typed FeaturePython)
  Dunit = g/cm3
  Dvalue = 1.24
  Group = -> [C_element107,H_element098]
  conduct = 2
  density = 1
  expand = 3
  formula = G4_TERPHENYL
  name = G4_TERPHENYL
  specific = 4
FEATURE [App::DocumentObjectGroupPython] H_element099  label="H_element : 0.146"  # scripted group (container) (typed FeaturePython)
  n = 0.106
FEATURE [App::DocumentObjectGroupPython] C_element108  label="C_element : 0.883"  # scripted group (container) (typed FeaturePython)
  n = 0.099
FEATURE [App::DocumentObjectGroupPython] N_element041  label="N_element : 0.020"  # scripted group (container) (typed FeaturePython)
  n = 0.02
FEATURE [App::DocumentObjectGroupPython] O_element093  label="O_element : 0.766"  # scripted group (container) (typed FeaturePython)
  n = 0.766
FEATURE [App::DocumentObjectGroupPython] Na_element018  label="Na_element : 0.101"  # scripted group (container) (typed FeaturePython)
  n = 0.002
FEATURE [App::DocumentObjectGroupPython] P_element010  label="P_element : 0.108"  # scripted group (container) (typed FeaturePython)
  n = 0.001
FEATURE [App::DocumentObjectGroupPython] S_element021  label="S_element : 0.022"  # scripted group (container) (typed FeaturePython)
  n = 0.002
FEATURE [App::DocumentObjectGroupPython] Cl_element024  label="Cl_element : 0.002"  # scripted group (container) (typed FeaturePython)
  n = 0.002
FEATURE [App::DocumentObjectGroupPython] K_element011  label="K_element : 0.017"  # scripted group (container) (typed FeaturePython)
  n = 0.002
FEATURE [App::DocumentObjectGroupPython] G4_TESTIS_ICRP  # scripted group (container) (typed FeaturePython)
  Dunit = g/cm3
  Dvalue = 1.04
  Group = -> [H_element099,C_element108,N_element041,O_element093,Na_element018,P_element010,S_element021,Cl_element024,K_element011]
  conduct = 2
  density = 1
  expand = 3
  formula = G4_TESTIS_ICRP
  name = G4_TESTIS_ICRP
  specific = 4
FEATURE [App::DocumentObjectGroupPython] C_element109  label="C_element : 060"  # scripted group (container) (typed FeaturePython)
  n = 2
  ref = C_element
FEATURE [App::DocumentObjectGroupPython] Cl_element025  label="Cl_element : 012"  # scripted group (container) (typed FeaturePython)
  n = 4
  ref = Cl_element
FEATURE [App::DocumentObjectGroupPython] G4_TETRACHLOROETHYLENE  # scripted group (container) (typed FeaturePython)
  Dunit = g/cm3
  Dvalue = 1.625
  Group = -> [C_element109,Cl_element025]
  conduct = 2
  density = 1
  expand = 3
  formula = G4_TETRACHLOROETHYLENE
  name = G4_TETRACHLOROETHYLENE
  specific = 4
FEATURE [App::DocumentObjectGroupPython] Tl_element001  label="Tl_element : 1"  # scripted group (container) (typed FeaturePython)
  n = 1
  ref = Tl_element
FEATURE [App::DocumentObjectGroupPython] Cl_element026  label="Cl_element : 013"  # scripted group (container) (typed FeaturePython)
  n = 1
  ref = Cl_element
FEATURE [App::DocumentObjectGroupPython] G4_THALLIUM_CHLORIDE  # scripted group (container) (typed FeaturePython)
  Dunit = g/cm3
  Dvalue = 7.004
  Group = -> [Tl_element001,Cl_element026]
  conduct = 2
  density = 1
  expand = 3
  formula = G4_THALLIUM_CHLORIDE
  name = G4_THALLIUM_CHLORIDE
  specific = 4
FEATURE [App::DocumentObjectGroupPython] H_element100  label="H_element : 0.147"  # scripted group (container) (typed FeaturePython)
  n = 0.105
FEATURE [App::DocumentObjectGroupPython] C_element110  label="C_element : 0.256"  # scripted group (container) (typed FeaturePython)
  n = 0.256
FEATURE [App::DocumentObjectGroupPython] N_element042  label="N_element : 0.760"  # scripted group (container) (typed FeaturePython)
  n = 0.027
FEATURE [App::DocumentObjectGroupPython] O_element094  label="O_element : 0.602"  # scripted group (container) (typed FeaturePython)
  n = 0.602
FEATURE [App::DocumentObjectGroupPython] Na_element019  label="Na_element : 0.102"  # scripted group (container) (typed FeaturePython)
  n = 0.001
FEATURE [App::DocumentObjectGroupPython] P_element011  label="P_element : 0.109"  # scripted group (container) (typed FeaturePython)
  n = 0.002
FEATURE [App::DocumentObjectGroupPython] S_element022  label="S_element : 0.023"  # scripted group (container) (typed FeaturePython)
  n = 0.003
FEATURE [App::DocumentObjectGroupPython] Cl_element027  label="Cl_element : 0.591"  # scripted group (container) (typed FeaturePython)
  n = 0.002
FEATURE [App::DocumentObjectGroupPython] K_element012  label="K_element : 0.018"  # scripted group (container) (typed FeaturePython)
  n = 0.002
FEATURE [App::DocumentObjectGroupPython] G4_TISSUE_SOFT_ICRP  # scripted group (container) (typed FeaturePython)
  Dunit = g/cm3
  Dvalue = 1.03
  Group = -> [H_element100,C_element110,N_element042,O_element094,Na_element019,P_element011,S_element022,Cl_element027,K_element012]
  conduct = 2
  density = 1
  expand = 3
  formula = G4_TISSUE_SOFT_ICRP
  name = G4_TISSUE_SOFT_ICRP
  specific = 4
FEATURE [App::DocumentObjectGroupPython] H_element101  label="H_element : 0.148"  # scripted group (container) (typed FeaturePython)
  n = 0.101
FEATURE [App::DocumentObjectGroupPython] C_element111  label="C_element : 0.111"  # scripted group (container) (typed FeaturePython)
  n = 0.111
FEATURE [App::DocumentObjectGroupPython] N_element043  label="N_element : 0.026"  # scripted group (container) (typed FeaturePython)
  n = 0.026
FEATURE [App::DocumentObjectGroupPython] O_element095  label="O_element : 0.762"  # scripted group (container) (typed FeaturePython)
  n = 0.762
FEATURE [App::DocumentObjectGroupPython] G4_TISSUE_SOFT_ICRU_4  label="G4_TISSUE_SOFT_ICRU-4"  # scripted group (container) (typed FeaturePython)
  Dunit = g/cm3
  Dvalue = 1
  Group = -> [H_element101,C_element111,N_element043,O_element095]
  conduct = 2
  density = 1
  expand = 3
  formula = G4_TISSUE_SOFT_ICRU-4
  name = G4_TISSUE_SOFT_ICRU-4
  specific = 4
FEATURE [App::DocumentObjectGroupPython] H_element102  label="H_element : 0.149"  # scripted group (container) (typed FeaturePython)
  n = 0.101869
FEATURE [App::DocumentObjectGroupPython] C_element112  label="C_element : 0.456"  # scripted group (container) (typed FeaturePython)
  n = 0.456179
FEATURE [App::DocumentObjectGroupPython] N_element044  label="N_element : 0.761"  # scripted group (container) (typed FeaturePython)
  n = 0.035172
FEATURE [App::DocumentObjectGroupPython] O_element096  label="O_element : 0.407"  # scripted group (container) (typed FeaturePython)
  n = 0.40678
FEATURE [App::DocumentObjectGroupPython] G4_TISSUE_METHANE  label="G4_TISSUE-METHANE"  # scripted group (container) (typed FeaturePython)
  Dunit = g/cm3
  Dvalue = 0.00106409
  Group = -> [H_element102,C_element112,N_element044,O_element096]
  conduct = 2
  density = 1
  expand = 3
  formula = G4_TISSUE-METHANE
  name = G4_TISSUE-METHANE
  specific = 4
FEATURE [App::DocumentObjectGroupPython] H_element103  label="H_element : 0.103"  # scripted group (container) (typed FeaturePython)
  n = 0.102672
FEATURE [App::DocumentObjectGroupPython] C_element113  label="C_element : 0.569"  # scripted group (container) (typed FeaturePython)
  n = 0.56894
FEATURE [App::DocumentObjectGroupPython] N_element045  label="N_element : 0.762"  # scripted group (container) (typed FeaturePython)
  n = 0.035022
FEATURE [App::DocumentObjectGroupPython] O_element097  label="O_element : 0.293"  # scripted group (container) (typed FeaturePython)
  n = 0.293366
FEATURE [App::DocumentObjectGroupPython] G4_TISSUE_PROPANE  label="G4_TISSUE-PROPANE"  # scripted group (container) (typed FeaturePython)
  Dunit = g/cm3
  Dvalue = 0.00182628
  Group = -> [H_element103,C_element113,N_element045,O_element097]
  conduct = 2
  density = 1
  expand = 3
  formula = G4_TISSUE-PROPANE
  name = G4_TISSUE-PROPANE
  specific = 4
FEATURE [App::DocumentObjectGroupPython] Ti_element003  label="Ti_element : 1"  # scripted group (container) (typed FeaturePython)
  n = 1
  ref = Ti_element
FEATURE [App::DocumentObjectGroupPython] O_element098  label="O_element : 052"  # scripted group (container) (typed FeaturePython)
  n = 2
  ref = O_element
FEATURE [App::DocumentObjectGroupPython] G4_TITANIUM_DIOXIDE  # scripted group (container) (typed FeaturePython)
  Dunit = g/cm3
  Dvalue = 4.26
  Group = -> [Ti_element003,O_element098]
  conduct = 2
  density = 1
  expand = 3
  formula = G4_TITANIUM_DIOXIDE
  name = G4_TITANIUM_DIOXIDE
  specific = 4
FEATURE [App::DocumentObjectGroupPython] C_element114  label="C_element : 061"  # scripted group (container) (typed FeaturePython)
  n = 7
  ref = C_element
FEATURE [App::DocumentObjectGroupPython] H_element104  label="H_element : 055"  # scripted group (container) (typed FeaturePython)
  n = 8
  ref = H_element
FEATURE [App::DocumentObjectGroupPython] G4_TOLUENE  # scripted group (container) (typed FeaturePython)
  Dunit = g/cm3
  Dvalue = 0.8669
  Group = -> [C_element114,H_element104]
  conduct = 2
  density = 1
  expand = 3
  formula = G4_TOLUENE
  name = G4_TOLUENE
  specific = 4
FEATURE [App::DocumentObjectGroupPython] C_element115  label="C_element : 062"  # scripted group (container) (typed FeaturePython)
  n = 2
  ref = C_element
FEATURE [App::DocumentObjectGroupPython] H_element105  label="H_element : 056"  # scripted group (container) (typed FeaturePython)
  n = 1
  ref = H_element
FEATURE [App::DocumentObjectGroupPython] Cl_element028  label="Cl_element : 014"  # scripted group (container) (typed FeaturePython)
  n = 3
  ref = Cl_element
FEATURE [App::DocumentObjectGroupPython] G4_TRICHLOROETHYLENE  # scripted group (container) (typed FeaturePython)
  Dunit = g/cm3
  Dvalue = 1.46
  Group = -> [C_element115,H_element105,Cl_element028]
  conduct = 2
  density = 1
  expand = 3
  formula = G4_TRICHLOROETHYLENE
  name = G4_TRICHLOROETHYLENE
  specific = 4
FEATURE [App::DocumentObjectGroupPython] C_element116  label="C_element : 063"  # scripted group (container) (typed FeaturePython)
  n = 6
  ref = C_element
FEATURE [App::DocumentObjectGroupPython] H_element106  label="H_element : 15"  # scripted group (container) (typed FeaturePython)
  n = 15
  ref = H_element
FEATURE [App::DocumentObjectGroupPython] O_element099  label="O_element : 053"  # scripted group (container) (typed FeaturePython)
  n = 4
  ref = O_element
FEATURE [App::DocumentObjectGroupPython] P_element012  label="P_element : 1"  # scripted group (container) (typed FeaturePython)
  n = 1
  ref = P_element
FEATURE [App::DocumentObjectGroupPython] G4_TRIETHYL_PHOSPHATE  # scripted group (container) (typed FeaturePython)
  Dunit = g/cm3
  Dvalue = 1.07
  Group = -> [C_element116,H_element106,O_element099,P_element012]
  conduct = 2
  density = 1
  expand = 3
  formula = G4_TRIETHYL_PHOSPHATE
  name = G4_TRIETHYL_PHOSPHATE
  specific = 4
FEATURE [App::DocumentObjectGroupPython] W_element003  label="W_element : 003"  # scripted group (container) (typed FeaturePython)
  n = 1
  ref = W_element
FEATURE [App::DocumentObjectGroupPython] F_element017  label="F_element : 6"  # scripted group (container) (typed FeaturePython)
  n = 6
  ref = F_element
FEATURE [App::DocumentObjectGroupPython] G4_TUNGSTEN_HEXAFLUORIDE  # scripted group (container) (typed FeaturePython)
  Dunit = g/cm3
  Dvalue = 2.4
  Group = -> [W_element003,F_element017]
  conduct = 2
  density = 1
  expand = 3
  formula = G4_TUNGSTEN_HEXAFLUORIDE
  name = G4_TUNGSTEN_HEXAFLUORIDE
  specific = 4
FEATURE [App::DocumentObjectGroupPython] U_element001  label="U_element : 1"  # scripted group (container) (typed FeaturePython)
  n = 1
  ref = U_element
FEATURE [App::DocumentObjectGroupPython] C_element117  label="C_element : 064"  # scripted group (container) (typed FeaturePython)
  n = 2
  ref = C_element
FEATURE [App::DocumentObjectGroupPython] G4_URANIUM_DICARBIDE  # scripted group (container) (typed FeaturePython)
  Dunit = g/cm3
  Dvalue = 11.28
  Group = -> [U_element001,C_element117]
  conduct = 2
  density = 1
  expand = 3
  formula = G4_URANIUM_DICARBIDE
  name = G4_URANIUM_DICARBIDE
  specific = 4
FEATURE [App::DocumentObjectGroupPython] U_element002  label="U_element : 002"  # scripted group (container) (typed FeaturePython)
  n = 1
  ref = U_element
FEATURE [App::DocumentObjectGroupPython] C_element118  label="C_element : 065"  # scripted group (container) (typed FeaturePython)
  n = 1
  ref = C_element
FEATURE [App::DocumentObjectGroupPython] G4_URANIUM_MONOCARBIDE  # scripted group (container) (typed FeaturePython)
  Dunit = g/cm3
  Dvalue = 13.63
  Group = -> [U_element002,C_element118]
  conduct = 2
  density = 1
  expand = 3
  formula = G4_URANIUM_MONOCARBIDE
  name = G4_URANIUM_MONOCARBIDE
  specific = 4
FEATURE [App::DocumentObjectGroupPython] U_element003  label="U_element : 003"  # scripted group (container) (typed FeaturePython)
  n = 1
  ref = U_element
FEATURE [App::DocumentObjectGroupPython] O_element100  label="O_element : 054"  # scripted group (container) (typed FeaturePython)
  n = 2
  ref = O_element
FEATURE [App::DocumentObjectGroupPython] G4_URANIUM_OXIDE  # scripted group (container) (typed FeaturePython)
  Dunit = g/cm3
  Dvalue = 10.96
  Group = -> [U_element003,O_element100]
  conduct = 2
  density = 1
  expand = 3
  formula = G4_URANIUM_OXIDE
  name = G4_URANIUM_OXIDE
  specific = 4
FEATURE [App::DocumentObjectGroupPython] C_element119  label="C_element : 066"  # scripted group (container) (typed FeaturePython)
  n = 1
  ref = C_element
FEATURE [App::DocumentObjectGroupPython] H_element107  label="H_element : 057"  # scripted group (container) (typed FeaturePython)
  n = 4
  ref = H_element
FEATURE [App::DocumentObjectGroupPython] N_element046  label="N_element : 019"  # scripted group (container) (typed FeaturePython)
  n = 2
  ref = N_element
FEATURE [App::DocumentObjectGroupPython] O_element101  label="O_element : 055"  # scripted group (container) (typed FeaturePython)
  n = 1
  ref = O_element
FEATURE [App::DocumentObjectGroupPython] G4_UREA  # scripted group (container) (typed FeaturePython)
  Dunit = g/cm3
  Dvalue = 1.323
  Group = -> [C_element119,H_element107,N_element046,O_element101]
  conduct = 2
  density = 1
  expand = 3
  formula = G4_UREA
  name = G4_UREA
  specific = 4
FEATURE [App::DocumentObjectGroupPython] C_element120  label="C_element : 067"  # scripted group (container) (typed FeaturePython)
  n = 5
  ref = C_element
FEATURE [App::DocumentObjectGroupPython] H_element108  label="H_element : 058"  # scripted group (container) (typed FeaturePython)
  n = 11
  ref = H_element
FEATURE [App::DocumentObjectGroupPython] N_element047  label="N_element : 020"  # scripted group (container) (typed FeaturePython)
  n = 1
  ref = N_element
FEATURE [App::DocumentObjectGroupPython] O_element102  label="O_element : 056"  # scripted group (container) (typed FeaturePython)
  n = 2
  ref = O_element
FEATURE [App::DocumentObjectGroupPython] G4_VALINE  # scripted group (container) (typed FeaturePython)
  Dunit = g/cm3
  Dvalue = 1.23
  Group = -> [C_element120,H_element108,N_element047,O_element102]
  conduct = 2
  density = 1
  expand = 3
  formula = G4_VALINE
  name = G4_VALINE
  specific = 4
FEATURE [App::DocumentObjectGroupPython] H_element109  label="H_element : 0.009"  # scripted group (container) (typed FeaturePython)
  n = 0.009417
FEATURE [App::DocumentObjectGroupPython] C_element121  label="C_element : 0.281"  # scripted group (container) (typed FeaturePython)
  n = 0.280555
FEATURE [App::DocumentObjectGroupPython] F_element018  label="F_element : 0.710"  # scripted group (container) (typed FeaturePython)
  n = 0.710028
FEATURE [App::DocumentObjectGroupPython] G4_VITON  # scripted group (container) (typed FeaturePython)
  Dunit = g/cm3
  Dvalue = 1.8
  Group = -> [H_element109,C_element121,F_element018]
  conduct = 2
  density = 1
  expand = 3
  formula = G4_VITON
  name = G4_VITON
  specific = 4
FEATURE [App::DocumentObjectGroupPython] H_element110  label="H_element : 059"  # scripted group (container) (typed FeaturePython)
  n = 2
  ref = H_element
FEATURE [App::DocumentObjectGroupPython] O_element103  label="O_element : 057"  # scripted group (container) (typed FeaturePython)
  n = 1
  ref = O_element
FEATURE [App::DocumentObjectGroupPython] G4_WATER  # scripted group (container) (typed FeaturePython)
  Dunit = g/cm3
  Dvalue = 1
  Group = -> [H_element110,O_element103]
  conduct = 2
  density = 1
  expand = 3
  formula = G4_WATER
  name = G4_WATER
  specific = 4
FEATURE [App::DocumentObjectGroupPython] H_element111  label="H_element : 060"  # scripted group (container) (typed FeaturePython)
  n = 2
  ref = H_element
FEATURE [App::DocumentObjectGroupPython] O_element104  label="O_element : 058"  # scripted group (container) (typed FeaturePython)
  n = 1
  ref = O_element
FEATURE [App::DocumentObjectGroupPython] G4_WATER_VAPOR  # scripted group (container) (typed FeaturePython)
  Dunit = g/cm3
  Dvalue = 0.000756182
  Group = -> [H_element111,O_element104]
  conduct = 2
  density = 1
  expand = 3
  formula = G4_WATER_VAPOR
  name = G4_WATER_VAPOR
  specific = 4
FEATURE [App::DocumentObjectGroupPython] C_element122  label="C_element : 068"  # scripted group (container) (typed FeaturePython)
  n = 8
  ref = C_element
FEATURE [App::DocumentObjectGroupPython] H_element112  label="H_element : 061"  # scripted group (container) (typed FeaturePython)
  n = 10
  ref = H_element
FEATURE [App::DocumentObjectGroupPython] G4_XYLENE  # scripted group (container) (typed FeaturePython)
  Dunit = g/cm3
  Dvalue = 0.87
  Group = -> [C_element122,H_element112]
  conduct = 2
  density = 1
  expand = 3
  formula = G4_XYLENE
  name = G4_XYLENE
  specific = 4
FEATURE [App::DocumentObjectGroupPython] C_element123  label="C_element : 069"  # scripted group (container) (typed FeaturePython)
  n = 1
  ref = C_element
FEATURE [App::DocumentObjectGroupPython] G4_GRAPHITE  # scripted group (container) (typed FeaturePython)
  Dunit = g/cm3
  Dvalue = 2.21
  Group = -> [C_element123]
  conduct = 2
  density = 1
  expand = 3
  formula = G4_GRAPHITE
  name = G4_GRAPHITE
  specific = 4
FEATURE [App::DocumentObjectGroupPython] NIST  # scripted group (container) (typed FeaturePython)
  Group = -> [G4_A_150_TISSUE,G4_ACETONE,G4_ACETYLENE,G4_ADENINE,G4_ADIPOSE_TISSUE_ICRP,G4_AIR001,G4_ALANINE,G4_ALUMINUM_OXIDE,G4_AMBER,G4_AMMONIA,G4_ANILINE,G4_ANTHRACENE,G4_B_100_BONE,G4_BAKELITE,G4_BARIUM_FLUORIDE,G4_BARIUM_SULFATE,G4_BENZENE,G4_BERYLLIUM_OXIDE,G4_BGO,G4_BLOOD_ICRP,G4_BONE_COMPACT_ICRU,G4_BONE_CORTICAL_ICRP,G4_BORON_CARBIDE,G4_BORON_OXIDE,G4_BRAIN_ICRP,G4_BUTANE,G4_N_BUTYL_ALCOHOL,G4_C_552,+152 more]
FEATURE [App::DocumentObjectGroupPython] H_element113  label="H_element : 062"  # scripted group (container) (typed FeaturePython)
  n = 1
  ref = H_element
FEATURE [App::DocumentObjectGroupPython] G4_H  # scripted group (container) (typed FeaturePython)
  Dunit = g/cm3
  Dvalue = 8.3748e-05
  Group = -> [H_element113]
  conduct = 2
  density = 1
  expand = 3
  formula = H
  name = G4_H
  specific = 4
FEATURE [App::DocumentObjectGroupPython] He_element001  label="He_element : 1"  # scripted group (container) (typed FeaturePython)
  n = 1
  ref = He_element
FEATURE [App::DocumentObjectGroupPython] G4_He  # scripted group (container) (typed FeaturePython)
  Dunit = g/cm3
  Dvalue = 0.000166322
  Group = -> [He_element001]
  conduct = 2
  density = 1
  expand = 3
  formula = He
  name = G4_He
  specific = 4
FEATURE [App::DocumentObjectGroupPython] Li_element008  label="Li_element : 008"  # scripted group (container) (typed FeaturePython)
  n = 1
  ref = Li_element
FEATURE [App::DocumentObjectGroupPython] G4_Li  # scripted group (container) (typed FeaturePython)
  Dunit = g/cm3
  Dvalue = 0.534
  Group = -> [Li_element008]
  conduct = 2
  density = 1
  expand = 3
  formula = Li
  name = G4_Li
  specific = 4
FEATURE [App::DocumentObjectGroupPython] Be_element002  label="Be_element : 002"  # scripted group (container) (typed FeaturePython)
  n = 1
  ref = Be_element
FEATURE [App::DocumentObjectGroupPython] G4_Be  # scripted group (container) (typed FeaturePython)
  Dunit = g/cm3
  Dvalue = 1.848
  Group = -> [Be_element002]
  conduct = 2
  density = 1
  expand = 3
  formula = Be
  name = G4_Be
  specific = 4
FEATURE [App::DocumentObjectGroupPython] B_element007  label="B_element : 007"  # scripted group (container) (typed FeaturePython)
  n = 1
  ref = B_element
FEATURE [App::DocumentObjectGroupPython] G4_B  # scripted group (container) (typed FeaturePython)
  Dunit = g/cm3
  Dvalue = 2.37
  Group = -> [B_element007]
  conduct = 2
  density = 1
  expand = 3
  formula = B
  name = G4_B
  specific = 4
FEATURE [App::DocumentObjectGroupPython] C_element124  label="C_element : 070"  # scripted group (container) (typed FeaturePython)
  n = 1
  ref = C_element
FEATURE [App::DocumentObjectGroupPython] G4_C  # scripted group (container) (typed FeaturePython)
  Dunit = g/cm3
  Dvalue = 2
  Group = -> [C_element124]
  conduct = 2
  density = 1
  expand = 3
  formula = C
  name = G4_C
  specific = 4
FEATURE [App::DocumentObjectGroupPython] N_element048  label="N_element : 021"  # scripted group (container) (typed FeaturePython)
  n = 1
  ref = N_element
FEATURE [App::DocumentObjectGroupPython] G4_N  # scripted group (container) (typed FeaturePython)
  Dunit = g/cm3
  Dvalue = 0.0011652
  Group = -> [N_element048]
  conduct = 2
  density = 1
  expand = 3
  formula = N
  name = G4_N
  specific = 4
FEATURE [App::DocumentObjectGroupPython] O_element105  label="O_element : 059"  # scripted group (container) (typed FeaturePython)
  n = 1
  ref = O_element
FEATURE [App::DocumentObjectGroupPython] G4_O  # scripted group (container) (typed FeaturePython)
  Dunit = g/cm3
  Dvalue = 0.00133151
  Group = -> [O_element105]
  conduct = 2
  density = 1
  expand = 3
  formula = O
  name = G4_O
  specific = 4
FEATURE [App::DocumentObjectGroupPython] F_element019  label="F_element : 008"  # scripted group (container) (typed FeaturePython)
  n = 1
  ref = F_element
FEATURE [App::DocumentObjectGroupPython] G4_F  # scripted group (container) (typed FeaturePython)
  Dunit = g/cm3
  Dvalue = 0.00158029
  Group = -> [F_element019]
  conduct = 2
  density = 1
  expand = 3
  formula = F
  name = G4_F
  specific = 4
FEATURE [App::DocumentObjectGroupPython] Ne_element001  label="Ne_element : 1"  # scripted group (container) (typed FeaturePython)
  n = 1
  ref = Ne_element
FEATURE [App::DocumentObjectGroupPython] G4_Ne  # scripted group (container) (typed FeaturePython)
  Dunit = g/cm3
  Dvalue = 0.000838505
  Group = -> [Ne_element001]
  conduct = 2
  density = 1
  expand = 3
  formula = Ne
  name = G4_Ne
  specific = 4
FEATURE [App::DocumentObjectGroupPython] Na_element020  label="Na_element : 005"  # scripted group (container) (typed FeaturePython)
  n = 1
  ref = Na_element
FEATURE [App::DocumentObjectGroupPython] G4_Na  # scripted group (container) (typed FeaturePython)
  Dunit = g/cm3
  Dvalue = 0.971
  Group = -> [Na_element020]
  conduct = 2
  density = 1
  expand = 3
  formula = Na
  name = G4_Na
  specific = 4
FEATURE [App::DocumentObjectGroupPython] Mg_element011  label="Mg_element : 005"  # scripted group (container) (typed FeaturePython)
  n = 1
  ref = Mg_element
FEATURE [App::DocumentObjectGroupPython] G4_Mg  # scripted group (container) (typed FeaturePython)
  Dunit = g/cm3
  Dvalue = 1.74
  Group = -> [Mg_element011]
  conduct = 2
  density = 1
  expand = 3
  formula = Mg
  name = G4_Mg
  specific = 4
FEATURE [App::DocumentObjectGroupPython] Al_element004  label="Al_element : 1"  # scripted group (container) (typed FeaturePython)
  n = 1
  ref = Al_element
FEATURE [App::DocumentObjectGroupPython] G4_Al  # scripted group (container) (typed FeaturePython)
  Dunit = g/cm3
  Dvalue = 2.699
  Group = -> [Al_element004]
  conduct = 2
  density = 1
  expand = 3
  formula = Al
  name = G4_Al
  specific = 4
FEATURE [App::DocumentObjectGroupPython] Si_element007  label="Si_element : 002"  # scripted group (container) (typed FeaturePython)
  n = 1
  ref = Si_element
FEATURE [App::DocumentObjectGroupPython] G4_Si  # scripted group (container) (typed FeaturePython)
  Dunit = g/cm3
  Dvalue = 2.33
  Group = -> [Si_element007]
  conduct = 2
  density = 1
  expand = 3
  formula = Si
  name = G4_Si
  specific = 4
FEATURE [App::DocumentObjectGroupPython] P_element013  label="P_element : 002"  # scripted group (container) (typed FeaturePython)
  n = 1
  ref = P_element
FEATURE [App::DocumentObjectGroupPython] G4_P  # scripted group (container) (typed FeaturePython)
  Dunit = g/cm3
  Dvalue = 2.2
  Group = -> [P_element013]
  conduct = 2
  density = 1
  expand = 3
  formula = P
  name = G4_P
  specific = 4
FEATURE [App::DocumentObjectGroupPython] S_element023  label="S_element : 007"  # scripted group (container) (typed FeaturePython)
  n = 1
  ref = S_element
FEATURE [App::DocumentObjectGroupPython] G4_S  # scripted group (container) (typed FeaturePython)
  Dunit = g/cm3
  Dvalue = 2
  Group = -> [S_element023]
  conduct = 2
  density = 1
  expand = 3
  formula = S
  name = G4_S
  specific = 4
FEATURE [App::DocumentObjectGroupPython] Cl_element029  label="Cl_element : 015"  # scripted group (container) (typed FeaturePython)
  n = 1
  ref = Cl_element
FEATURE [App::DocumentObjectGroupPython] G4_Cl  # scripted group (container) (typed FeaturePython)
  Dunit = g/cm3
  Dvalue = 0.00299473
  Group = -> [Cl_element029]
  conduct = 2
  density = 1
  expand = 3
  formula = Cl
  name = G4_Cl
  specific = 4
FEATURE [App::DocumentObjectGroupPython] Ar_element002  label="Ar_element : 1"  # scripted group (container) (typed FeaturePython)
  n = 1
  ref = Ar_element
FEATURE [App::DocumentObjectGroupPython] G4_Ar  # scripted group (container) (typed FeaturePython)
  Dunit = g/cm3
  Dvalue = 0.00166201
  Group = -> [Ar_element002]
  conduct = 2
  density = 1
  expand = 3
  formula = Ar
  name = G4_Ar
  specific = 4
FEATURE [App::DocumentObjectGroupPython] K_element013  label="K_element : 003"  # scripted group (container) (typed FeaturePython)
  n = 1
  ref = K_element
FEATURE [App::DocumentObjectGroupPython] G4_K  # scripted group (container) (typed FeaturePython)
  Dunit = g/cm3
  Dvalue = 0.862
  Group = -> [K_element013]
  conduct = 2
  density = 1
  expand = 3
  formula = K
  name = G4_K
  specific = 4
FEATURE [App::DocumentObjectGroupPython] Ca_element014  label="Ca_element : 007"  # scripted group (container) (typed FeaturePython)
  n = 1
  ref = Ca_element
FEATURE [App::DocumentObjectGroupPython] G4_Ca  # scripted group (container) (typed FeaturePython)
  Dunit = g/cm3
  Dvalue = 1.55
  Group = -> [Ca_element014]
  conduct = 2
  density = 1
  expand = 3
  formula = Ca
  name = G4_Ca
  specific = 4
FEATURE [App::DocumentObjectGroupPython] Sc_element001  label="Sc_element : 1"  # scripted group (container) (typed FeaturePython)
  n = 1
  ref = Sc_element
FEATURE [App::DocumentObjectGroupPython] G4_Sc  # scripted group (container) (typed FeaturePython)
  Dunit = g/cm3
  Dvalue = 2.989
  Group = -> [Sc_element001]
  conduct = 2
  density = 1
  expand = 3
  formula = Sc
  name = G4_Sc
  specific = 4
FEATURE [App::DocumentObjectGroupPython] Ti_element004  label="Ti_element : 002"  # scripted group (container) (typed FeaturePython)
  n = 1
  ref = Ti_element
FEATURE [App::DocumentObjectGroupPython] G4_Ti  # scripted group (container) (typed FeaturePython)
  Dunit = g/cm3
  Dvalue = 4.54
  Group = -> [Ti_element004]
  conduct = 2
  density = 1
  expand = 3
  formula = Ti
  name = G4_Ti
  specific = 4
FEATURE [App::DocumentObjectGroupPython] V_element001  label="V_element : 1"  # scripted group (container) (typed FeaturePython)
  n = 1
  ref = V_element
FEATURE [App::DocumentObjectGroupPython] G4_V  # scripted group (container) (typed FeaturePython)
  Dunit = g/cm3
  Dvalue = 6.11
  Group = -> [V_element001]
  conduct = 2
  density = 1
  expand = 3
  formula = V
  name = G4_V
  specific = 4
FEATURE [App::DocumentObjectGroupPython] Cr_element001  label="Cr_element : 1"  # scripted group (container) (typed FeaturePython)
  n = 1
  ref = Cr_element
FEATURE [App::DocumentObjectGroupPython] G4_Cr  # scripted group (container) (typed FeaturePython)
  Dunit = g/cm3
  Dvalue = 7.18
  Group = -> [Cr_element001]
  conduct = 2
  density = 1
  expand = 3
  formula = Cr
  name = G4_Cr
  specific = 4
FEATURE [App::DocumentObjectGroupPython] Mn_element001  label="Mn_element : 1"  # scripted group (container) (typed FeaturePython)
  n = 1
  ref = Mn_element
FEATURE [App::DocumentObjectGroupPython] G4_Mn  # scripted group (container) (typed FeaturePython)
  Dunit = g/cm3
  Dvalue = 7.44
  Group = -> [Mn_element001]
  conduct = 2
  density = 1
  expand = 3
  formula = Mn
  name = G4_Mn
  specific = 4
FEATURE [App::DocumentObjectGroupPython] Fe_element007  label="Fe_element : 004"  # scripted group (container) (typed FeaturePython)
  n = 1
  ref = Fe_element
FEATURE [App::DocumentObjectGroupPython] G4_Fe  # scripted group (container) (typed FeaturePython)
  Dunit = g/cm3
  Dvalue = 7.874
  Group = -> [Fe_element007]
  conduct = 2
  density = 1
  expand = 3
  formula = Fe
  name = G4_Fe
  specific = 4
FEATURE [App::DocumentObjectGroupPython] Co_element001  label="Co_element : 1"  # scripted group (container) (typed FeaturePython)
  n = 1
  ref = Co_element
FEATURE [App::DocumentObjectGroupPython] G4_Co  # scripted group (container) (typed FeaturePython)
  Dunit = g/cm3
  Dvalue = 8.9
  Group = -> [Co_element001]
  conduct = 2
  density = 1
  expand = 3
  formula = Co
  name = G4_Co
  specific = 4
FEATURE [App::DocumentObjectGroupPython] Ni_element001  label="Ni_element : 1"  # scripted group (container) (typed FeaturePython)
  n = 1
  ref = Ni_element
FEATURE [App::DocumentObjectGroupPython] G4_Ni  # scripted group (container) (typed FeaturePython)
  Dunit = g/cm3
  Dvalue = 8.902
  Group = -> [Ni_element001]
  conduct = 2
  density = 1
  expand = 3
  formula = Ni
  name = G4_Ni
  specific = 4
FEATURE [App::DocumentObjectGroupPython] Cu_element001  label="Cu_element : 1"  # scripted group (container) (typed FeaturePython)
  n = 1
  ref = Cu_element
FEATURE [App::DocumentObjectGroupPython] G4_Cu  # scripted group (container) (typed FeaturePython)
  Dunit = g/cm3
  Dvalue = 8.96
  Group = -> [Cu_element001]
  conduct = 2
  density = 1
  expand = 3
  formula = Cu
  name = G4_Cu
  specific = 4
FEATURE [App::DocumentObjectGroupPython] Zn_element001  label="Zn_element : 1"  # scripted group (container) (typed FeaturePython)
  n = 1
  ref = Zn_element
FEATURE [App::DocumentObjectGroupPython] G4_Zn  # scripted group (container) (typed FeaturePython)
  Dunit = g/cm3
  Dvalue = 7.133
  Group = -> [Zn_element001]
  conduct = 2
  density = 1
  expand = 3
  formula = Zn
  name = G4_Zn
  specific = 4
FEATURE [App::DocumentObjectGroupPython] Ga_element002  label="Ga_element : 002"  # scripted group (container) (typed FeaturePython)
  n = 1
  ref = Ga_element
FEATURE [App::DocumentObjectGroupPython] G4_Ga  # scripted group (container) (typed FeaturePython)
  Dunit = g/cm3
  Dvalue = 5.904
  Group = -> [Ga_element002]
  conduct = 2
  density = 1
  expand = 3
  formula = Ga
  name = G4_Ga
  specific = 4
FEATURE [App::DocumentObjectGroupPython] Ge_element002  label="Ge_element : 1"  # scripted group (container) (typed FeaturePython)
  n = 1
  ref = Ge_element
FEATURE [App::DocumentObjectGroupPython] G4_Ge  # scripted group (container) (typed FeaturePython)
  Dunit = g/cm3
  Dvalue = 5.323
  Group = -> [Ge_element002]
  conduct = 2
  density = 1
  expand = 3
  formula = Ge
  name = G4_Ge
  specific = 4
FEATURE [App::DocumentObjectGroupPython] As_element003  label="As_element : 002"  # scripted group (container) (typed FeaturePython)
  n = 1
  ref = As_element
FEATURE [App::DocumentObjectGroupPython] G4_As  # scripted group (container) (typed FeaturePython)
  Dunit = g/cm3
  Dvalue = 5.73
  Group = -> [As_element003]
  conduct = 2
  density = 1
  expand = 3
  formula = As
  name = G4_As
  specific = 4
FEATURE [App::DocumentObjectGroupPython] Se_element001  label="Se_element : 1"  # scripted group (container) (typed FeaturePython)
  n = 1
  ref = Se_element
FEATURE [App::DocumentObjectGroupPython] G4_Se  # scripted group (container) (typed FeaturePython)
  Dunit = g/cm3
  Dvalue = 4.5
  Group = -> [Se_element001]
  conduct = 2
  density = 1
  expand = 3
  formula = Se
  name = G4_Se
  specific = 4
FEATURE [App::DocumentObjectGroupPython] Br_element007  label="Br_element : 004"  # scripted group (container) (typed FeaturePython)
  n = 1
  ref = Br_element
FEATURE [App::DocumentObjectGroupPython] G4_Br  # scripted group (container) (typed FeaturePython)
  Dunit = g/cm3
  Dvalue = 0.0070721
  Group = -> [Br_element007]
  conduct = 2
  density = 1
  expand = 3
  formula = Br
  name = G4_Br
  specific = 4
FEATURE [App::DocumentObjectGroupPython] Kr_element001  label="Kr_element : 1"  # scripted group (container) (typed FeaturePython)
  n = 1
  ref = Kr_element
FEATURE [App::DocumentObjectGroupPython] G4_Kr  # scripted group (container) (typed FeaturePython)
  Dunit = g/cm3
  Dvalue = 0.00347832
  Group = -> [Kr_element001]
  conduct = 2
  density = 1
  expand = 3
  formula = Kr
  name = G4_Kr
  specific = 4
FEATURE [App::DocumentObjectGroupPython] Rb_element001  label="Rb_element : 1"  # scripted group (container) (typed FeaturePython)
  n = 1
  ref = Rb_element
FEATURE [App::DocumentObjectGroupPython] G4_Rb  # scripted group (container) (typed FeaturePython)
  Dunit = g/cm3
  Dvalue = 1.532
  Group = -> [Rb_element001]
  conduct = 2
  density = 1
  expand = 3
  formula = Rb
  name = G4_Rb
  specific = 4
FEATURE [App::DocumentObjectGroupPython] Sr_element001  label="Sr_element : 1"  # scripted group (container) (typed FeaturePython)
  n = 1
  ref = Sr_element
FEATURE [App::DocumentObjectGroupPython] G4_Sr  # scripted group (container) (typed FeaturePython)
  Dunit = g/cm3
  Dvalue = 2.54
  Group = -> [Sr_element001]
  conduct = 2
  density = 1
  expand = 3
  formula = Sr
  name = G4_Sr
  specific = 4
FEATURE [App::DocumentObjectGroupPython] Y_element001  label="Y_element : 1"  # scripted group (container) (typed FeaturePython)
  n = 1
  ref = Y_element
FEATURE [App::DocumentObjectGroupPython] G4_Y  # scripted group (container) (typed FeaturePython)
  Dunit = g/cm3
  Dvalue = 4.469
  Group = -> [Y_element001]
  conduct = 2
  density = 1
  expand = 3
  formula = Y
  name = G4_Y
  specific = 4
FEATURE [App::DocumentObjectGroupPython] Zr_element001  label="Zr_element : 1"  # scripted group (container) (typed FeaturePython)
  n = 1
  ref = Zr_element
FEATURE [App::DocumentObjectGroupPython] G4_Zr  # scripted group (container) (typed FeaturePython)
  Dunit = g/cm3
  Dvalue = 6.506
  Group = -> [Zr_element001]
  conduct = 2
  density = 1
  expand = 3
  formula = Zr
  name = G4_Zr
  specific = 4
FEATURE [App::DocumentObjectGroupPython] Nb_element001  label="Nb_element : 1"  # scripted group (container) (typed FeaturePython)
  n = 1
  ref = Nb_element
FEATURE [App::DocumentObjectGroupPython] G4_Nb  # scripted group (container) (typed FeaturePython)
  Dunit = g/cm3
  Dvalue = 8.57
  Group = -> [Nb_element001]
  conduct = 2
  density = 1
  expand = 3
  formula = Nb
  name = G4_Nb
  specific = 4
FEATURE [App::DocumentObjectGroupPython] Mo_element001  label="Mo_element : 1"  # scripted group (container) (typed FeaturePython)
  n = 1
  ref = Mo_element
FEATURE [App::DocumentObjectGroupPython] G4_Mo  # scripted group (container) (typed FeaturePython)
  Dunit = g/cm3
  Dvalue = 10.22
  Group = -> [Mo_element001]
  conduct = 2
  density = 1
  expand = 3
  formula = Mo
  name = G4_Mo
  specific = 4
FEATURE [App::DocumentObjectGroupPython] Tc_element001  label="Tc_element : 1"  # scripted group (container) (typed FeaturePython)
  n = 1
  ref = Tc_element
FEATURE [App::DocumentObjectGroupPython] G4_Tc  # scripted group (container) (typed FeaturePython)
  Dunit = g/cm3
  Dvalue = 11.5
  Group = -> [Tc_element001]
  conduct = 2
  density = 1
  expand = 3
  formula = Tc
  name = G4_Tc
  specific = 4
FEATURE [App::DocumentObjectGroupPython] Ru_element001  label="Ru_element : 1"  # scripted group (container) (typed FeaturePython)
  n = 1
  ref = Ru_element
FEATURE [App::DocumentObjectGroupPython] G4_Ru  # scripted group (container) (typed FeaturePython)
  Dunit = g/cm3
  Dvalue = 12.41
  Group = -> [Ru_element001]
  conduct = 2
  density = 1
  expand = 3
  formula = Ru
  name = G4_Ru
  specific = 4
FEATURE [App::DocumentObjectGroupPython] Rh_element001  label="Rh_element : 1"  # scripted group (container) (typed FeaturePython)
  n = 1
  ref = Rh_element
FEATURE [App::DocumentObjectGroupPython] G4_Rh  # scripted group (container) (typed FeaturePython)
  Dunit = g/cm3
  Dvalue = 12.41
  Group = -> [Rh_element001]
  conduct = 2
  density = 1
  expand = 3
  formula = Rh
  name = G4_Rh
  specific = 4
FEATURE [App::DocumentObjectGroupPython] Pd_element001  label="Pd_element : 1"  # scripted group (container) (typed FeaturePython)
  n = 1
  ref = Pd_element
FEATURE [App::DocumentObjectGroupPython] G4_Pd  # scripted group (container) (typed FeaturePython)
  Dunit = g/cm3
  Dvalue = 12.02
  Group = -> [Pd_element001]
  conduct = 2
  density = 1
  expand = 3
  formula = Pd
  name = G4_Pd
  specific = 4
FEATURE [App::DocumentObjectGroupPython] Ag_element006  label="Ag_element : 004"  # scripted group (container) (typed FeaturePython)
  n = 1
  ref = Ag_element
FEATURE [App::DocumentObjectGroupPython] G4_Ag  # scripted group (container) (typed FeaturePython)
  Dunit = g/cm3
  Dvalue = 10.5
  Group = -> [Ag_element006]
  conduct = 2
  density = 1
  expand = 3
  formula = Ag
  name = G4_Ag
  specific = 4
FEATURE [App::DocumentObjectGroupPython] Cd_element003  label="Cd_element : 003"  # scripted group (container) (typed FeaturePython)
  n = 1
  ref = Cd_element
FEATURE [App::DocumentObjectGroupPython] G4_Cd  # scripted group (container) (typed FeaturePython)
  Dunit = g/cm3
  Dvalue = 8.65
  Group = -> [Cd_element003]
  conduct = 2
  density = 1
  expand = 3
  formula = Cd
  name = G4_Cd
  specific = 4
FEATURE [App::DocumentObjectGroupPython] In_element001  label="In_element : 1"  # scripted group (container) (typed FeaturePython)
  n = 1
  ref = In_element
FEATURE [App::DocumentObjectGroupPython] G4_In  # scripted group (container) (typed FeaturePython)
  Dunit = g/cm3
  Dvalue = 7.31
  Group = -> [In_element001]
  conduct = 2
  density = 1
  expand = 3
  formula = In
  name = G4_In
  specific = 4
FEATURE [App::DocumentObjectGroupPython] Sn_element001  label="Sn_element : 1"  # scripted group (container) (typed FeaturePython)
  n = 1
  ref = Sn_element
FEATURE [App::DocumentObjectGroupPython] G4_Sn  # scripted group (container) (typed FeaturePython)
  Dunit = g/cm3
  Dvalue = 7.31
  Group = -> [Sn_element001]
  conduct = 2
  density = 1
  expand = 3
  formula = Sn
  name = G4_Sn
  specific = 4
FEATURE [App::DocumentObjectGroupPython] Sb_element001  label="Sb_element : 1"  # scripted group (container) (typed FeaturePython)
  n = 1
  ref = Sb_element
FEATURE [App::DocumentObjectGroupPython] G4_Sb  # scripted group (container) (typed FeaturePython)
  Dunit = g/cm3
  Dvalue = 6.691
  Group = -> [Sb_element001]
  conduct = 2
  density = 1
  expand = 3
  formula = Sb
  name = G4_Sb
  specific = 4
FEATURE [App::DocumentObjectGroupPython] Te_element002  label="Te_element : 002"  # scripted group (container) (typed FeaturePython)
  n = 1
  ref = Te_element
FEATURE [App::DocumentObjectGroupPython] G4_Te  # scripted group (container) (typed FeaturePython)
  Dunit = g/cm3
  Dvalue = 6.24
  Group = -> [Te_element002]
  conduct = 2
  density = 1
  expand = 3
  formula = Te
  name = G4_Te
  specific = 4
FEATURE [App::DocumentObjectGroupPython] I_element010  label="I_element : 006"  # scripted group (container) (typed FeaturePython)
  n = 1
  ref = I_element
FEATURE [App::DocumentObjectGroupPython] G4_I  # scripted group (container) (typed FeaturePython)
  Dunit = g/cm3
  Dvalue = 4.93
  Group = -> [I_element010]
  conduct = 2
  density = 1
  expand = 3
  formula = I
  name = G4_I
  specific = 4
FEATURE [App::DocumentObjectGroupPython] Xe_element001  label="Xe_element : 1"  # scripted group (container) (typed FeaturePython)
  n = 1
  ref = Xe_element
FEATURE [App::DocumentObjectGroupPython] G4_Xe  # scripted group (container) (typed FeaturePython)
  Dunit = g/cm3
  Dvalue = 0.00548536
  Group = -> [Xe_element001]
  conduct = 2
  density = 1
  expand = 3
  formula = Xe
  name = G4_Xe
  specific = 4
FEATURE [App::DocumentObjectGroupPython] Cs_element003  label="Cs_element : 003"  # scripted group (container) (typed FeaturePython)
  n = 1
  ref = Cs_element
FEATURE [App::DocumentObjectGroupPython] G4_Cs  # scripted group (container) (typed FeaturePython)
  Dunit = g/cm3
  Dvalue = 1.873
  Group = -> [Cs_element003]
  conduct = 2
  density = 1
  expand = 3
  formula = Cs
  name = G4_Cs
  specific = 4
FEATURE [App::DocumentObjectGroupPython] Ba_element003  label="Ba_element : 003"  # scripted group (container) (typed FeaturePython)
  n = 1
  ref = Ba_element
FEATURE [App::DocumentObjectGroupPython] G4_Ba  # scripted group (container) (typed FeaturePython)
  Dunit = g/cm3
  Dvalue = 3.5
  Group = -> [Ba_element003]
  conduct = 2
  density = 1
  expand = 3
  formula = Ba
  name = G4_Ba
  specific = 4
FEATURE [App::DocumentObjectGroupPython] La_element003  label="La_element : 003"  # scripted group (container) (typed FeaturePython)
  n = 1
  ref = La_element
FEATURE [App::DocumentObjectGroupPython] G4_La  # scripted group (container) (typed FeaturePython)
  Dunit = g/cm3
  Dvalue = 6.154
  Group = -> [La_element003]
  conduct = 2
  density = 1
  expand = 3
  formula = La
  name = G4_La
  specific = 4
FEATURE [App::DocumentObjectGroupPython] Ce_element002  label="Ce_element : 1"  # scripted group (container) (typed FeaturePython)
  n = 1
  ref = Ce_element
FEATURE [App::DocumentObjectGroupPython] G4_Ce  # scripted group (container) (typed FeaturePython)
  Dunit = g/cm3
  Dvalue = 6.657
  Group = -> [Ce_element002]
  conduct = 2
  density = 1
  expand = 3
  formula = Ce
  name = G4_Ce
  specific = 4
FEATURE [App::DocumentObjectGroupPython] Pr_element001  label="Pr_element : 1"  # scripted group (container) (typed FeaturePython)
  n = 1
  ref = Pr_element
FEATURE [App::DocumentObjectGroupPython] G4_Pr  # scripted group (container) (typed FeaturePython)
  Dunit = g/cm3
  Dvalue = 6.71
  Group = -> [Pr_element001]
  conduct = 2
  density = 1
  expand = 3
  formula = Pr
  name = G4_Pr
  specific = 4
FEATURE [App::DocumentObjectGroupPython] Nd_element001  label="Nd_element : 1"  # scripted group (container) (typed FeaturePython)
  n = 1
  ref = Nd_element
FEATURE [App::DocumentObjectGroupPython] G4_Nd  # scripted group (container) (typed FeaturePython)
  Dunit = g/cm3
  Dvalue = 6.9
  Group = -> [Nd_element001]
  conduct = 2
  density = 1
  expand = 3
  formula = Nd
  name = G4_Nd
  specific = 4
FEATURE [App::DocumentObjectGroupPython] Pm_element001  label="Pm_element : 1"  # scripted group (container) (typed FeaturePython)
  n = 1
  ref = Pm_element
FEATURE [App::DocumentObjectGroupPython] G4_Pm  # scripted group (container) (typed FeaturePython)
  Dunit = g/cm3
  Dvalue = 7.22
  Group = -> [Pm_element001]
  conduct = 2
  density = 1
  expand = 3
  formula = Pm
  name = G4_Pm
  specific = 4
FEATURE [App::DocumentObjectGroupPython] Sm_element001  label="Sm_element : 1"  # scripted group (container) (typed FeaturePython)
  n = 1
  ref = Sm_element
FEATURE [App::DocumentObjectGroupPython] G4_Sm  # scripted group (container) (typed FeaturePython)
  Dunit = g/cm3
  Dvalue = 7.46
  Group = -> [Sm_element001]
  conduct = 2
  density = 1
  expand = 3
  formula = Sm
  name = G4_Sm
  specific = 4
FEATURE [App::DocumentObjectGroupPython] Eu_element001  label="Eu_element : 1"  # scripted group (container) (typed FeaturePython)
  n = 1
  ref = Eu_element
FEATURE [App::DocumentObjectGroupPython] G4_Eu  # scripted group (container) (typed FeaturePython)
  Dunit = g/cm3
  Dvalue = 5.243
  Group = -> [Eu_element001]
  conduct = 2
  density = 1
  expand = 3
  formula = Eu
  name = G4_Eu
  specific = 4
FEATURE [App::DocumentObjectGroupPython] Gd_element002  label="Gd_element : 1"  # scripted group (container) (typed FeaturePython)
  n = 1
  ref = Gd_element
FEATURE [App::DocumentObjectGroupPython] G4_Gd  # scripted group (container) (typed FeaturePython)
  Dunit = g/cm3
  Dvalue = 7.9004
  Group = -> [Gd_element002]
  conduct = 2
  density = 1
  expand = 3
  formula = Gd
  name = G4_Gd
  specific = 4
FEATURE [App::DocumentObjectGroupPython] Tb_element001  label="Tb_element : 1"  # scripted group (container) (typed FeaturePython)
  n = 1
  ref = Tb_element
FEATURE [App::DocumentObjectGroupPython] G4_Tb  # scripted group (container) (typed FeaturePython)
  Dunit = g/cm3
  Dvalue = 8.229
  Group = -> [Tb_element001]
  conduct = 2
  density = 1
  expand = 3
  formula = Tb
  name = G4_Tb
  specific = 4
FEATURE [App::DocumentObjectGroupPython] Dy_element001  label="Dy_element : 1"  # scripted group (container) (typed FeaturePython)
  n = 1
  ref = Dy_element
FEATURE [App::DocumentObjectGroupPython] G4_Dy  # scripted group (container) (typed FeaturePython)
  Dunit = g/cm3
  Dvalue = 8.55
  Group = -> [Dy_element001]
  conduct = 2
  density = 1
  expand = 3
  formula = Dy
  name = G4_Dy
  specific = 4
FEATURE [App::DocumentObjectGroupPython] Ho_element001  label="Ho_element : 1"  # scripted group (container) (typed FeaturePython)
  n = 1
  ref = Ho_element
FEATURE [App::DocumentObjectGroupPython] G4_Ho  # scripted group (container) (typed FeaturePython)
  Dunit = g/cm3
  Dvalue = 8.795
  Group = -> [Ho_element001]
  conduct = 2
  density = 1
  expand = 3
  formula = Ho
  name = G4_Ho
  specific = 4
FEATURE [App::DocumentObjectGroupPython] Er_element001  label="Er_element : 1"  # scripted group (container) (typed FeaturePython)
  n = 1
  ref = Er_element
FEATURE [App::DocumentObjectGroupPython] G4_Er  # scripted group (container) (typed FeaturePython)
  Dunit = g/cm3
  Dvalue = 9.066
  Group = -> [Er_element001]
  conduct = 2
  density = 1
  expand = 3
  formula = Er
  name = G4_Er
  specific = 4
FEATURE [App::DocumentObjectGroupPython] Tm_element001  label="Tm_element : 1"  # scripted group (container) (typed FeaturePython)
  n = 1
  ref = Tm_element
FEATURE [App::DocumentObjectGroupPython] G4_Tm  # scripted group (container) (typed FeaturePython)
  Dunit = g/cm3
  Dvalue = 9.321
  Group = -> [Tm_element001]
  conduct = 2
  density = 1
  expand = 3
  formula = Tm
  name = G4_Tm
  specific = 4
FEATURE [App::DocumentObjectGroupPython] Yb_element001  label="Yb_element : 1"  # scripted group (container) (typed FeaturePython)
  n = 1
  ref = Yb_element
FEATURE [App::DocumentObjectGroupPython] G4_Yb  # scripted group (container) (typed FeaturePython)
  Dunit = g/cm3
  Dvalue = 6.73
  Group = -> [Yb_element001]
  conduct = 2
  density = 1
  expand = 3
  formula = Yb
  name = G4_Yb
  specific = 4
FEATURE [App::DocumentObjectGroupPython] Lu_element001  label="Lu_element : 1"  # scripted group (container) (typed FeaturePython)
  n = 1
  ref = Lu_element
FEATURE [App::DocumentObjectGroupPython] G4_Lu  # scripted group (container) (typed FeaturePython)
  Dunit = g/cm3
  Dvalue = 9.84
  Group = -> [Lu_element001]
  conduct = 2
  density = 1
  expand = 3
  formula = Lu
  name = G4_Lu
  specific = 4
FEATURE [App::DocumentObjectGroupPython] Hf_element001  label="Hf_element : 1"  # scripted group (container) (typed FeaturePython)
  n = 1
  ref = Hf_element
FEATURE [App::DocumentObjectGroupPython] G4_Hf  # scripted group (container) (typed FeaturePython)
  Dunit = g/cm3
  Dvalue = 13.31
  Group = -> [Hf_element001]
  conduct = 2
  density = 1
  expand = 3
  formula = Hf
  name = G4_Hf
  specific = 4
FEATURE [App::DocumentObjectGroupPython] Ta_element001  label="Ta_element : 1"  # scripted group (container) (typed FeaturePython)
  n = 1
  ref = Ta_element
FEATURE [App::DocumentObjectGroupPython] G4_Ta  # scripted group (container) (typed FeaturePython)
  Dunit = g/cm3
  Dvalue = 16.654
  Group = -> [Ta_element001]
  conduct = 2
  density = 1
  expand = 3
  formula = Ta
  name = G4_Ta
  specific = 4
FEATURE [App::DocumentObjectGroupPython] W_element004  label="W_element : 004"  # scripted group (container) (typed FeaturePython)
  n = 1
  ref = W_element
FEATURE [App::DocumentObjectGroupPython] G4_W  # scripted group (container) (typed FeaturePython)
  Dunit = g/cm3
  Dvalue = 19.3
  Group = -> [W_element004]
  conduct = 2
  density = 1
  expand = 3
  formula = W
  name = G4_W
  specific = 4
FEATURE [App::DocumentObjectGroupPython] Re_element001  label="Re_element : 1"  # scripted group (container) (typed FeaturePython)
  n = 1
  ref = Re_element
FEATURE [App::DocumentObjectGroupPython] G4_Re  # scripted group (container) (typed FeaturePython)
  Dunit = g/cm3
  Dvalue = 21.02
  Group = -> [Re_element001]
  conduct = 2
  density = 1
  expand = 3
  formula = Re
  name = G4_Re
  specific = 4
FEATURE [App::DocumentObjectGroupPython] Os_element001  label="Os_element : 1"  # scripted group (container) (typed FeaturePython)
  n = 1
  ref = Os_element
FEATURE [App::DocumentObjectGroupPython] G4_Os  # scripted group (container) (typed FeaturePython)
  Dunit = g/cm3
  Dvalue = 22.57
  Group = -> [Os_element001]
  conduct = 2
  density = 1
  expand = 3
  formula = Os
  name = G4_Os
  specific = 4
FEATURE [App::DocumentObjectGroupPython] Ir_element001  label="Ir_element : 1"  # scripted group (container) (typed FeaturePython)
  n = 1
  ref = Ir_element
FEATURE [App::DocumentObjectGroupPython] G4_Ir  # scripted group (container) (typed FeaturePython)
  Dunit = g/cm3
  Dvalue = 22.42
  Group = -> [Ir_element001]
  conduct = 2
  density = 1
  expand = 3
  formula = Ir
  name = G4_Ir
  specific = 4
FEATURE [App::DocumentObjectGroupPython] Pt_element001  label="Pt_element : 1"  # scripted group (container) (typed FeaturePython)
  n = 1
  ref = Pt_element
FEATURE [App::DocumentObjectGroupPython] G4_Pt  # scripted group (container) (typed FeaturePython)
  Dunit = g/cm3
  Dvalue = 21.45
  Group = -> [Pt_element001]
  conduct = 2
  density = 1
  expand = 3
  formula = Pt
  name = G4_Pt
  specific = 4
FEATURE [App::DocumentObjectGroupPython] Au_element001  label="Au_element : 1"  # scripted group (container) (typed FeaturePython)
  n = 1
  ref = Au_element
FEATURE [App::DocumentObjectGroupPython] G4_Au  # scripted group (container) (typed FeaturePython)
  Dunit = g/cm3
  Dvalue = 19.32
  Group = -> [Au_element001]
  conduct = 2
  density = 1
  expand = 3
  formula = Au
  name = G4_Au
  specific = 4
FEATURE [App::DocumentObjectGroupPython] Hg_element002  label="Hg_element : 002"  # scripted group (container) (typed FeaturePython)
  n = 1
  ref = Hg_element
FEATURE [App::DocumentObjectGroupPython] G4_Hg  # scripted group (container) (typed FeaturePython)
  Dunit = g/cm3
  Dvalue = 13.546
  Group = -> [Hg_element002]
  conduct = 2
  density = 1
  expand = 3
  formula = Hg
  name = G4_Hg
  specific = 4
FEATURE [App::DocumentObjectGroupPython] Tl_element002  label="Tl_element : 002"  # scripted group (container) (typed FeaturePython)
  n = 1
  ref = Tl_element
FEATURE [App::DocumentObjectGroupPython] G4_Tl  # scripted group (container) (typed FeaturePython)
  Dunit = g/cm3
  Dvalue = 11.72
  Group = -> [Tl_element002]
  conduct = 2
  density = 1
  expand = 3
  formula = Tl
  name = G4_Tl
  specific = 4
FEATURE [App::DocumentObjectGroupPython] Pb_element003  label="Pb_element : 1"  # scripted group (container) (typed FeaturePython)
  n = 1
  ref = Pb_element
FEATURE [App::DocumentObjectGroupPython] G4_Pb  # scripted group (container) (typed FeaturePython)
  Dunit = g/cm3
  Dvalue = 11.35
  Group = -> [Pb_element003]
  conduct = 2
  density = 1
  expand = 3
  formula = Pb
  name = G4_Pb
  specific = 4
FEATURE [App::DocumentObjectGroupPython] Bi_element002  label="Bi_element : 1"  # scripted group (container) (typed FeaturePython)
  n = 1
  ref = Bi_element
FEATURE [App::DocumentObjectGroupPython] G4_Bi  # scripted group (container) (typed FeaturePython)
  Dunit = g/cm3
  Dvalue = 9.747
  Group = -> [Bi_element002]
  conduct = 2
  density = 1
  expand = 3
  formula = Bi
  name = G4_Bi
  specific = 4
FEATURE [App::DocumentObjectGroupPython] Po_element001  label="Po_element : 1"  # scripted group (container) (typed FeaturePython)
  n = 1
  ref = Po_element
FEATURE [App::DocumentObjectGroupPython] G4_Po  # scripted group (container) (typed FeaturePython)
  Dunit = g/cm3
  Dvalue = 9.32
  Group = -> [Po_element001]
  conduct = 2
  density = 1
  expand = 3
  formula = Po
  name = G4_Po
  specific = 4
FEATURE [App::DocumentObjectGroupPython] At_element001  label="At_element : 1"  # scripted group (container) (typed FeaturePython)
  n = 1
  ref = At_element
FEATURE [App::DocumentObjectGroupPython] G4_At  # scripted group (container) (typed FeaturePython)
  Dunit = g/cm3
  Dvalue = 9.32
  Group = -> [At_element001]
  conduct = 2
  density = 1
  expand = 3
  formula = At
  name = G4_At
  specific = 4
FEATURE [App::DocumentObjectGroupPython] Rn_element001  label="Rn_element : 1"  # scripted group (container) (typed FeaturePython)
  n = 1
  ref = Rn_element
FEATURE [App::DocumentObjectGroupPython] G4_Rn  # scripted group (container) (typed FeaturePython)
  Dunit = g/cm3
  Dvalue = 0.00900662
  Group = -> [Rn_element001]
  conduct = 2
  density = 1
  expand = 3
  formula = Rn
  name = G4_Rn
  specific = 4
FEATURE [App::DocumentObjectGroupPython] Fr_element001  label="Fr_element : 1"  # scripted group (container) (typed FeaturePython)
  n = 1
  ref = Fr_element
FEATURE [App::DocumentObjectGroupPython] G4_Fr  # scripted group (container) (typed FeaturePython)
  Dunit = g/cm3
  Dvalue = 1
  Group = -> [Fr_element001]
  conduct = 2
  density = 1
  expand = 3
  formula = Fr
  name = G4_Fr
  specific = 4
FEATURE [App::DocumentObjectGroupPython] Ra_element001  label="Ra_element : 1"  # scripted group (container) (typed FeaturePython)
  n = 1
  ref = Ra_element
FEATURE [App::DocumentObjectGroupPython] G4_Ra  # scripted group (container) (typed FeaturePython)
  Dunit = g/cm3
  Dvalue = 5
  Group = -> [Ra_element001]
  conduct = 2
  density = 1
  expand = 3
  formula = Ra
  name = G4_Ra
  specific = 4
FEATURE [App::DocumentObjectGroupPython] Ac_element001  label="Ac_element : 1"  # scripted group (container) (typed FeaturePython)
  n = 1
  ref = Ac_element
FEATURE [App::DocumentObjectGroupPython] G4_Ac  # scripted group (container) (typed FeaturePython)
  Dunit = g/cm3
  Dvalue = 10.07
  Group = -> [Ac_element001]
  conduct = 2
  density = 1
  expand = 3
  formula = Ac
  name = G4_Ac
  specific = 4
FEATURE [App::DocumentObjectGroupPython] Th_element001  label="Th_element : 1"  # scripted group (container) (typed FeaturePython)
  n = 1
  ref = Th_element
FEATURE [App::DocumentObjectGroupPython] G4_Th  # scripted group (container) (typed FeaturePython)
  Dunit = g/cm3
  Dvalue = 11.72
  Group = -> [Th_element001]
  conduct = 2
  density = 1
  expand = 3
  formula = Th
  name = G4_Th
  specific = 4
FEATURE [App::DocumentObjectGroupPython] Pa_element001  label="Pa_element : 1"  # scripted group (container) (typed FeaturePython)
  n = 1
  ref = Pa_element
FEATURE [App::DocumentObjectGroupPython] G4_Pa  # scripted group (container) (typed FeaturePython)
  Dunit = g/cm3
  Dvalue = 15.37
  Group = -> [Pa_element001]
  conduct = 2
  density = 1
  expand = 3
  formula = Pa
  name = G4_Pa
  specific = 4
FEATURE [App::DocumentObjectGroupPython] U_element004  label="U_element : 004"  # scripted group (container) (typed FeaturePython)
  n = 1
  ref = U_element
FEATURE [App::DocumentObjectGroupPython] G4_U  # scripted group (container) (typed FeaturePython)
  Dunit = g/cm3
  Dvalue = 18.95
  Group = -> [U_element004]
  conduct = 2
  density = 1
  expand = 3
  formula = U
  name = G4_U
  specific = 4
FEATURE [App::DocumentObjectGroupPython] Np_element001  label="Np_element : 1"  # scripted group (container) (typed FeaturePython)
  n = 1
  ref = Np_element
FEATURE [App::DocumentObjectGroupPython] G4_Np  # scripted group (container) (typed FeaturePython)
  Dunit = g/cm3
  Dvalue = 20.25
  Group = -> [Np_element001]
  conduct = 2
  density = 1
  expand = 3
  formula = Np
  name = G4_Np
  specific = 4
FEATURE [App::DocumentObjectGroupPython] Pu_element002  label="Pu_element : 002"  # scripted group (container) (typed FeaturePython)
  n = 1
  ref = Pu_element
FEATURE [App::DocumentObjectGroupPython] G4_Pu  # scripted group (container) (typed FeaturePython)
  Dunit = g/cm3
  Dvalue = 19.84
  Group = -> [Pu_element002]
  conduct = 2
  density = 1
  expand = 3
  formula = Pu
  name = G4_Pu
  specific = 4
FEATURE [App::DocumentObjectGroupPython] Am_element001  label="Am_element : 1"  # scripted group (container) (typed FeaturePython)
  n = 1
  ref = Am_element
FEATURE [App::DocumentObjectGroupPython] G4_Am  # scripted group (container) (typed FeaturePython)
  Dunit = g/cm3
  Dvalue = 13.67
  Group = -> [Am_element001]
  conduct = 2
  density = 1
  expand = 3
  formula = Am
  name = G4_Am
  specific = 4
FEATURE [App::DocumentObjectGroupPython] Cm_element001  label="Cm_element : 1"  # scripted group (container) (typed FeaturePython)
  n = 1
  ref = Cm_element
FEATURE [App::DocumentObjectGroupPython] G4_Cm  # scripted group (container) (typed FeaturePython)
  Dunit = g/cm3
  Dvalue = 13.51
  Group = -> [Cm_element001]
  conduct = 2
  density = 1
  expand = 3
  formula = Cm
  name = G4_Cm
  specific = 4
FEATURE [App::DocumentObjectGroupPython] Bk_element001  label="Bk_element : 1"  # scripted group (container) (typed FeaturePython)
  n = 1
  ref = Bk_element
FEATURE [App::DocumentObjectGroupPython] G4_Bk  # scripted group (container) (typed FeaturePython)
  Dunit = g/cm3
  Dvalue = 14
  Group = -> [Bk_element001]
  conduct = 2
  density = 1
  expand = 3
  formula = Bk
  name = G4_Bk
  specific = 4
FEATURE [App::DocumentObjectGroupPython] Cf_element001  label="Cf_element : 1"  # scripted group (container) (typed FeaturePython)
  n = 1
  ref = Cf_element
FEATURE [App::DocumentObjectGroupPython] G4_Cf  # scripted group (container) (typed FeaturePython)
  Dunit = g/cm3
  Dvalue = 10
  Group = -> [Cf_element001]
  conduct = 2
  density = 1
  expand = 3
  formula = Cf
  name = G4_Cf
  specific = 4
FEATURE [App::DocumentObjectGroupPython] Element  # scripted group (container) (typed FeaturePython)
  Group = -> [G4_H,G4_He,G4_Li,G4_Be,G4_B,G4_C,G4_N,G4_O,G4_F,G4_Ne,G4_Na,G4_Mg,G4_Al,G4_Si,G4_P,G4_S,G4_Cl,G4_Ar,G4_K,G4_Ca,G4_Sc,G4_Ti,G4_V,G4_Cr,G4_Mn,G4_Fe,G4_Co,G4_Ni,G4_Cu,G4_Zn,G4_Ga,G4_Ge,G4_As,G4_Se,G4_Br,G4_Kr,G4_Rb,G4_Sr,G4_Y,G4_Zr,G4_Nb,G4_Mo,G4_Tc,G4_Ru,G4_Rh,G4_Pd,G4_Ag,G4_Cd,G4_In,G4_Sn,G4_Sb,G4_Te,G4_I,G4_Xe,G4_Cs,G4_Ba,G4_La,G4_Ce,G4_Pr,G4_Nd,G4_Pm,G4_Sm,G4_Eu,G4_Gd,G4_Tb,G4_Dy,G4_Ho,G4_Er,+30 more]
FEATURE [App::DocumentObjectGroupPython] H_element114  label="H_element : 063"  # scripted group (container) (typed FeaturePython)
  n = 2
  ref = H_element
FEATURE [App::DocumentObjectGroupPython] G4_lH2  # scripted group (container) (typed FeaturePython)
  Dunit = g/cm3
  Dvalue = 0.0708
  Group = -> [H_element114]
  conduct = 2
  density = 1
  expand = 3
  formula = G4_lH2
  name = G4_lH2
  specific = 4
FEATURE [App::DocumentObjectGroupPython] N_element049  label="N_element : 022"  # scripted group (container) (typed FeaturePython)
  n = 2
  ref = N_element
FEATURE [App::DocumentObjectGroupPython] G4_lN2  # scripted group (container) (typed FeaturePython)
  Dunit = g/cm3
  Dvalue = 0.807
  Group = -> [N_element049]
  conduct = 2
  density = 1
  expand = 3
  formula = G4_lN2
  name = G4_lN2
  specific = 4
FEATURE [App::DocumentObjectGroupPython] O_element106  label="O_element : 060"  # scripted group (container) (typed FeaturePython)
  n = 2
  ref = O_element
FEATURE [App::DocumentObjectGroupPython] G4_lO2  # scripted group (container) (typed FeaturePython)
  Dunit = g/cm3
  Dvalue = 1.141
  Group = -> [O_element106]
  conduct = 2
  density = 1
  expand = 3
  formula = G4_lO2
  name = G4_lO2
  specific = 4
FEATURE [App::DocumentObjectGroupPython] Ar  label="Ar : 1"  # scripted group (container) (typed FeaturePython)
  n = 1
  ref = Ar
FEATURE [App::DocumentObjectGroupPython] G4_lAr  # scripted group (container) (typed FeaturePython)
  Dunit = g/cm3
  Dvalue = 1.396
  Group = -> [Ar]
  conduct = 2
  density = 1
  expand = 3
  formula = G4_lAr
  name = G4_lAr
  specific = 4
FEATURE [App::DocumentObjectGroupPython] Br  label="Br : 1"  # scripted group (container) (typed FeaturePython)
  n = 1
  ref = Br
FEATURE [App::DocumentObjectGroupPython] G4_lBr  # scripted group (container) (typed FeaturePython)
  Dunit = g/cm3
  Dvalue = 3.1028
  Group = -> [Br]
  conduct = 2
  density = 1
  expand = 3
  formula = G4_lBr
  name = G4_lBr
  specific = 4
FEATURE [App::DocumentObjectGroupPython] Kr  label="Kr : 1"  # scripted group (container) (typed FeaturePython)
  n = 1
  ref = Kr
FEATURE [App::DocumentObjectGroupPython] G4_lKr  # scripted group (container) (typed FeaturePython)
  Dunit = g/cm3
  Dvalue = 2.418
  Group = -> [Kr]
  conduct = 2
  density = 1
  expand = 3
  formula = G4_lKr
  name = G4_lKr
  specific = 4
FEATURE [App::DocumentObjectGroupPython] Xe  label="Xe : 1"  # scripted group (container) (typed FeaturePython)
  n = 1
  ref = Xe
FEATURE [App::DocumentObjectGroupPython] G4_lXe  # scripted group (container) (typed FeaturePython)
  Dunit = g/cm3
  Dvalue = 2.953
  Group = -> [Xe]
  conduct = 2
  density = 1
  expand = 3
  formula = G4_lXe
  name = G4_lXe
  specific = 4
FEATURE [App::DocumentObjectGroupPython] O_element107  label="O_element : 061"  # scripted group (container) (typed FeaturePython)
  n = 4
  ref = O_element
FEATURE [App::DocumentObjectGroupPython] Pb_element004  label="Pb_element : 002"  # scripted group (container) (typed FeaturePython)
  n = 1
  ref = Pb_element
FEATURE [App::DocumentObjectGroupPython] W_element005  label="W_element : 005"  # scripted group (container) (typed FeaturePython)
  n = 1
  ref = W_element
FEATURE [App::DocumentObjectGroupPython] G4_PbWO4  # scripted group (container) (typed FeaturePython)
  Dunit = g/cm3
  Dvalue = 8.28
  Group = -> [O_element107,Pb_element004,W_element005]
  conduct = 2
  density = 1
  expand = 3
  formula = G4_PbWO4
  name = G4_PbWO4
  specific = 4
FEATURE [App::DocumentObjectGroupPython] alactic  label="alactic : 1"  # scripted group (container) (typed FeaturePython)
  n = 1
  ref = alactic
FEATURE [App::DocumentObjectGroupPython] G4_Galactic  # scripted group (container) (typed FeaturePython)
  Dunit = g/cm3
  Dvalue = 0
  Group = -> [alactic]
  conduct = 2
  density = 1
  expand = 3
  formula = G4_Galactic
  name = G4_Galactic
  specific = 4
FEATURE [App::DocumentObjectGroupPython] RAPHITE_POROUS  label="RAPHITE_POROUS : 1"  # scripted group (container) (typed FeaturePython)
  n = 1
  ref = RAPHITE_POROUS
FEATURE [App::DocumentObjectGroupPython] G4_GRAPHITE_POROUS  # scripted group (container) (typed FeaturePython)
  Dunit = g/cm3
  Dvalue = 1.7
  Group = -> [RAPHITE_POROUS]
  conduct = 2
  density = 1
  expand = 3
  formula = G4_GRAPHITE_POROUS
  name = G4_GRAPHITE_POROUS
  specific = 4
FEATURE [App::DocumentObjectGroupPython] H_element115  label="H_element : 0.150"  # scripted group (container) (typed FeaturePython)
  n = 0.080538
FEATURE [App::DocumentObjectGroupPython] C_element125  label="C_element : 0.600"  # scripted group (container) (typed FeaturePython)
  n = 0.599848
FEATURE [App::DocumentObjectGroupPython] O_element108  label="O_element : 0.320"  # scripted group (container) (typed FeaturePython)
  n = 0.319614
FEATURE [App::DocumentObjectGroupPython] G4_LUCITE  # scripted group (container) (typed FeaturePython)
  Dunit = g/cm3
  Dvalue = 1.19
  Group = -> [H_element115,C_element125,O_element108]
  conduct = 2
  density = 1
  expand = 3
  formula = G4_LUCITE
  name = G4_LUCITE
  specific = 4
FEATURE [App::DocumentObjectGroupPython] Cu_element002  label="Cu_element : 62"  # scripted group (container) (typed FeaturePython)
  n = 62
  ref = Cu_element
FEATURE [App::DocumentObjectGroupPython] Zn_element002  label="Zn_element : 35"  # scripted group (container) (typed FeaturePython)
  n = 35
  ref = Zn_element
FEATURE [App::DocumentObjectGroupPython] Pb_element005  label="Pb_element : 3"  # scripted group (container) (typed FeaturePython)
  n = 3
  ref = Pb_element
FEATURE [App::DocumentObjectGroupPython] G4_BRASS  # scripted group (container) (typed FeaturePython)
  Dunit = g/cm3
  Dvalue = 8.52
  Group = -> [Cu_element002,Zn_element002,Pb_element005]
  conduct = 2
  density = 1
  expand = 3
  formula = G4_BRASS
  name = G4_BRASS
  specific = 4
FEATURE [App::DocumentObjectGroupPython] Cu_element003  label="Cu_element : 89"  # scripted group (container) (typed FeaturePython)
  n = 89
  ref = Cu_element
FEATURE [App::DocumentObjectGroupPython] Zn_element003  label="Zn_element : 9"  # scripted group (container) (typed FeaturePython)
  n = 9
  ref = Zn_element
FEATURE [App::DocumentObjectGroupPython] Pb_element006  label="Pb_element : 2"  # scripted group (container) (typed FeaturePython)
  n = 2
  ref = Pb_element
FEATURE [App::DocumentObjectGroupPython] G4_BRONZE  # scripted group (container) (typed FeaturePython)
  Dunit = g/cm3
  Dvalue = 8.82
  Group = -> [Cu_element003,Zn_element003,Pb_element006]
  conduct = 2
  density = 1
  expand = 3
  formula = G4_BRONZE
  name = G4_BRONZE
  specific = 4
FEATURE [App::DocumentObjectGroupPython] Fe_element008  label="Fe_element : 74"  # scripted group (container) (typed FeaturePython)
  n = 74
  ref = Fe_element
FEATURE [App::DocumentObjectGroupPython] Cr_element002  label="Cr_element : 18"  # scripted group (container) (typed FeaturePython)
  n = 18
  ref = Cr_element
FEATURE [App::DocumentObjectGroupPython] Ni_element002  label="Ni_element : 8"  # scripted group (container) (typed FeaturePython)
  n = 8
  ref = Ni_element
FEATURE [App::DocumentObjectGroupPython] G4_STAINLESS_STEEL  label="G4_STAINLESS-STEEL"  # scripted group (container) (typed FeaturePython)
  Dunit = g/cm3
  Dvalue = 8
  Group = -> [Fe_element008,Cr_element002,Ni_element002]
  conduct = 2
  density = 1
  expand = 3
  formula = G4_STAINLESS-STEEL
  name = G4_STAINLESS-STEEL
  specific = 4
FEATURE [App::DocumentObjectGroupPython] H_element116  label="H_element : 064"  # scripted group (container) (typed FeaturePython)
  n = 18
  ref = H_element
FEATURE [App::DocumentObjectGroupPython] C_element126  label="C_element : 071"  # scripted group (container) (typed FeaturePython)
  n = 12
  ref = C_element
FEATURE [App::DocumentObjectGroupPython] O_element109  label="O_element : 062"  # scripted group (container) (typed FeaturePython)
  n = 7
  ref = O_element
FEATURE [App::DocumentObjectGroupPython] G4_CR39  # scripted group (container) (typed FeaturePython)
  Dunit = g/cm3
  Dvalue = 1.32
  Group = -> [H_element116,C_element126,O_element109]
  conduct = 2
  density = 1
  expand = 3
  formula = G4_CR39
  name = G4_CR39
  specific = 4
FEATURE [App::DocumentObjectGroupPython] H_element117  label="H_element : 38"  # scripted group (container) (typed FeaturePython)
  n = 38
  ref = H_element
FEATURE [App::DocumentObjectGroupPython] C_element127  label="C_element : 072"  # scripted group (container) (typed FeaturePython)
  n = 18
  ref = C_element
FEATURE [App::DocumentObjectGroupPython] O_element110  label="O_element : 063"  # scripted group (container) (typed FeaturePython)
  n = 1
  ref = O_element
FEATURE [App::DocumentObjectGroupPython] G4_OCTADECANOL  # scripted group (container) (typed FeaturePython)
  Dunit = g/cm3
  Dvalue = 0.812
  Group = -> [H_element117,C_element127,O_element110]
  conduct = 2
  density = 1
  expand = 3
  formula = G4_OCTADECANOL
  name = G4_OCTADECANOL
  specific = 4
FEATURE [App::DocumentObjectGroupPython] HEP  # scripted group (container) (typed FeaturePython)
  Group = -> [G4_lH2,G4_lN2,G4_lO2,G4_lAr,G4_lBr,G4_lKr,G4_lXe,G4_PbWO4,G4_Galactic,G4_GRAPHITE_POROUS,G4_LUCITE,G4_BRASS,G4_BRONZE,G4_STAINLESS_STEEL,G4_CR39,G4_OCTADECANOL]
FEATURE [App::DocumentObjectGroupPython] C_element128  label="C_element : 073"  # scripted group (container) (typed FeaturePython)
  n = 14
  ref = C_element
FEATURE [App::DocumentObjectGroupPython] H_element118  label="H_element : 065"  # scripted group (container) (typed FeaturePython)
  n = 10
  ref = H_element
FEATURE [App::DocumentObjectGroupPython] O_element111  label="O_element : 064"  # scripted group (container) (typed FeaturePython)
  n = 2
  ref = O_element
FEATURE [App::DocumentObjectGroupPython] N_element050  label="N_element : 023"  # scripted group (container) (typed FeaturePython)
  n = 2
  ref = N_element
FEATURE [App::DocumentObjectGroupPython] G4_KEVLAR  # scripted group (container) (typed FeaturePython)
  Dunit = g/cm3
  Dvalue = 1.44
  Group = -> [C_element128,H_element118,O_element111,N_element050]
  conduct = 2
  density = 1
  expand = 3
  formula = G4_KEVLAR
  name = G4_KEVLAR
  specific = 4
FEATURE [App::DocumentObjectGroupPython] C_element129  label="C_element : 074"  # scripted group (container) (typed FeaturePython)
  n = 10
  ref = C_element
FEATURE [App::DocumentObjectGroupPython] H_element119  label="H_element : 066"  # scripted group (container) (typed FeaturePython)
  n = 8
  ref = H_element
FEATURE [App::DocumentObjectGroupPython] O_element112  label="O_element : 065"  # scripted group (container) (typed FeaturePython)
  n = 4
  ref = O_element
FEATURE [App::DocumentObjectGroupPython] G4_DACRON  # scripted group (container) (typed FeaturePython)
  Dunit = g/cm3
  Dvalue = 1.4
  Group = -> [C_element129,H_element119,O_element112]
  conduct = 2
  density = 1
  expand = 3
  formula = G4_DACRON
  name = G4_DACRON
  specific = 4
FEATURE [App::DocumentObjectGroupPython] C_element130  label="C_element : 075"  # scripted group (container) (typed FeaturePython)
  n = 4
  ref = C_element
FEATURE [App::DocumentObjectGroupPython] H_element120  label="H_element : 067"  # scripted group (container) (typed FeaturePython)
  n = 5
  ref = H_element
FEATURE [App::DocumentObjectGroupPython] Cl_element030  label="Cl_element : 016"  # scripted group (container) (typed FeaturePython)
  n = 1
  ref = Cl_element
FEATURE [App::DocumentObjectGroupPython] G4_NEOPRENE  # scripted group (container) (typed FeaturePython)
  Dunit = g/cm3
  Dvalue = 1.23
  Group = -> [C_element130,H_element120,Cl_element030]
  conduct = 2
  density = 1
  expand = 3
  formula = G4_NEOPRENE
  name = G4_NEOPRENE
  specific = 4
FEATURE [App::DocumentObjectGroupPython] Space  # scripted group (container) (typed FeaturePython)
  Group = -> [G4_KEVLAR,G4_DACRON,G4_NEOPRENE]
FEATURE [App::DocumentObjectGroupPython] H_element121  label="H_element : 068"  # scripted group (container) (typed FeaturePython)
  n = 5
  ref = H_element
FEATURE [App::DocumentObjectGroupPython] C_element131  label="C_element : 076"  # scripted group (container) (typed FeaturePython)
  n = 4
  ref = C_element
FEATURE [App::DocumentObjectGroupPython] N_element051  label="N_element : 3"  # scripted group (container) (typed FeaturePython)
  n = 3
  ref = N_element
FEATURE [App::DocumentObjectGroupPython] O_element113  label="O_element : 066"  # scripted group (container) (typed FeaturePython)
  n = 1
  ref = O_element
FEATURE [App::DocumentObjectGroupPython] G4_CYTOSINE  # scripted group (container) (typed FeaturePython)
  Dunit = g/cm3
  Dvalue = 1.55
  Group = -> [H_element121,C_element131,N_element051,O_element113]
  conduct = 2
  density = 1
  expand = 3
  formula = G4_CYTOSINE
  name = G4_CYTOSINE
  specific = 4
FEATURE [App::DocumentObjectGroupPython] H_element122  label="H_element : 069"  # scripted group (container) (typed FeaturePython)
  n = 6
  ref = H_element
FEATURE [App::DocumentObjectGroupPython] C_element132  label="C_element : 077"  # scripted group (container) (typed FeaturePython)
  n = 5
  ref = C_element
FEATURE [App::DocumentObjectGroupPython] N_element052  label="N_element : 024"  # scripted group (container) (typed FeaturePython)
  n = 2
  ref = N_element
FEATURE [App::DocumentObjectGroupPython] O_element114  label="O_element : 067"  # scripted group (container) (typed FeaturePython)
  n = 2
  ref = O_element
FEATURE [App::DocumentObjectGroupPython] G4_THYMINE  # scripted group (container) (typed FeaturePython)
  Dunit = g/cm3
  Dvalue = 1.23
  Group = -> [H_element122,C_element132,N_element052,O_element114]
  conduct = 2
  density = 1
  expand = 3
  formula = G4_THYMINE
  name = G4_THYMINE
  specific = 4
FEATURE [App::DocumentObjectGroupPython] H_element123  label="H_element : 070"  # scripted group (container) (typed FeaturePython)
  n = 4
  ref = H_element
FEATURE [App::DocumentObjectGroupPython] C_element133  label="C_element : 078"  # scripted group (container) (typed FeaturePython)
  n = 4
  ref = C_element
FEATURE [App::DocumentObjectGroupPython] N_element053  label="N_element : 025"  # scripted group (container) (typed FeaturePython)
  n = 2
  ref = N_element
FEATURE [App::DocumentObjectGroupPython] O_element115  label="O_element : 068"  # scripted group (container) (typed FeaturePython)
  n = 2
  ref = O_element
FEATURE [App::DocumentObjectGroupPython] G4_URACIL  # scripted group (container) (typed FeaturePython)
  Dunit = g/cm3
  Dvalue = 1.32
  Group = -> [H_element123,C_element133,N_element053,O_element115]
  conduct = 2
  density = 1
  expand = 3
  formula = G4_URACIL
  name = G4_URACIL
  specific = 4
FEATURE [App::DocumentObjectGroupPython] H_element124  label="H_element : 071"  # scripted group (container) (typed FeaturePython)
  n = 4
  ref = H_element
FEATURE [App::DocumentObjectGroupPython] C_element134  label="C_element : 079"  # scripted group (container) (typed FeaturePython)
  n = 5
  ref = C_element
FEATURE [App::DocumentObjectGroupPython] N_element054  label="N_element : 026"  # scripted group (container) (typed FeaturePython)
  n = 5
  ref = N_element
FEATURE [App::DocumentObjectGroupPython] G4_DNA_ADENINE  # scripted group (container) (typed FeaturePython)
  Dunit = g/cm3
  Dvalue = 1
  Group = -> [H_element124,C_element134,N_element054]
  conduct = 2
  density = 1
  expand = 3
  formula = G4_DNA_ADENINE
  name = G4_DNA_ADENINE
  specific = 4
FEATURE [App::DocumentObjectGroupPython] H_element125  label="H_element : 072"  # scripted group (container) (typed FeaturePython)
  n = 4
  ref = H_element
FEATURE [App::DocumentObjectGroupPython] C_element135  label="C_element : 080"  # scripted group (container) (typed FeaturePython)
  n = 5
  ref = C_element
FEATURE [App::DocumentObjectGroupPython] N_element055  label="N_element : 027"  # scripted group (container) (typed FeaturePython)
  n = 5
  ref = N_element
FEATURE [App::DocumentObjectGroupPython] O_element116  label="O_element : 069"  # scripted group (container) (typed FeaturePython)
  n = 1
  ref = O_element
FEATURE [App::DocumentObjectGroupPython] G4_DNA_GUANINE  # scripted group (container) (typed FeaturePython)
  Dunit = g/cm3
  Dvalue = 1
  Group = -> [H_element125,C_element135,N_element055,O_element116]
  conduct = 2
  density = 1
  expand = 3
  formula = G4_DNA_GUANINE
  name = G4_DNA_GUANINE
  specific = 4
FEATURE [App::DocumentObjectGroupPython] H_element126  label="H_element : 073"  # scripted group (container) (typed FeaturePython)
  n = 4
  ref = H_element
FEATURE [App::DocumentObjectGroupPython] C_element136  label="C_element : 081"  # scripted group (container) (typed FeaturePython)
  n = 4
  ref = C_element
FEATURE [App::DocumentObjectGroupPython] N_element056  label="N_element : 028"  # scripted group (container) (typed FeaturePython)
  n = 3
  ref = N_element
FEATURE [App::DocumentObjectGroupPython] O_element117  label="O_element : 070"  # scripted group (container) (typed FeaturePython)
  n = 1
  ref = O_element
FEATURE [App::DocumentObjectGroupPython] G4_DNA_CYTOSINE  # scripted group (container) (typed FeaturePython)
  Dunit = g/cm3
  Dvalue = 1
  Group = -> [H_element126,C_element136,N_element056,O_element117]
  conduct = 2
  density = 1
  expand = 3
  formula = G4_DNA_CYTOSINE
  name = G4_DNA_CYTOSINE
  specific = 4
FEATURE [App::DocumentObjectGroupPython] H_element127  label="H_element : 074"  # scripted group (container) (typed FeaturePython)
  n = 5
  ref = H_element
FEATURE [App::DocumentObjectGroupPython] C_element137  label="C_element : 082"  # scripted group (container) (typed FeaturePython)
  n = 5
  ref = C_element
FEATURE [App::DocumentObjectGroupPython] N_element057  label="N_element : 029"  # scripted group (container) (typed FeaturePython)
  n = 2
  ref = N_element
FEATURE [App::DocumentObjectGroupPython] O_element118  label="O_element : 071"  # scripted group (container) (typed FeaturePython)
  n = 2
  ref = O_element
FEATURE [App::DocumentObjectGroupPython] G4_DNA_THYMINE  # scripted group (container) (typed FeaturePython)
  Dunit = g/cm3
  Dvalue = 1
  Group = -> [H_element127,C_element137,N_element057,O_element118]
  conduct = 2
  density = 1
  expand = 3
  formula = G4_DNA_THYMINE
  name = G4_DNA_THYMINE
  specific = 4
FEATURE [App::DocumentObjectGroupPython] H_element128  label="H_element : 075"  # scripted group (container) (typed FeaturePython)
  n = 3
  ref = H_element
FEATURE [App::DocumentObjectGroupPython] C_element138  label="C_element : 083"  # scripted group (container) (typed FeaturePython)
  n = 4
  ref = C_element
FEATURE [App::DocumentObjectGroupPython] N_element058  label="N_element : 030"  # scripted group (container) (typed FeaturePython)
  n = 2
  ref = N_element
FEATURE [App::DocumentObjectGroupPython] O_element119  label="O_element : 072"  # scripted group (container) (typed FeaturePython)
  n = 2
  ref = O_element
FEATURE [App::DocumentObjectGroupPython] G4_DNA_URACIL  # scripted group (container) (typed FeaturePython)
  Dunit = g/cm3
  Dvalue = 1
  Group = -> [H_element128,C_element138,N_element058,O_element119]
  conduct = 2
  density = 1
  expand = 3
  formula = G4_DNA_URACIL
  name = G4_DNA_URACIL
  specific = 4
FEATURE [App::DocumentObjectGroupPython] H_element129  label="H_element : 076"  # scripted group (container) (typed FeaturePython)
  n = 10
  ref = H_element
FEATURE [App::DocumentObjectGroupPython] C_element139  label="C_element : 084"  # scripted group (container) (typed FeaturePython)
  n = 10
  ref = C_element
FEATURE [App::DocumentObjectGroupPython] N_element059  label="N_element : 031"  # scripted group (container) (typed FeaturePython)
  n = 5
  ref = N_element
FEATURE [App::DocumentObjectGroupPython] O_element120  label="O_element : 073"  # scripted group (container) (typed FeaturePython)
  n = 4
  ref = O_element
FEATURE [App::DocumentObjectGroupPython] G4_DNA_ADENOSINE  # scripted group (container) (typed FeaturePython)
  Dunit = g/cm3
  Dvalue = 1
  Group = -> [H_element129,C_element139,N_element059,O_element120]
  conduct = 2
  density = 1
  expand = 3
  formula = G4_DNA_ADENOSINE
  name = G4_DNA_ADENOSINE
  specific = 4
FEATURE [App::DocumentObjectGroupPython] H_element130  label="H_element : 077"  # scripted group (container) (typed FeaturePython)
  n = 10
  ref = H_element
FEATURE [App::DocumentObjectGroupPython] C_element140  label="C_element : 085"  # scripted group (container) (typed FeaturePython)
  n = 10
  ref = C_element
FEATURE [App::DocumentObjectGroupPython] N_element060  label="N_element : 032"  # scripted group (container) (typed FeaturePython)
  n = 5
  ref = N_element
FEATURE [App::DocumentObjectGroupPython] O_element121  label="O_element : 074"  # scripted group (container) (typed FeaturePython)
  n = 5
  ref = O_element
FEATURE [App::DocumentObjectGroupPython] G4_DNA_GUANOSINE  # scripted group (container) (typed FeaturePython)
  Dunit = g/cm3
  Dvalue = 1
  Group = -> [H_element130,C_element140,N_element060,O_element121]
  conduct = 2
  density = 1
  expand = 3
  formula = G4_DNA_GUANOSINE
  name = G4_DNA_GUANOSINE
  specific = 4
FEATURE [App::DocumentObjectGroupPython] H_element131  label="H_element : 078"  # scripted group (container) (typed FeaturePython)
  n = 10
  ref = H_element
FEATURE [App::DocumentObjectGroupPython] C_element141  label="C_element : 086"  # scripted group (container) (typed FeaturePython)
  n = 9
  ref = C_element
FEATURE [App::DocumentObjectGroupPython] N_element061  label="N_element : 033"  # scripted group (container) (typed FeaturePython)
  n = 3
  ref = N_element
FEATURE [App::DocumentObjectGroupPython] O_element122  label="O_element : 075"  # scripted group (container) (typed FeaturePython)
  n = 5
  ref = O_element
FEATURE [App::DocumentObjectGroupPython] G4_DNA_CYTIDINE  # scripted group (container) (typed FeaturePython)
  Dunit = g/cm3
  Dvalue = 1
  Group = -> [H_element131,C_element141,N_element061,O_element122]
  conduct = 2
  density = 1
  expand = 3
  formula = G4_DNA_CYTIDINE
  name = G4_DNA_CYTIDINE
  specific = 4
FEATURE [App::DocumentObjectGroupPython] H_element132  label="H_element : 079"  # scripted group (container) (typed FeaturePython)
  n = 9
  ref = H_element
FEATURE [App::DocumentObjectGroupPython] C_element142  label="C_element : 087"  # scripted group (container) (typed FeaturePython)
  n = 9
  ref = C_element
FEATURE [App::DocumentObjectGroupPython] N_element062  label="N_element : 034"  # scripted group (container) (typed FeaturePython)
  n = 2
  ref = N_element
FEATURE [App::DocumentObjectGroupPython] O_element123  label="O_element : 076"  # scripted group (container) (typed FeaturePython)
  n = 6
  ref = O_element
FEATURE [App::DocumentObjectGroupPython] G4_DNA_URIDINE  # scripted group (container) (typed FeaturePython)
  Dunit = g/cm3
  Dvalue = 1
  Group = -> [H_element132,C_element142,N_element062,O_element123]
  conduct = 2
  density = 1
  expand = 3
  formula = G4_DNA_URIDINE
  name = G4_DNA_URIDINE
  specific = 4
FEATURE [App::DocumentObjectGroupPython] H_element133  label="H_element : 080"  # scripted group (container) (typed FeaturePython)
  n = 11
  ref = H_element
FEATURE [App::DocumentObjectGroupPython] C_element143  label="C_element : 088"  # scripted group (container) (typed FeaturePython)
  n = 10
  ref = C_element
FEATURE [App::DocumentObjectGroupPython] N_element063  label="N_element : 035"  # scripted group (container) (typed FeaturePython)
  n = 2
  ref = N_element
FEATURE [App::DocumentObjectGroupPython] O_element124  label="O_element : 077"  # scripted group (container) (typed FeaturePython)
  n = 6
  ref = O_element
FEATURE [App::DocumentObjectGroupPython] G4_DNA_METHYLURIDINE  # scripted group (container) (typed FeaturePython)
  Dunit = g/cm3
  Dvalue = 1
  Group = -> [H_element133,C_element143,N_element063,O_element124]
  conduct = 2
  density = 1
  expand = 3
  formula = G4_DNA_METHYLURIDINE
  name = G4_DNA_METHYLURIDINE
  specific = 4
FEATURE [App::DocumentObjectGroupPython] P_element014  label="P_element : 003"  # scripted group (container) (typed FeaturePython)
  n = 1
  ref = P_element
FEATURE [App::DocumentObjectGroupPython] O_element125  label="O_element : 078"  # scripted group (container) (typed FeaturePython)
  n = 3
  ref = O_element
FEATURE [App::DocumentObjectGroupPython] G4_DNA_MONOPHOSPHATE  # scripted group (container) (typed FeaturePython)
  Dunit = g/cm3
  Dvalue = 1
  Group = -> [P_element014,O_element125]
  conduct = 2
  density = 1
  expand = 3
  formula = G4_DNA_MONOPHOSPHATE
  name = G4_DNA_MONOPHOSPHATE
  specific = 4
FEATURE [App::DocumentObjectGroupPython] H_element134  label="H_element : 081"  # scripted group (container) (typed FeaturePython)
  n = 10
  ref = H_element
FEATURE [App::DocumentObjectGroupPython] C_element144  label="C_element : 089"  # scripted group (container) (typed FeaturePython)
  n = 10
  ref = C_element
FEATURE [App::DocumentObjectGroupPython] N_element064  label="N_element : 036"  # scripted group (container) (typed FeaturePython)
  n = 5
  ref = N_element
FEATURE [App::DocumentObjectGroupPython] O_element126  label="O_element : 079"  # scripted group (container) (typed FeaturePython)
  n = 7
  ref = O_element
FEATURE [App::DocumentObjectGroupPython] P_element015  label="P_element : 004"  # scripted group (container) (typed FeaturePython)
  n = 1
  ref = P_element
FEATURE [App::DocumentObjectGroupPython] G4_DNA_A  # scripted group (container) (typed FeaturePython)
  Dunit = g/cm3
  Dvalue = 1
  Group = -> [H_element134,C_element144,N_element064,O_element126,P_element015]
  conduct = 2
  density = 1
  expand = 3
  formula = G4_DNA_A
  name = G4_DNA_A
  specific = 4
FEATURE [App::DocumentObjectGroupPython] H_element135  label="H_element : 082"  # scripted group (container) (typed FeaturePython)
  n = 10
  ref = H_element
FEATURE [App::DocumentObjectGroupPython] C_element145  label="C_element : 090"  # scripted group (container) (typed FeaturePython)
  n = 10
  ref = C_element
FEATURE [App::DocumentObjectGroupPython] N_element065  label="N_element : 037"  # scripted group (container) (typed FeaturePython)
  n = 5
  ref = N_element
FEATURE [App::DocumentObjectGroupPython] O_element127  label="O_element : 8"  # scripted group (container) (typed FeaturePython)
  n = 8
  ref = O_element
FEATURE [App::DocumentObjectGroupPython] P_element016  label="P_element : 005"  # scripted group (container) (typed FeaturePython)
  n = 1
  ref = P_element
FEATURE [App::DocumentObjectGroupPython] G4_DNA_G  # scripted group (container) (typed FeaturePython)
  Dunit = g/cm3
  Dvalue = 1
  Group = -> [H_element135,C_element145,N_element065,O_element127,P_element016]
  conduct = 2
  density = 1
  expand = 3
  formula = G4_DNA_G
  name = G4_DNA_G
  specific = 4
FEATURE [App::DocumentObjectGroupPython] H_element136  label="H_element : 083"  # scripted group (container) (typed FeaturePython)
  n = 10
  ref = H_element
FEATURE [App::DocumentObjectGroupPython] C_element146  label="C_element : 091"  # scripted group (container) (typed FeaturePython)
  n = 9
  ref = C_element
FEATURE [App::DocumentObjectGroupPython] N_element066  label="N_element : 038"  # scripted group (container) (typed FeaturePython)
  n = 3
  ref = N_element
FEATURE [App::DocumentObjectGroupPython] O_element128  label="O_element : 080"  # scripted group (container) (typed FeaturePython)
  n = 8
  ref = O_element
FEATURE [App::DocumentObjectGroupPython] P_element017  label="P_element : 006"  # scripted group (container) (typed FeaturePython)
  n = 1
  ref = P_element
FEATURE [App::DocumentObjectGroupPython] G4_DNA_C  # scripted group (container) (typed FeaturePython)
  Dunit = g/cm3
  Dvalue = 1
  Group = -> [H_element136,C_element146,N_element066,O_element128,P_element017]
  conduct = 2
  density = 1
  expand = 3
  formula = G4_DNA_C
  name = G4_DNA_C
  specific = 4
FEATURE [App::DocumentObjectGroupPython] H_element137  label="H_element : 084"  # scripted group (container) (typed FeaturePython)
  n = 9
  ref = H_element
FEATURE [App::DocumentObjectGroupPython] C_element147  label="C_element : 092"  # scripted group (container) (typed FeaturePython)
  n = 9
  ref = C_element
FEATURE [App::DocumentObjectGroupPython] N_element067  label="N_element : 039"  # scripted group (container) (typed FeaturePython)
  n = 2
  ref = N_element
FEATURE [App::DocumentObjectGroupPython] O_element129  label="O_element : 9"  # scripted group (container) (typed FeaturePython)
  n = 9
  ref = O_element
FEATURE [App::DocumentObjectGroupPython] P_element018  label="P_element : 007"  # scripted group (container) (typed FeaturePython)
  n = 1
  ref = P_element
FEATURE [App::DocumentObjectGroupPython] G4_DNA_U  # scripted group (container) (typed FeaturePython)
  Dunit = g/cm3
  Dvalue = 1
  Group = -> [H_element137,C_element147,N_element067,O_element129,P_element018]
  conduct = 2
  density = 1
  expand = 3
  formula = G4_DNA_U
  name = G4_DNA_U
  specific = 4
FEATURE [App::DocumentObjectGroupPython] H_element138  label="H_element : 085"  # scripted group (container) (typed FeaturePython)
  n = 11
  ref = H_element
FEATURE [App::DocumentObjectGroupPython] C_element148  label="C_element : 093"  # scripted group (container) (typed FeaturePython)
  n = 10
  ref = C_element
FEATURE [App::DocumentObjectGroupPython] N_element068  label="N_element : 040"  # scripted group (container) (typed FeaturePython)
  n = 2
  ref = N_element
FEATURE [App::DocumentObjectGroupPython] O_element130  label="O_element : 081"  # scripted group (container) (typed FeaturePython)
  n = 9
  ref = O_element
FEATURE [App::DocumentObjectGroupPython] P_element019  label="P_element : 008"  # scripted group (container) (typed FeaturePython)
  n = 1
  ref = P_element
FEATURE [App::DocumentObjectGroupPython] G4_DNA_MU  # scripted group (container) (typed FeaturePython)
  Dunit = g/cm3
  Dvalue = 1
  Group = -> [H_element138,C_element148,N_element068,O_element130,P_element019]
  conduct = 2
  density = 1
  expand = 3
  formula = G4_DNA_MU
  name = G4_DNA_MU
  specific = 4
FEATURE [App::DocumentObjectGroupPython] BioChemical  # scripted group (container) (typed FeaturePython)
  Group = -> [G4_CYTOSINE,G4_THYMINE,G4_URACIL,G4_DNA_ADENINE,G4_DNA_GUANINE,G4_DNA_CYTOSINE,G4_DNA_THYMINE,G4_DNA_URACIL,G4_DNA_ADENOSINE,G4_DNA_GUANOSINE,G4_DNA_CYTIDINE,G4_DNA_URIDINE,G4_DNA_METHYLURIDINE,G4_DNA_MONOPHOSPHATE,G4_DNA_A,G4_DNA_G,G4_DNA_C,G4_DNA_U,G4_DNA_MU]
FEATURE [App::DocumentObjectGroupPython] G4Materials  # scripted group (container) (typed FeaturePython)
  Group = -> [NIST,Element,HEP,Space,BioChemical]
  version = 1
FEATURE [App::DocumentObjectGroupPython] Geant4  # scripted group (container) (typed FeaturePython)
  Group = -> [G4Isotopes,G4Elements,G4Materials]
FEATURE [Part::FeaturePython] GDMLBox_WorldBox  # WARN: FeaturePython — macro-defined, semantics opaque (R4)
  lunit = 2
  material = 8
  x = 114.01
  y = 147.706
  z = 147.706
FEATURE [App::DocumentObjectGroupPython] G4_Pyrex_Glass001  label="G4_Pyrex_Glass : 1.000"  # scripted group (container) (typed FeaturePython)
  n = 1
FEATURE [App::DocumentObjectGroupPython] Glass  # scripted group (container) (typed FeaturePython)
  Dunit = g/cm3
  Dvalue = 1.032
  Group = -> [G4_Pyrex_Glass001]
  RINDEX = RINDEXLAR
  conduct = 2
  density = 1
  expand = 3
  name = Glass
  specific = 4
FEATURE [App::DocumentObjectGroupPython] G4_CESIUM_IODIDE  label="G4_CESIUM_IODIDE : 1.000"  # scripted group (container) (typed FeaturePython)
  n = 1
FEATURE [App::DocumentObjectGroupPython] LYSO  # scripted group (container) (typed FeaturePython)
  ABSLENGTH = ABSLENGTHLAR
  Dunit = g/cm3
  Dvalue = 7.1
  FASTCOMPONENT = SCINTLAR
  FASTTIMECONSTANT = FTC
  Group = -> [G4_CESIUM_IODIDE]
  RAYLEIGH = RAYLEIGHLAR
  REEMISSIONPROB = SCINTLAR
  RESOLUTIONSCALE = RS
  RINDEX = RINDEXLAR
  SCINTILLATIONYIELD = SY
  SLOWCOMPONENT = SCINTLAR
  SLOWTIMECONSTANT = STC
  YIELDRATIO = YR
  conduct = 2
  density = 1
  expand = 3
  name = LYSO
  specific = 4
FEATURE [App::DocumentObjectGroupPython] Materials  # scripted group (container) (typed FeaturePython)
  Group = -> [Air,Geant4,Glass,LYSO]
FEATURE [Part::FeaturePython] GDMLSphere_Sphere  # WARN: FeaturePython — macro-defined, semantics opaque (R4)
  aunit = 1
  deltaphi = 360
  deltatheta = 180
  lunit = 2
  material = 164
  rmax = 5
  rmin = 0
  startphi = 0
  starttheta = 0
FEATURE [App::Part] LV_Sphere
  Group = -> [GDMLSphere_Sphere]
  Origin = -> Origin004
FEATURE [Part::FeaturePython] GDMLBox_Box004  # WARN: FeaturePython — macro-defined, semantics opaque (R4)
  CopyNumber = 1
  Placement = pos=(0,0,37.85) rot=(0,0,1;0rad)
  lunit = 2
  material = 1
  x = 27.8
  y = 27.8
  z = 8
FEATURE [App::Link] Link_GDMLBox_Box004
  CopyNumber = 2
  LinkPlacement = pos=(26.764,0,26.764) rot=(0,1,0;0.785398rad)
  LinkedObject = -> GDMLBox_Box004
  Placement = pos=(26.764,0,26.764) rot=(0,1,0;0.785398rad)
FEATURE [App::Link] Link_GDMLBox_Box004001
  CopyNumber = 3
  LinkPlacement = pos=(37.85,0,7.1e-15) rot=(0,1,0;1.5708rad)
  LinkedObject = -> GDMLBox_Box004
  Placement = pos=(37.85,0,7.1e-15) rot=(0,1,0;1.5708rad)
FEATURE [App::Link] Link_GDMLBox_Box004002
  CopyNumber = 4
  LinkPlacement = pos=(26.764,0,-26.764) rot=(0,1,0;2.35619rad)
  LinkedObject = -> GDMLBox_Box004
  Placement = pos=(26.764,0,-26.764) rot=(0,1,0;2.35619rad)
FEATURE [App::Link] Link_GDMLBox_Box004003
  CopyNumber = 5
  LinkPlacement = pos=(4.6e-15,0,-37.85) rot=(0,1,0;3.14159rad)
  LinkedObject = -> GDMLBox_Box004
  Placement = pos=(4.6e-15,0,-37.85) rot=(0,1,0;3.14159rad)
FEATURE [App::Link] Link_GDMLBox_Box004004
  CopyNumber = 6
  LinkPlacement = pos=(-26.764,0,-26.764) rot=(0,1,0;3.92699rad)
  LinkedObject = -> GDMLBox_Box004
  Placement = pos=(-26.764,0,-26.764) rot=(0,1,0;3.92699rad)
FEATURE [App::Link] Link_GDMLBox_Box004005
  CopyNumber = 7
  LinkPlacement = pos=(-37.85,0,-7.1e-15) rot=(0,1,0;4.71239rad)
  LinkedObject = -> GDMLBox_Box004
  Placement = pos=(-37.85,0,-7.1e-15) rot=(0,1,0;4.71239rad)
FEATURE [App::Link] Link_GDMLBox_Box004006
  CopyNumber = 8
  LinkPlacement = pos=(-26.764,0,26.764) rot=(0,1,0;5.49779rad)
  LinkedObject = -> GDMLBox_Box004
  Placement = pos=(-26.764,0,26.764) rot=(0,1,0;5.49779rad)
FEATURE [App::Part] Array002001
  Group = -> [GDMLBox_Box004,Link_GDMLBox_Box004,Link_GDMLBox_Box004001,Link_GDMLBox_Box004002,Link_GDMLBox_Box004003,Link_GDMLBox_Box004004,Link_GDMLBox_Box004005,Link_GDMLBox_Box004006]
  Origin = -> Origin005
FEATURE [App::Part] Part001
  Group = -> [Array002001]
  Origin = -> Origin002
  SkinSurface = 0
FEATURE [App::Link] Link_Child_Array
  CopyNumber = 10
  LinkPlacement = pos=(26.764,0,26.764) rot=(0,1,0;0.785398rad)
  LinkedObject = -> Child_Array
  Placement = pos=(26.764,0,26.764) rot=(0,1,0;0.785398rad)
FEATURE [App::Link] Link_Child_Array001
  CopyNumber = 11
  LinkPlacement = pos=(37.85,0,7.1e-15) rot=(0,1,0;1.5708rad)
  LinkedObject = -> Child_Array
  Placement = pos=(37.85,0,7.1e-15) rot=(0,1,0;1.5708rad)
FEATURE [App::Link] Link_Child_Array002
  CopyNumber = 12
  LinkPlacement = pos=(26.764,0,-26.764) rot=(0,1,0;2.35619rad)
  LinkedObject = -> Child_Array
  Placement = pos=(26.764,0,-26.764) rot=(0,1,0;2.35619rad)
FEATURE [App::Link] Link_Child_Array003
  CopyNumber = 13
  LinkPlacement = pos=(4.6e-15,0,-37.85) rot=(0,1,0;3.14159rad)
  LinkedObject = -> Child_Array
  Placement = pos=(4.6e-15,0,-37.85) rot=(0,1,0;3.14159rad)
FEATURE [App::Link] Link_Child_Array004
  CopyNumber = 14
  LinkPlacement = pos=(-26.764,0,-26.764) rot=(0,1,0;3.92699rad)
  LinkedObject = -> Child_Array
  Placement = pos=(-26.764,0,-26.764) rot=(0,1,0;3.92699rad)
FEATURE [App::Link] Link_Child_Array005
  CopyNumber = 15
  LinkPlacement = pos=(-37.85,0,-7.1e-15) rot=(0,1,0;4.71239rad)
  LinkedObject = -> Child_Array
  Placement = pos=(-37.85,0,-7.1e-15) rot=(0,1,0;4.71239rad)
FEATURE [App::Link] Link_Child_Array006
  CopyNumber = 16
  LinkPlacement = pos=(-26.764,0,26.764) rot=(0,1,0;5.49779rad)
  LinkedObject = -> Child_Array
  Placement = pos=(-26.764,0,26.764) rot=(0,1,0;5.49779rad)
FEATURE [Part::FeaturePython] GDMLBox_Box005  # WARN: FeaturePython — macro-defined, semantics opaque (R4)
  CopyNumber = 17
  Placement = pos=(-11.99,-11.99,5) rot=(0,0,1;0rad)
  lunit = 2
  material = 0
  x = 3.22
  y = 3.22
  z = 2
FEATURE [App::Link] Link_GDMLBox_Box005
  CopyNumber = 18
  LinkPlacement = pos=(-11.99,-8.59,5) rot=(0,0,1;0rad)
  LinkedObject = -> GDMLBox_Box005
  Placement = pos=(-11.99,-8.59,5) rot=(0,0,1;0rad)
FEATURE [App::Link] Link_GDMLBox_Box005001
  CopyNumber = 19
  LinkPlacement = pos=(-11.99,-5.19,5) rot=(0,0,1;0rad)
  LinkedObject = -> GDMLBox_Box005
  Placement = pos=(-11.99,-5.19,5) rot=(0,0,1;0rad)
FEATURE [App::Link] Link_GDMLBox_Box005002
  CopyNumber = 20
  LinkPlacement = pos=(-11.99,-1.79,5) rot=(0,0,1;0rad)
  LinkedObject = -> GDMLBox_Box005
  Placement = pos=(-11.99,-1.79,5) rot=(0,0,1;0rad)
FEATURE [App::Link] Link_GDMLBox_Box005003
  CopyNumber = 21
  LinkPlacement = pos=(-11.99,1.61,5) rot=(0,0,1;0rad)
  LinkedObject = -> GDMLBox_Box005
  Placement = pos=(-11.99,1.61,5) rot=(0,0,1;0rad)
FEATURE [App::Link] Link_GDMLBox_Box005004
  CopyNumber = 22
  LinkPlacement = pos=(-11.99,5.01,5) rot=(0,0,1;0rad)
  LinkedObject = -> GDMLBox_Box005
  Placement = pos=(-11.99,5.01,5) rot=(0,0,1;0rad)
FEATURE [App::Link] Link_GDMLBox_Box005005
  CopyNumber = 23
  LinkPlacement = pos=(-11.99,8.41,5) rot=(0,0,1;0rad)
  LinkedObject = -> GDMLBox_Box005
  Placement = pos=(-11.99,8.41,5) rot=(0,0,1;0rad)
FEATURE [App::Link] Link_GDMLBox_Box005006
  CopyNumber = 24
  LinkPlacement = pos=(-11.99,11.81,5) rot=(0,0,1;0rad)
  LinkedObject = -> GDMLBox_Box005
  Placement = pos=(-11.99,11.81,5) rot=(0,0,1;0rad)
FEATURE [App::Link] Link_GDMLBox_Box005007
  CopyNumber = 25
  LinkPlacement = pos=(-8.59,-11.99,5) rot=(0,0,1;0rad)
  LinkedObject = -> GDMLBox_Box005
  Placement = pos=(-8.59,-11.99,5) rot=(0,0,1;0rad)
FEATURE [App::Link] Link_GDMLBox_Box005008
  CopyNumber = 26
  LinkPlacement = pos=(-8.59,-8.59,5) rot=(0,0,1;0rad)
  LinkedObject = -> GDMLBox_Box005
  Placement = pos=(-8.59,-8.59,5) rot=(0,0,1;0rad)
FEATURE [App::Link] Link_GDMLBox_Box005009
  CopyNumber = 27
  LinkPlacement = pos=(-8.59,-5.19,5) rot=(0,0,1;0rad)
  LinkedObject = -> GDMLBox_Box005
  Placement = pos=(-8.59,-5.19,5) rot=(0,0,1;0rad)
FEATURE [App::Link] Link_GDMLBox_Box005010
  CopyNumber = 28
  LinkPlacement = pos=(-8.59,-1.79,5) rot=(0,0,1;0rad)
  LinkedObject = -> GDMLBox_Box005
  Placement = pos=(-8.59,-1.79,5) rot=(0,0,1;0rad)
FEATURE [App::Link] Link_GDMLBox_Box005011
  CopyNumber = 29
  LinkPlacement = pos=(-8.59,1.61,5) rot=(0,0,1;0rad)
  LinkedObject = -> GDMLBox_Box005
  Placement = pos=(-8.59,1.61,5) rot=(0,0,1;0rad)
FEATURE [App::Link] Link_GDMLBox_Box005012
  CopyNumber = 30
  LinkPlacement = pos=(-8.59,5.01,5) rot=(0,0,1;0rad)
  LinkedObject = -> GDMLBox_Box005
  Placement = pos=(-8.59,5.01,5) rot=(0,0,1;0rad)
FEATURE [App::Link] Link_GDMLBox_Box005013
  CopyNumber = 31
  LinkPlacement = pos=(-8.59,8.41,5) rot=(0,0,1;0rad)
  LinkedObject = -> GDMLBox_Box005
  Placement = pos=(-8.59,8.41,5) rot=(0,0,1;0rad)
FEATURE [App::Link] Link_GDMLBox_Box005014
  CopyNumber = 32
  LinkPlacement = pos=(-8.59,11.81,5) rot=(0,0,1;0rad)
  LinkedObject = -> GDMLBox_Box005
  Placement = pos=(-8.59,11.81,5) rot=(0,0,1;0rad)
FEATURE [App::Link] Link_GDMLBox_Box005015
  CopyNumber = 33
  LinkPlacement = pos=(-5.19,-11.99,5) rot=(0,0,1;0rad)
  LinkedObject = -> GDMLBox_Box005
  Placement = pos=(-5.19,-11.99,5) rot=(0,0,1;0rad)
FEATURE [App::Link] Link_GDMLBox_Box005016
  CopyNumber = 34
  LinkPlacement = pos=(-5.19,-8.59,5) rot=(0,0,1;0rad)
  LinkedObject = -> GDMLBox_Box005
  Placement = pos=(-5.19,-8.59,5) rot=(0,0,1;0rad)
FEATURE [App::Link] Link_GDMLBox_Box005017
  CopyNumber = 35
  LinkPlacement = pos=(-5.19,-5.19,5) rot=(0,0,1;0rad)
  LinkedObject = -> GDMLBox_Box005
  Placement = pos=(-5.19,-5.19,5) rot=(0,0,1;0rad)
FEATURE [App::Link] Link_GDMLBox_Box005018
  CopyNumber = 36
  LinkPlacement = pos=(-5.19,-1.79,5) rot=(0,0,1;0rad)
  LinkedObject = -> GDMLBox_Box005
  Placement = pos=(-5.19,-1.79,5) rot=(0,0,1;0rad)
FEATURE [App::Link] Link_GDMLBox_Box005019
  CopyNumber = 37
  LinkPlacement = pos=(-5.19,1.61,5) rot=(0,0,1;0rad)
  LinkedObject = -> GDMLBox_Box005
  Placement = pos=(-5.19,1.61,5) rot=(0,0,1;0rad)
FEATURE [App::Link] Link_GDMLBox_Box005020
  CopyNumber = 38
  LinkPlacement = pos=(-5.19,5.01,5) rot=(0,0,1;0rad)
  LinkedObject = -> GDMLBox_Box005
  Placement = pos=(-5.19,5.01,5) rot=(0,0,1;0rad)
FEATURE [App::Link] Link_GDMLBox_Box005021
  CopyNumber = 39
  LinkPlacement = pos=(-5.19,8.41,5) rot=(0,0,1;0rad)
  LinkedObject = -> GDMLBox_Box005
  Placement = pos=(-5.19,8.41,5) rot=(0,0,1;0rad)
FEATURE [App::Link] Link_GDMLBox_Box005022
  CopyNumber = 40
  LinkPlacement = pos=(-5.19,11.81,5) rot=(0,0,1;0rad)
  LinkedObject = -> GDMLBox_Box005
  Placement = pos=(-5.19,11.81,5) rot=(0,0,1;0rad)
FEATURE [App::Link] Link_GDMLBox_Box005023
  CopyNumber = 41
  LinkPlacement = pos=(-1.79,-11.99,5) rot=(0,0,1;0rad)
  LinkedObject = -> GDMLBox_Box005
  Placement = pos=(-1.79,-11.99,5) rot=(0,0,1;0rad)
FEATURE [App::Link] Link_GDMLBox_Box005024
  CopyNumber = 42
  LinkPlacement = pos=(-1.79,-8.59,5) rot=(0,0,1;0rad)
  LinkedObject = -> GDMLBox_Box005
  Placement = pos=(-1.79,-8.59,5) rot=(0,0,1;0rad)
FEATURE [App::Link] Link_GDMLBox_Box005025
  CopyNumber = 43
  LinkPlacement = pos=(-1.79,-5.19,5) rot=(0,0,1;0rad)
  LinkedObject = -> GDMLBox_Box005
  Placement = pos=(-1.79,-5.19,5) rot=(0,0,1;0rad)
FEATURE [App::Link] Link_GDMLBox_Box005026
  CopyNumber = 44
  LinkPlacement = pos=(-1.79,-1.79,5) rot=(0,0,1;0rad)
  LinkedObject = -> GDMLBox_Box005
  Placement = pos=(-1.79,-1.79,5) rot=(0,0,1;0rad)
FEATURE [App::Link] Link_GDMLBox_Box005027
  CopyNumber = 45
  LinkPlacement = pos=(-1.79,1.61,5) rot=(0,0,1;0rad)
  LinkedObject = -> GDMLBox_Box005
  Placement = pos=(-1.79,1.61,5) rot=(0,0,1;0rad)
FEATURE [App::Link] Link_GDMLBox_Box005028
  CopyNumber = 46
  LinkPlacement = pos=(-1.79,5.01,5) rot=(0,0,1;0rad)
  LinkedObject = -> GDMLBox_Box005
  Placement = pos=(-1.79,5.01,5) rot=(0,0,1;0rad)
FEATURE [App::Link] Link_GDMLBox_Box005029
  CopyNumber = 47
  LinkPlacement = pos=(-1.79,8.41,5) rot=(0,0,1;0rad)
  LinkedObject = -> GDMLBox_Box005
  Placement = pos=(-1.79,8.41,5) rot=(0,0,1;0rad)
FEATURE [App::Link] Link_GDMLBox_Box005030
  CopyNumber = 48
  LinkPlacement = pos=(-1.79,11.81,5) rot=(0,0,1;0rad)
  LinkedObject = -> GDMLBox_Box005
  Placement = pos=(-1.79,11.81,5) rot=(0,0,1;0rad)
FEATURE [App::Link] Link_GDMLBox_Box005031
  CopyNumber = 49
  LinkPlacement = pos=(1.61,-11.99,5) rot=(0,0,1;0rad)
  LinkedObject = -> GDMLBox_Box005
  Placement = pos=(1.61,-11.99,5) rot=(0,0,1;0rad)
FEATURE [App::Link] Link_GDMLBox_Box005032
  CopyNumber = 50
  LinkPlacement = pos=(1.61,-8.59,5) rot=(0,0,1;0rad)
  LinkedObject = -> GDMLBox_Box005
  Placement = pos=(1.61,-8.59,5) rot=(0,0,1;0rad)
FEATURE [App::Link] Link_GDMLBox_Box005033
  CopyNumber = 51
  LinkPlacement = pos=(1.61,-5.19,5) rot=(0,0,1;0rad)
  LinkedObject = -> GDMLBox_Box005
  Placement = pos=(1.61,-5.19,5) rot=(0,0,1;0rad)
FEATURE [App::Link] Link_GDMLBox_Box005034
  CopyNumber = 52
  LinkPlacement = pos=(1.61,-1.79,5) rot=(0,0,1;0rad)
  LinkedObject = -> GDMLBox_Box005
  Placement = pos=(1.61,-1.79,5) rot=(0,0,1;0rad)
FEATURE [App::Link] Link_GDMLBox_Box005035
  CopyNumber = 53
  LinkPlacement = pos=(1.61,1.61,5) rot=(0,0,1;0rad)
  LinkedObject = -> GDMLBox_Box005
  Placement = pos=(1.61,1.61,5) rot=(0,0,1;0rad)
FEATURE [App::Link] Link_GDMLBox_Box005036
  CopyNumber = 54
  LinkPlacement = pos=(1.61,5.01,5) rot=(0,0,1;0rad)
  LinkedObject = -> GDMLBox_Box005
  Placement = pos=(1.61,5.01,5) rot=(0,0,1;0rad)
FEATURE [App::Link] Link_GDMLBox_Box005037
  CopyNumber = 55
  LinkPlacement = pos=(1.61,8.41,5) rot=(0,0,1;0rad)
  LinkedObject = -> GDMLBox_Box005
  Placement = pos=(1.61,8.41,5) rot=(0,0,1;0rad)
FEATURE [App::Link] Link_GDMLBox_Box005038
  CopyNumber = 56
  LinkPlacement = pos=(1.61,11.81,5) rot=(0,0,1;0rad)
  LinkedObject = -> GDMLBox_Box005
  Placement = pos=(1.61,11.81,5) rot=(0,0,1;0rad)
FEATURE [App::Link] Link_GDMLBox_Box005039
  CopyNumber = 57
  LinkPlacement = pos=(5.01,-11.99,5) rot=(0,0,1;0rad)
  LinkedObject = -> GDMLBox_Box005
  Placement = pos=(5.01,-11.99,5) rot=(0,0,1;0rad)
FEATURE [App::Link] Link_GDMLBox_Box005040
  CopyNumber = 58
  LinkPlacement = pos=(5.01,-8.59,5) rot=(0,0,1;0rad)
  LinkedObject = -> GDMLBox_Box005
  Placement = pos=(5.01,-8.59,5) rot=(0,0,1;0rad)
FEATURE [App::Link] Link_GDMLBox_Box005041
  CopyNumber = 59
  LinkPlacement = pos=(5.01,-5.19,5) rot=(0,0,1;0rad)
  LinkedObject = -> GDMLBox_Box005
  Placement = pos=(5.01,-5.19,5) rot=(0,0,1;0rad)
FEATURE [App::Link] Link_GDMLBox_Box005042
  CopyNumber = 60
  LinkPlacement = pos=(5.01,-1.79,5) rot=(0,0,1;0rad)
  LinkedObject = -> GDMLBox_Box005
  Placement = pos=(5.01,-1.79,5) rot=(0,0,1;0rad)
FEATURE [App::Link] Link_GDMLBox_Box005043
  CopyNumber = 61
  LinkPlacement = pos=(5.01,1.61,5) rot=(0,0,1;0rad)
  LinkedObject = -> GDMLBox_Box005
  Placement = pos=(5.01,1.61,5) rot=(0,0,1;0rad)
FEATURE [App::Link] Link_GDMLBox_Box005044
  CopyNumber = 62
  LinkPlacement = pos=(5.01,5.01,5) rot=(0,0,1;0rad)
  LinkedObject = -> GDMLBox_Box005
  Placement = pos=(5.01,5.01,5) rot=(0,0,1;0rad)
FEATURE [App::Link] Link_GDMLBox_Box005045
  CopyNumber = 63
  LinkPlacement = pos=(5.01,8.41,5) rot=(0,0,1;0rad)
  LinkedObject = -> GDMLBox_Box005
  Placement = pos=(5.01,8.41,5) rot=(0,0,1;0rad)
FEATURE [App::Link] Link_GDMLBox_Box005046
  CopyNumber = 64
  LinkPlacement = pos=(5.01,11.81,5) rot=(0,0,1;0rad)
  LinkedObject = -> GDMLBox_Box005
  Placement = pos=(5.01,11.81,5) rot=(0,0,1;0rad)
FEATURE [App::Link] Link_GDMLBox_Box005047
  CopyNumber = 65
  LinkPlacement = pos=(8.41,-11.99,5) rot=(0,0,1;0rad)
  LinkedObject = -> GDMLBox_Box005
  Placement = pos=(8.41,-11.99,5) rot=(0,0,1;0rad)
FEATURE [App::Link] Link_GDMLBox_Box005048
  CopyNumber = 66
  LinkPlacement = pos=(8.41,-8.59,5) rot=(0,0,1;0rad)
  LinkedObject = -> GDMLBox_Box005
  Placement = pos=(8.41,-8.59,5) rot=(0,0,1;0rad)
FEATURE [App::Link] Link_GDMLBox_Box005049
  CopyNumber = 67
  LinkPlacement = pos=(8.41,-5.19,5) rot=(0,0,1;0rad)
  LinkedObject = -> GDMLBox_Box005
  Placement = pos=(8.41,-5.19,5) rot=(0,0,1;0rad)
FEATURE [App::Link] Link_GDMLBox_Box005050
  CopyNumber = 68
  LinkPlacement = pos=(8.41,-1.79,5) rot=(0,0,1;0rad)
  LinkedObject = -> GDMLBox_Box005
  Placement = pos=(8.41,-1.79,5) rot=(0,0,1;0rad)
FEATURE [App::Link] Link_GDMLBox_Box005051
  CopyNumber = 69
  LinkPlacement = pos=(8.41,1.61,5) rot=(0,0,1;0rad)
  LinkedObject = -> GDMLBox_Box005
  Placement = pos=(8.41,1.61,5) rot=(0,0,1;0rad)
FEATURE [App::Link] Link_GDMLBox_Box005052
  CopyNumber = 70
  LinkPlacement = pos=(8.41,5.01,5) rot=(0,0,1;0rad)
  LinkedObject = -> GDMLBox_Box005
  Placement = pos=(8.41,5.01,5) rot=(0,0,1;0rad)
FEATURE [App::Link] Link_GDMLBox_Box005053
  CopyNumber = 71
  LinkPlacement = pos=(8.41,8.41,5) rot=(0,0,1;0rad)
  LinkedObject = -> GDMLBox_Box005
  Placement = pos=(8.41,8.41,5) rot=(0,0,1;0rad)
FEATURE [App::Link] Link_GDMLBox_Box005054
  CopyNumber = 72
  LinkPlacement = pos=(8.41,11.81,5) rot=(0,0,1;0rad)
  LinkedObject = -> GDMLBox_Box005
  Placement = pos=(8.41,11.81,5) rot=(0,0,1;0rad)
FEATURE [App::Link] Link_GDMLBox_Box005055
  CopyNumber = 73
  LinkPlacement = pos=(11.81,-11.99,5) rot=(0,0,1;0rad)
  LinkedObject = -> GDMLBox_Box005
  Placement = pos=(11.81,-11.99,5) rot=(0,0,1;0rad)
FEATURE [App::Link] Link_GDMLBox_Box005056
  CopyNumber = 74
  LinkPlacement = pos=(11.81,-8.59,5) rot=(0,0,1;0rad)
  LinkedObject = -> GDMLBox_Box005
  Placement = pos=(11.81,-8.59,5) rot=(0,0,1;0rad)
FEATURE [App::Link] Link_GDMLBox_Box005057
  CopyNumber = 75
  LinkPlacement = pos=(11.81,-5.19,5) rot=(0,0,1;0rad)
  LinkedObject = -> GDMLBox_Box005
  Placement = pos=(11.81,-5.19,5) rot=(0,0,1;0rad)
FEATURE [App::Link] Link_GDMLBox_Box005058
  CopyNumber = 76
  LinkPlacement = pos=(11.81,-1.79,5) rot=(0,0,1;0rad)
  LinkedObject = -> GDMLBox_Box005
  Placement = pos=(11.81,-1.79,5) rot=(0,0,1;0rad)
FEATURE [App::Link] Link_GDMLBox_Box005059
  CopyNumber = 77
  LinkPlacement = pos=(11.81,1.61,5) rot=(0,0,1;0rad)
  LinkedObject = -> GDMLBox_Box005
  Placement = pos=(11.81,1.61,5) rot=(0,0,1;0rad)
FEATURE [App::Link] Link_GDMLBox_Box005060
  CopyNumber = 78
  LinkPlacement = pos=(11.81,5.01,5) rot=(0,0,1;0rad)
  LinkedObject = -> GDMLBox_Box005
  Placement = pos=(11.81,5.01,5) rot=(0,0,1;0rad)
FEATURE [App::Link] Link_GDMLBox_Box005061
  CopyNumber = 79
  LinkPlacement = pos=(11.81,8.41,5) rot=(0,0,1;0rad)
  LinkedObject = -> GDMLBox_Box005
  Placement = pos=(11.81,8.41,5) rot=(0,0,1;0rad)
FEATURE [App::Link] Link_GDMLBox_Box005062
  CopyNumber = 80
  LinkPlacement = pos=(11.81,11.81,5) rot=(0,0,1;0rad)
  LinkedObject = -> GDMLBox_Box005
  Placement = pos=(11.81,11.81,5) rot=(0,0,1;0rad)
FEATURE [App::Part] Child_Array  label="Child_Array001"
  CopyNumber = 9
  Group = -> [GDMLBox_Box005,Link_GDMLBox_Box005,Link_GDMLBox_Box005001,Link_GDMLBox_Box005002,Link_GDMLBox_Box005003,Link_GDMLBox_Box005004,Link_GDMLBox_Box005005,Link_GDMLBox_Box005006,Link_GDMLBox_Box005007,Link_GDMLBox_Box005008,Link_GDMLBox_Box005009,Link_GDMLBox_Box005010,Link_GDMLBox_Box005011,Link_GDMLBox_Box005012,Link_GDMLBox_Box005013,Link_GDMLBox_Box005014,Link_GDMLBox_Box005015,+47 more]
  Origin = -> Origin007
  Placement = pos=(0,0,37.85) rot=(0,0,1;0rad)
FEATURE [App::Part] Parent_Array  label="Parent_Array001"
  Group = -> [Child_Array,Link_Child_Array,Link_Child_Array001,Link_Child_Array002,Link_Child_Array003,Link_Child_Array004,Link_Child_Array005,Link_Child_Array006]
  Origin = -> Origin006
FEATURE [App::Part] Part
  Group = -> [Parent_Array]
  Origin = -> Origin003
FEATURE [App::Part] worldVOL
  Group = -> [GDMLBox_WorldBox,Part001,Part,LV_Sphere]
  Origin = -> Origin
FEATURE [App::FeaturePython] ScintWrap1  # WARN: FeaturePython — macro-defined, semantics opaque (R4)
  CheckCommonFaces = true
  PV1 = -> Part001
  PV2 = -> LV_Sphere
  Surface = ScintWrap
